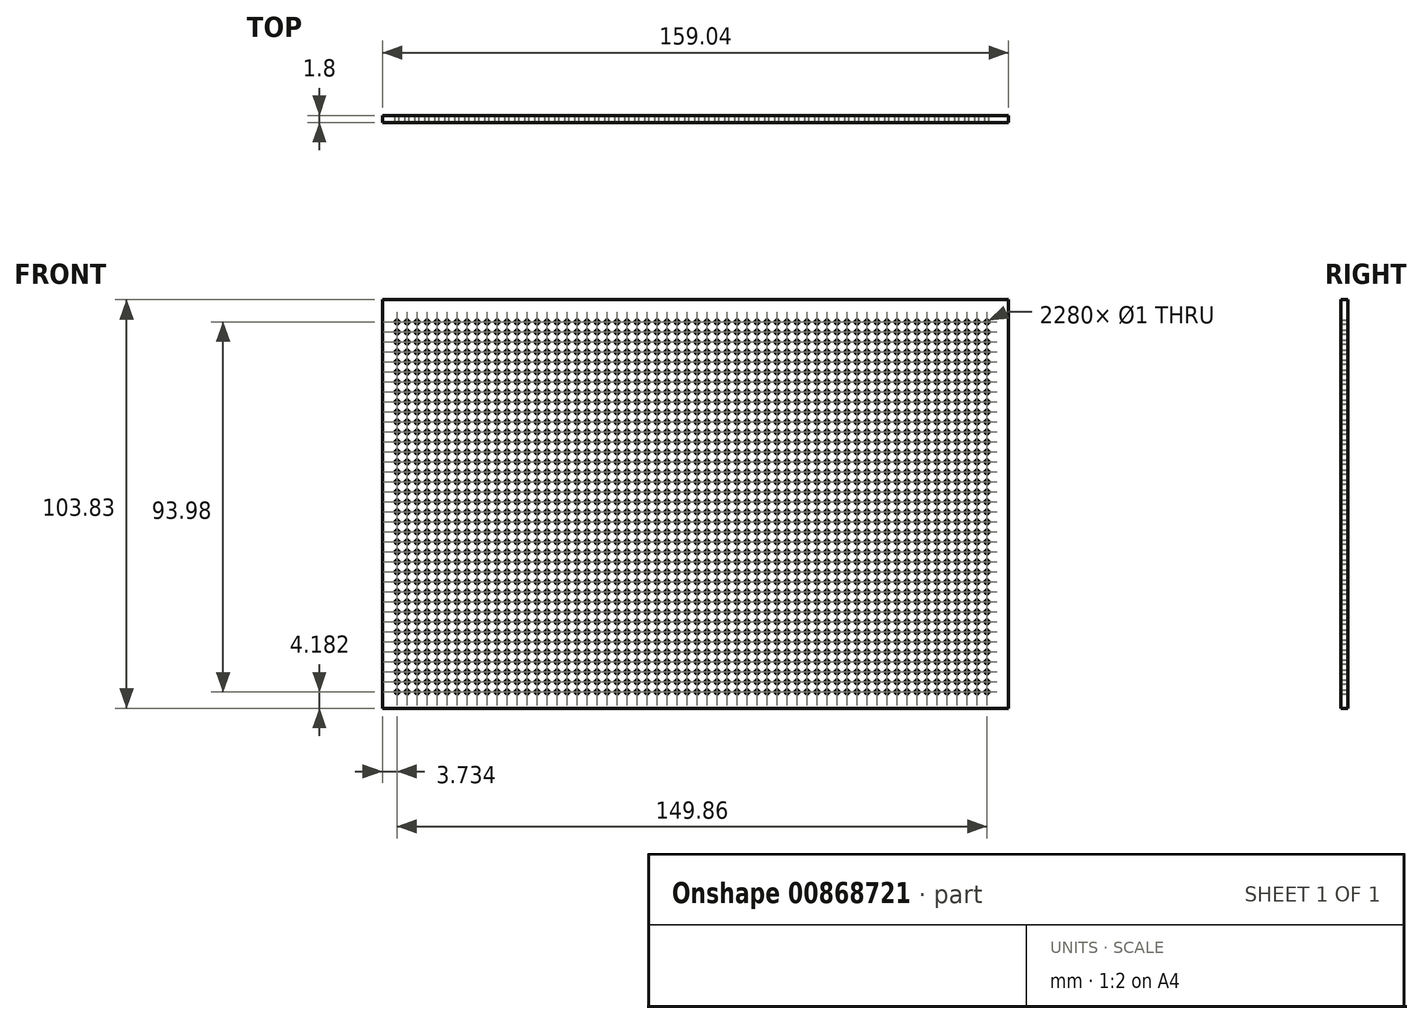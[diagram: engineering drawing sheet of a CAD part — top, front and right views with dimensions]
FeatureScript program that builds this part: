
annotation { "Feature Type Name" : "Feature", "Feature Type Description" : "" }
export const myFeature = defineFeature(function(context is Context, id is Id, definition is map)
    precondition{}
    {
        {
            var Q0;
            Q0=qCreatedBy(makeId("Front.planeOp"),FACE);
            var sketch = newSketch(context, id + "F0", { "sketchPlane" : qUnion([Q0])});
            skCircle(sketch, "E0", {"center": v(-205.8, 91.36) * mm, "radius": 0.5 * mm});
            skCircle(sketch, "E1.0.1.0", {"center": v(-205.8, 93.9) * mm, "radius": 0.5 * mm});
            skCircle(sketch, "E1.0.2.0", {"center": v(-205.8, 96.44) * mm, "radius": 0.5 * mm});
            skCircle(sketch, "E1.0.3.0", {"center": v(-205.8, 98.98) * mm, "radius": 0.5 * mm});
            skCircle(sketch, "E1.0.4.0", {"center": v(-205.8, 101.52) * mm, "radius": 0.5 * mm});
            skCircle(sketch, "E1.0.5.0", {"center": v(-205.8, 104.06) * mm, "radius": 0.5 * mm});
            skCircle(sketch, "E1.0.6.0", {"center": v(-205.8, 106.6) * mm, "radius": 0.5 * mm});
            skCircle(sketch, "E1.0.7.0", {"center": v(-205.8, 109.14) * mm, "radius": 0.5 * mm});
            skCircle(sketch, "E1.0.8.0", {"center": v(-205.8, 111.68) * mm, "radius": 0.5 * mm});
            skCircle(sketch, "E1.0.9.0", {"center": v(-205.8, 114.22) * mm, "radius": 0.5 * mm});
            skCircle(sketch, "E1.0.10.0", {"center": v(-205.8, 116.76) * mm, "radius": 0.5 * mm});
            skCircle(sketch, "E1.0.11.0", {"center": v(-205.8, 119.3) * mm, "radius": 0.5 * mm});
            skCircle(sketch, "E1.0.12.0", {"center": v(-205.8, 121.84) * mm, "radius": 0.5 * mm});
            skCircle(sketch, "E1.0.13.0", {"center": v(-205.8, 124.38) * mm, "radius": 0.5 * mm});
            skCircle(sketch, "E1.0.14.0", {"center": v(-205.8, 126.92) * mm, "radius": 0.5 * mm});
            skCircle(sketch, "E1.0.15.0", {"center": v(-205.8, 129.46) * mm, "radius": 0.5 * mm});
            skCircle(sketch, "E1.0.16.0", {"center": v(-205.8, 132) * mm, "radius": 0.5 * mm});
            skCircle(sketch, "E1.0.17.0", {"center": v(-205.8, 134.54) * mm, "radius": 0.5 * mm});
            skCircle(sketch, "E1.0.18.0", {"center": v(-205.8, 137.08) * mm, "radius": 0.5 * mm});
            skCircle(sketch, "E1.0.19.0", {"center": v(-205.8, 139.62) * mm, "radius": 0.5 * mm});
            skCircle(sketch, "E1.0.20.0", {"center": v(-205.8, 142.16) * mm, "radius": 0.5 * mm});
            skCircle(sketch, "E1.0.21.0", {"center": v(-205.8, 144.7) * mm, "radius": 0.5 * mm});
            skCircle(sketch, "E1.0.22.0", {"center": v(-205.8, 147.24) * mm, "radius": 0.5 * mm});
            skCircle(sketch, "E1.0.23.0", {"center": v(-205.8, 149.78) * mm, "radius": 0.5 * mm});
            skCircle(sketch, "E1.0.24.0", {"center": v(-205.8, 152.32) * mm, "radius": 0.5 * mm});
            skCircle(sketch, "E1.0.25.0", {"center": v(-205.8, 154.86) * mm, "radius": 0.5 * mm});
            skCircle(sketch, "E1.0.26.0", {"center": v(-205.8, 157.4) * mm, "radius": 0.5 * mm});
            skCircle(sketch, "E1.0.27.0", {"center": v(-205.8, 159.94) * mm, "radius": 0.5 * mm});
            skCircle(sketch, "E1.0.28.0", {"center": v(-205.8, 162.48) * mm, "radius": 0.5 * mm});
            skCircle(sketch, "E1.0.29.0", {"center": v(-205.8, 165.02) * mm, "radius": 0.5 * mm});
            skCircle(sketch, "E1.0.30.0", {"center": v(-205.8, 167.56) * mm, "radius": 0.5 * mm});
            skCircle(sketch, "E1.0.31.0", {"center": v(-205.8, 170.1) * mm, "radius": 0.5 * mm});
            skCircle(sketch, "E1.0.32.0", {"center": v(-205.8, 172.64) * mm, "radius": 0.5 * mm});
            skCircle(sketch, "E1.0.33.0", {"center": v(-205.8, 175.18) * mm, "radius": 0.5 * mm});
            skCircle(sketch, "E1.0.34.0", {"center": v(-205.8, 177.72) * mm, "radius": 0.5 * mm});
            skCircle(sketch, "E1.0.35.0", {"center": v(-205.8, 180.26) * mm, "radius": 0.5 * mm});
            skCircle(sketch, "E1.0.36.0", {"center": v(-205.8, 182.8) * mm, "radius": 0.5 * mm});
            skCircle(sketch, "E1.0.37.0", {"center": v(-205.8, 185.34) * mm, "radius": 0.5 * mm});
            skCircle(sketch, "E1.1.0.0", {"center": v(-203.27, 91.36) * mm, "radius": 0.5 * mm});
            skCircle(sketch, "E1.1.1.0", {"center": v(-203.27, 93.9) * mm, "radius": 0.5 * mm});
            skCircle(sketch, "E1.1.2.0", {"center": v(-203.27, 96.44) * mm, "radius": 0.5 * mm});
            skCircle(sketch, "E1.1.3.0", {"center": v(-203.27, 98.98) * mm, "radius": 0.5 * mm});
            skCircle(sketch, "E1.1.4.0", {"center": v(-203.27, 101.52) * mm, "radius": 0.5 * mm});
            skCircle(sketch, "E1.1.5.0", {"center": v(-203.27, 104.06) * mm, "radius": 0.5 * mm});
            skCircle(sketch, "E1.1.6.0", {"center": v(-203.27, 106.6) * mm, "radius": 0.5 * mm});
            skCircle(sketch, "E1.1.7.0", {"center": v(-203.27, 109.14) * mm, "radius": 0.5 * mm});
            skCircle(sketch, "E1.1.8.0", {"center": v(-203.27, 111.68) * mm, "radius": 0.5 * mm});
            skCircle(sketch, "E1.1.9.0", {"center": v(-203.27, 114.22) * mm, "radius": 0.5 * mm});
            skCircle(sketch, "E1.1.10.0", {"center": v(-203.27, 116.76) * mm, "radius": 0.5 * mm});
            skCircle(sketch, "E1.1.11.0", {"center": v(-203.27, 119.3) * mm, "radius": 0.5 * mm});
            skCircle(sketch, "E1.1.12.0", {"center": v(-203.27, 121.84) * mm, "radius": 0.5 * mm});
            skCircle(sketch, "E1.1.13.0", {"center": v(-203.27, 124.38) * mm, "radius": 0.5 * mm});
            skCircle(sketch, "E1.1.14.0", {"center": v(-203.27, 126.92) * mm, "radius": 0.5 * mm});
            skCircle(sketch, "E1.1.15.0", {"center": v(-203.27, 129.46) * mm, "radius": 0.5 * mm});
            skCircle(sketch, "E1.1.16.0", {"center": v(-203.27, 132) * mm, "radius": 0.5 * mm});
            skCircle(sketch, "E1.1.17.0", {"center": v(-203.27, 134.54) * mm, "radius": 0.5 * mm});
            skCircle(sketch, "E1.1.18.0", {"center": v(-203.27, 137.08) * mm, "radius": 0.5 * mm});
            skCircle(sketch, "E1.1.19.0", {"center": v(-203.27, 139.62) * mm, "radius": 0.5 * mm});
            skCircle(sketch, "E1.1.20.0", {"center": v(-203.27, 142.16) * mm, "radius": 0.5 * mm});
            skCircle(sketch, "E1.1.21.0", {"center": v(-203.27, 144.7) * mm, "radius": 0.5 * mm});
            skCircle(sketch, "E1.1.22.0", {"center": v(-203.27, 147.24) * mm, "radius": 0.5 * mm});
            skCircle(sketch, "E1.1.23.0", {"center": v(-203.27, 149.78) * mm, "radius": 0.5 * mm});
            skCircle(sketch, "E1.1.24.0", {"center": v(-203.27, 152.32) * mm, "radius": 0.5 * mm});
            skCircle(sketch, "E1.1.25.0", {"center": v(-203.27, 154.86) * mm, "radius": 0.5 * mm});
            skCircle(sketch, "E1.1.26.0", {"center": v(-203.27, 157.4) * mm, "radius": 0.5 * mm});
            skCircle(sketch, "E1.1.27.0", {"center": v(-203.27, 159.94) * mm, "radius": 0.5 * mm});
            skCircle(sketch, "E1.1.28.0", {"center": v(-203.27, 162.48) * mm, "radius": 0.5 * mm});
            skCircle(sketch, "E1.1.29.0", {"center": v(-203.27, 165.02) * mm, "radius": 0.5 * mm});
            skCircle(sketch, "E1.1.30.0", {"center": v(-203.27, 167.56) * mm, "radius": 0.5 * mm});
            skCircle(sketch, "E1.1.31.0", {"center": v(-203.27, 170.1) * mm, "radius": 0.5 * mm});
            skCircle(sketch, "E1.1.32.0", {"center": v(-203.27, 172.64) * mm, "radius": 0.5 * mm});
            skCircle(sketch, "E1.1.33.0", {"center": v(-203.27, 175.18) * mm, "radius": 0.5 * mm});
            skCircle(sketch, "E1.1.34.0", {"center": v(-203.27, 177.72) * mm, "radius": 0.5 * mm});
            skCircle(sketch, "E1.1.35.0", {"center": v(-203.27, 180.26) * mm, "radius": 0.5 * mm});
            skCircle(sketch, "E1.1.36.0", {"center": v(-203.27, 182.8) * mm, "radius": 0.5 * mm});
            skCircle(sketch, "E1.1.37.0", {"center": v(-203.27, 185.34) * mm, "radius": 0.5 * mm});
            skCircle(sketch, "E1.2.0.0", {"center": v(-200.73, 91.36) * mm, "radius": 0.5 * mm});
            skCircle(sketch, "E1.2.1.0", {"center": v(-200.73, 93.9) * mm, "radius": 0.5 * mm});
            skCircle(sketch, "E1.2.2.0", {"center": v(-200.73, 96.44) * mm, "radius": 0.5 * mm});
            skCircle(sketch, "E1.2.3.0", {"center": v(-200.73, 98.98) * mm, "radius": 0.5 * mm});
            skCircle(sketch, "E1.2.4.0", {"center": v(-200.73, 101.52) * mm, "radius": 0.5 * mm});
            skCircle(sketch, "E1.2.5.0", {"center": v(-200.73, 104.06) * mm, "radius": 0.5 * mm});
            skCircle(sketch, "E1.2.6.0", {"center": v(-200.73, 106.6) * mm, "radius": 0.5 * mm});
            skCircle(sketch, "E1.2.7.0", {"center": v(-200.73, 109.14) * mm, "radius": 0.5 * mm});
            skCircle(sketch, "E1.2.8.0", {"center": v(-200.73, 111.68) * mm, "radius": 0.5 * mm});
            skCircle(sketch, "E1.2.9.0", {"center": v(-200.73, 114.22) * mm, "radius": 0.5 * mm});
            skCircle(sketch, "E1.2.10.0", {"center": v(-200.73, 116.76) * mm, "radius": 0.5 * mm});
            skCircle(sketch, "E1.2.11.0", {"center": v(-200.73, 119.3) * mm, "radius": 0.5 * mm});
            skCircle(sketch, "E1.2.12.0", {"center": v(-200.73, 121.84) * mm, "radius": 0.5 * mm});
            skCircle(sketch, "E1.2.13.0", {"center": v(-200.73, 124.38) * mm, "radius": 0.5 * mm});
            skCircle(sketch, "E1.2.14.0", {"center": v(-200.73, 126.92) * mm, "radius": 0.5 * mm});
            skCircle(sketch, "E1.2.15.0", {"center": v(-200.73, 129.46) * mm, "radius": 0.5 * mm});
            skCircle(sketch, "E1.2.16.0", {"center": v(-200.73, 132) * mm, "radius": 0.5 * mm});
            skCircle(sketch, "E1.2.17.0", {"center": v(-200.73, 134.54) * mm, "radius": 0.5 * mm});
            skCircle(sketch, "E1.2.18.0", {"center": v(-200.73, 137.08) * mm, "radius": 0.5 * mm});
            skCircle(sketch, "E1.2.19.0", {"center": v(-200.73, 139.62) * mm, "radius": 0.5 * mm});
            skCircle(sketch, "E1.2.20.0", {"center": v(-200.73, 142.16) * mm, "radius": 0.5 * mm});
            skCircle(sketch, "E1.2.21.0", {"center": v(-200.73, 144.7) * mm, "radius": 0.5 * mm});
            skCircle(sketch, "E1.2.22.0", {"center": v(-200.73, 147.24) * mm, "radius": 0.5 * mm});
            skCircle(sketch, "E1.2.23.0", {"center": v(-200.73, 149.78) * mm, "radius": 0.5 * mm});
            skCircle(sketch, "E1.2.24.0", {"center": v(-200.73, 152.32) * mm, "radius": 0.5 * mm});
            skCircle(sketch, "E1.2.25.0", {"center": v(-200.73, 154.86) * mm, "radius": 0.5 * mm});
            skCircle(sketch, "E1.2.26.0", {"center": v(-200.73, 157.4) * mm, "radius": 0.5 * mm});
            skCircle(sketch, "E1.2.27.0", {"center": v(-200.73, 159.94) * mm, "radius": 0.5 * mm});
            skCircle(sketch, "E1.2.28.0", {"center": v(-200.73, 162.48) * mm, "radius": 0.5 * mm});
            skCircle(sketch, "E1.2.29.0", {"center": v(-200.73, 165.02) * mm, "radius": 0.5 * mm});
            skCircle(sketch, "E1.2.30.0", {"center": v(-200.73, 167.56) * mm, "radius": 0.5 * mm});
            skCircle(sketch, "E1.2.31.0", {"center": v(-200.73, 170.1) * mm, "radius": 0.5 * mm});
            skCircle(sketch, "E1.2.32.0", {"center": v(-200.73, 172.64) * mm, "radius": 0.5 * mm});
            skCircle(sketch, "E1.2.33.0", {"center": v(-200.73, 175.18) * mm, "radius": 0.5 * mm});
            skCircle(sketch, "E1.2.34.0", {"center": v(-200.73, 177.72) * mm, "radius": 0.5 * mm});
            skCircle(sketch, "E1.2.35.0", {"center": v(-200.73, 180.26) * mm, "radius": 0.5 * mm});
            skCircle(sketch, "E1.2.36.0", {"center": v(-200.73, 182.8) * mm, "radius": 0.5 * mm});
            skCircle(sketch, "E1.2.37.0", {"center": v(-200.73, 185.34) * mm, "radius": 0.5 * mm});
            skCircle(sketch, "E1.3.0.0", {"center": v(-198.19, 91.36) * mm, "radius": 0.5 * mm});
            skCircle(sketch, "E1.3.1.0", {"center": v(-198.19, 93.9) * mm, "radius": 0.5 * mm});
            skCircle(sketch, "E1.3.2.0", {"center": v(-198.19, 96.44) * mm, "radius": 0.5 * mm});
            skCircle(sketch, "E1.3.3.0", {"center": v(-198.19, 98.98) * mm, "radius": 0.5 * mm});
            skCircle(sketch, "E1.3.4.0", {"center": v(-198.19, 101.52) * mm, "radius": 0.5 * mm});
            skCircle(sketch, "E1.3.5.0", {"center": v(-198.19, 104.06) * mm, "radius": 0.5 * mm});
            skCircle(sketch, "E1.3.6.0", {"center": v(-198.19, 106.6) * mm, "radius": 0.5 * mm});
            skCircle(sketch, "E1.3.7.0", {"center": v(-198.19, 109.14) * mm, "radius": 0.5 * mm});
            skCircle(sketch, "E1.3.8.0", {"center": v(-198.19, 111.68) * mm, "radius": 0.5 * mm});
            skCircle(sketch, "E1.3.9.0", {"center": v(-198.19, 114.22) * mm, "radius": 0.5 * mm});
            skCircle(sketch, "E1.3.10.0", {"center": v(-198.19, 116.76) * mm, "radius": 0.5 * mm});
            skCircle(sketch, "E1.3.11.0", {"center": v(-198.19, 119.3) * mm, "radius": 0.5 * mm});
            skCircle(sketch, "E1.3.12.0", {"center": v(-198.19, 121.84) * mm, "radius": 0.5 * mm});
            skCircle(sketch, "E1.3.13.0", {"center": v(-198.19, 124.38) * mm, "radius": 0.5 * mm});
            skCircle(sketch, "E1.3.14.0", {"center": v(-198.19, 126.92) * mm, "radius": 0.5 * mm});
            skCircle(sketch, "E1.3.15.0", {"center": v(-198.19, 129.46) * mm, "radius": 0.5 * mm});
            skCircle(sketch, "E1.3.16.0", {"center": v(-198.19, 132) * mm, "radius": 0.5 * mm});
            skCircle(sketch, "E1.3.17.0", {"center": v(-198.19, 134.54) * mm, "radius": 0.5 * mm});
            skCircle(sketch, "E1.3.18.0", {"center": v(-198.19, 137.08) * mm, "radius": 0.5 * mm});
            skCircle(sketch, "E1.3.19.0", {"center": v(-198.19, 139.62) * mm, "radius": 0.5 * mm});
            skCircle(sketch, "E1.3.20.0", {"center": v(-198.19, 142.16) * mm, "radius": 0.5 * mm});
            skCircle(sketch, "E1.3.21.0", {"center": v(-198.19, 144.7) * mm, "radius": 0.5 * mm});
            skCircle(sketch, "E1.3.22.0", {"center": v(-198.19, 147.24) * mm, "radius": 0.5 * mm});
            skCircle(sketch, "E1.3.23.0", {"center": v(-198.19, 149.78) * mm, "radius": 0.5 * mm});
            skCircle(sketch, "E1.3.24.0", {"center": v(-198.19, 152.32) * mm, "radius": 0.5 * mm});
            skCircle(sketch, "E1.3.25.0", {"center": v(-198.19, 154.86) * mm, "radius": 0.5 * mm});
            skCircle(sketch, "E1.3.26.0", {"center": v(-198.19, 157.4) * mm, "radius": 0.5 * mm});
            skCircle(sketch, "E1.3.27.0", {"center": v(-198.19, 159.94) * mm, "radius": 0.5 * mm});
            skCircle(sketch, "E1.3.28.0", {"center": v(-198.19, 162.48) * mm, "radius": 0.5 * mm});
            skCircle(sketch, "E1.3.29.0", {"center": v(-198.19, 165.02) * mm, "radius": 0.5 * mm});
            skCircle(sketch, "E1.3.30.0", {"center": v(-198.19, 167.56) * mm, "radius": 0.5 * mm});
            skCircle(sketch, "E1.3.31.0", {"center": v(-198.19, 170.1) * mm, "radius": 0.5 * mm});
            skCircle(sketch, "E1.3.32.0", {"center": v(-198.19, 172.64) * mm, "radius": 0.5 * mm});
            skCircle(sketch, "E1.3.33.0", {"center": v(-198.19, 175.18) * mm, "radius": 0.5 * mm});
            skCircle(sketch, "E1.3.34.0", {"center": v(-198.19, 177.72) * mm, "radius": 0.5 * mm});
            skCircle(sketch, "E1.3.35.0", {"center": v(-198.19, 180.26) * mm, "radius": 0.5 * mm});
            skCircle(sketch, "E1.3.36.0", {"center": v(-198.19, 182.8) * mm, "radius": 0.5 * mm});
            skCircle(sketch, "E1.3.37.0", {"center": v(-198.19, 185.34) * mm, "radius": 0.5 * mm});
            skCircle(sketch, "E1.4.0.0", {"center": v(-195.65, 91.36) * mm, "radius": 0.5 * mm});
            skCircle(sketch, "E1.4.1.0", {"center": v(-195.65, 93.9) * mm, "radius": 0.5 * mm});
            skCircle(sketch, "E1.4.2.0", {"center": v(-195.65, 96.44) * mm, "radius": 0.5 * mm});
            skCircle(sketch, "E1.4.3.0", {"center": v(-195.65, 98.98) * mm, "radius": 0.5 * mm});
            skCircle(sketch, "E1.4.4.0", {"center": v(-195.65, 101.52) * mm, "radius": 0.5 * mm});
            skCircle(sketch, "E1.4.5.0", {"center": v(-195.65, 104.06) * mm, "radius": 0.5 * mm});
            skCircle(sketch, "E1.4.6.0", {"center": v(-195.65, 106.6) * mm, "radius": 0.5 * mm});
            skCircle(sketch, "E1.4.7.0", {"center": v(-195.65, 109.14) * mm, "radius": 0.5 * mm});
            skCircle(sketch, "E1.4.8.0", {"center": v(-195.65, 111.68) * mm, "radius": 0.5 * mm});
            skCircle(sketch, "E1.4.9.0", {"center": v(-195.65, 114.22) * mm, "radius": 0.5 * mm});
            skCircle(sketch, "E1.4.10.0", {"center": v(-195.65, 116.76) * mm, "radius": 0.5 * mm});
            skCircle(sketch, "E1.4.11.0", {"center": v(-195.65, 119.3) * mm, "radius": 0.5 * mm});
            skCircle(sketch, "E1.4.12.0", {"center": v(-195.65, 121.84) * mm, "radius": 0.5 * mm});
            skCircle(sketch, "E1.4.13.0", {"center": v(-195.65, 124.38) * mm, "radius": 0.5 * mm});
            skCircle(sketch, "E1.4.14.0", {"center": v(-195.65, 126.92) * mm, "radius": 0.5 * mm});
            skCircle(sketch, "E1.4.15.0", {"center": v(-195.65, 129.46) * mm, "radius": 0.5 * mm});
            skCircle(sketch, "E1.4.16.0", {"center": v(-195.65, 132) * mm, "radius": 0.5 * mm});
            skCircle(sketch, "E1.4.17.0", {"center": v(-195.65, 134.54) * mm, "radius": 0.5 * mm});
            skCircle(sketch, "E1.4.18.0", {"center": v(-195.65, 137.08) * mm, "radius": 0.5 * mm});
            skCircle(sketch, "E1.4.19.0", {"center": v(-195.65, 139.62) * mm, "radius": 0.5 * mm});
            skCircle(sketch, "E1.4.20.0", {"center": v(-195.65, 142.16) * mm, "radius": 0.5 * mm});
            skCircle(sketch, "E1.4.21.0", {"center": v(-195.65, 144.7) * mm, "radius": 0.5 * mm});
            skCircle(sketch, "E1.4.22.0", {"center": v(-195.65, 147.24) * mm, "radius": 0.5 * mm});
            skCircle(sketch, "E1.4.23.0", {"center": v(-195.65, 149.78) * mm, "radius": 0.5 * mm});
            skCircle(sketch, "E1.4.24.0", {"center": v(-195.65, 152.32) * mm, "radius": 0.5 * mm});
            skCircle(sketch, "E1.4.25.0", {"center": v(-195.65, 154.86) * mm, "radius": 0.5 * mm});
            skCircle(sketch, "E1.4.26.0", {"center": v(-195.65, 157.4) * mm, "radius": 0.5 * mm});
            skCircle(sketch, "E1.4.27.0", {"center": v(-195.65, 159.94) * mm, "radius": 0.5 * mm});
            skCircle(sketch, "E1.4.28.0", {"center": v(-195.65, 162.48) * mm, "radius": 0.5 * mm});
            skCircle(sketch, "E1.4.29.0", {"center": v(-195.65, 165.02) * mm, "radius": 0.5 * mm});
            skCircle(sketch, "E1.4.30.0", {"center": v(-195.65, 167.56) * mm, "radius": 0.5 * mm});
            skCircle(sketch, "E1.4.31.0", {"center": v(-195.65, 170.1) * mm, "radius": 0.5 * mm});
            skCircle(sketch, "E1.4.32.0", {"center": v(-195.65, 172.64) * mm, "radius": 0.5 * mm});
            skCircle(sketch, "E1.4.33.0", {"center": v(-195.65, 175.18) * mm, "radius": 0.5 * mm});
            skCircle(sketch, "E1.4.34.0", {"center": v(-195.65, 177.72) * mm, "radius": 0.5 * mm});
            skCircle(sketch, "E1.4.35.0", {"center": v(-195.65, 180.26) * mm, "radius": 0.5 * mm});
            skCircle(sketch, "E1.4.36.0", {"center": v(-195.65, 182.8) * mm, "radius": 0.5 * mm});
            skCircle(sketch, "E1.4.37.0", {"center": v(-195.65, 185.34) * mm, "radius": 0.5 * mm});
            skCircle(sketch, "E1.5.0.0", {"center": v(-193.1, 91.36) * mm, "radius": 0.5 * mm});
            skCircle(sketch, "E1.5.1.0", {"center": v(-193.1, 93.9) * mm, "radius": 0.5 * mm});
            skCircle(sketch, "E1.5.2.0", {"center": v(-193.1, 96.44) * mm, "radius": 0.5 * mm});
            skCircle(sketch, "E1.5.3.0", {"center": v(-193.1, 98.98) * mm, "radius": 0.5 * mm});
            skCircle(sketch, "E1.5.4.0", {"center": v(-193.1, 101.52) * mm, "radius": 0.5 * mm});
            skCircle(sketch, "E1.5.5.0", {"center": v(-193.1, 104.06) * mm, "radius": 0.5 * mm});
            skCircle(sketch, "E1.5.6.0", {"center": v(-193.1, 106.6) * mm, "radius": 0.5 * mm});
            skCircle(sketch, "E1.5.7.0", {"center": v(-193.1, 109.14) * mm, "radius": 0.5 * mm});
            skCircle(sketch, "E1.5.8.0", {"center": v(-193.1, 111.68) * mm, "radius": 0.5 * mm});
            skCircle(sketch, "E1.5.9.0", {"center": v(-193.1, 114.22) * mm, "radius": 0.5 * mm});
            skCircle(sketch, "E1.5.10.0", {"center": v(-193.1, 116.76) * mm, "radius": 0.5 * mm});
            skCircle(sketch, "E1.5.11.0", {"center": v(-193.1, 119.3) * mm, "radius": 0.5 * mm});
            skCircle(sketch, "E1.5.12.0", {"center": v(-193.1, 121.84) * mm, "radius": 0.5 * mm});
            skCircle(sketch, "E1.5.13.0", {"center": v(-193.1, 124.38) * mm, "radius": 0.5 * mm});
            skCircle(sketch, "E1.5.14.0", {"center": v(-193.1, 126.92) * mm, "radius": 0.5 * mm});
            skCircle(sketch, "E1.5.15.0", {"center": v(-193.1, 129.46) * mm, "radius": 0.5 * mm});
            skCircle(sketch, "E1.5.16.0", {"center": v(-193.1, 132) * mm, "radius": 0.5 * mm});
            skCircle(sketch, "E1.5.17.0", {"center": v(-193.1, 134.54) * mm, "radius": 0.5 * mm});
            skCircle(sketch, "E1.5.18.0", {"center": v(-193.1, 137.08) * mm, "radius": 0.5 * mm});
            skCircle(sketch, "E1.5.19.0", {"center": v(-193.1, 139.62) * mm, "radius": 0.5 * mm});
            skCircle(sketch, "E1.5.20.0", {"center": v(-193.1, 142.16) * mm, "radius": 0.5 * mm});
            skCircle(sketch, "E1.5.21.0", {"center": v(-193.1, 144.7) * mm, "radius": 0.5 * mm});
            skCircle(sketch, "E1.5.22.0", {"center": v(-193.1, 147.24) * mm, "radius": 0.5 * mm});
            skCircle(sketch, "E1.5.23.0", {"center": v(-193.1, 149.78) * mm, "radius": 0.5 * mm});
            skCircle(sketch, "E1.5.24.0", {"center": v(-193.1, 152.32) * mm, "radius": 0.5 * mm});
            skCircle(sketch, "E1.5.25.0", {"center": v(-193.1, 154.86) * mm, "radius": 0.5 * mm});
            skCircle(sketch, "E1.5.26.0", {"center": v(-193.1, 157.4) * mm, "radius": 0.5 * mm});
            skCircle(sketch, "E1.5.27.0", {"center": v(-193.1, 159.94) * mm, "radius": 0.5 * mm});
            skCircle(sketch, "E1.5.28.0", {"center": v(-193.1, 162.48) * mm, "radius": 0.5 * mm});
            skCircle(sketch, "E1.5.29.0", {"center": v(-193.1, 165.02) * mm, "radius": 0.5 * mm});
            skCircle(sketch, "E1.5.30.0", {"center": v(-193.1, 167.56) * mm, "radius": 0.5 * mm});
            skCircle(sketch, "E1.5.31.0", {"center": v(-193.1, 170.1) * mm, "radius": 0.5 * mm});
            skCircle(sketch, "E1.5.32.0", {"center": v(-193.1, 172.64) * mm, "radius": 0.5 * mm});
            skCircle(sketch, "E1.5.33.0", {"center": v(-193.1, 175.18) * mm, "radius": 0.5 * mm});
            skCircle(sketch, "E1.5.34.0", {"center": v(-193.1, 177.72) * mm, "radius": 0.5 * mm});
            skCircle(sketch, "E1.5.35.0", {"center": v(-193.1, 180.26) * mm, "radius": 0.5 * mm});
            skCircle(sketch, "E1.5.36.0", {"center": v(-193.1, 182.8) * mm, "radius": 0.5 * mm});
            skCircle(sketch, "E1.5.37.0", {"center": v(-193.1, 185.34) * mm, "radius": 0.5 * mm});
            skCircle(sketch, "E1.6.0.0", {"center": v(-190.57, 91.36) * mm, "radius": 0.5 * mm});
            skCircle(sketch, "E1.6.1.0", {"center": v(-190.57, 93.9) * mm, "radius": 0.5 * mm});
            skCircle(sketch, "E1.6.2.0", {"center": v(-190.57, 96.44) * mm, "radius": 0.5 * mm});
            skCircle(sketch, "E1.6.3.0", {"center": v(-190.57, 98.98) * mm, "radius": 0.5 * mm});
            skCircle(sketch, "E1.6.4.0", {"center": v(-190.57, 101.52) * mm, "radius": 0.5 * mm});
            skCircle(sketch, "E1.6.5.0", {"center": v(-190.57, 104.06) * mm, "radius": 0.5 * mm});
            skCircle(sketch, "E1.6.6.0", {"center": v(-190.57, 106.6) * mm, "radius": 0.5 * mm});
            skCircle(sketch, "E1.6.7.0", {"center": v(-190.57, 109.14) * mm, "radius": 0.5 * mm});
            skCircle(sketch, "E1.6.8.0", {"center": v(-190.57, 111.68) * mm, "radius": 0.5 * mm});
            skCircle(sketch, "E1.6.9.0", {"center": v(-190.57, 114.22) * mm, "radius": 0.5 * mm});
            skCircle(sketch, "E1.6.10.0", {"center": v(-190.57, 116.76) * mm, "radius": 0.5 * mm});
            skCircle(sketch, "E1.6.11.0", {"center": v(-190.57, 119.3) * mm, "radius": 0.5 * mm});
            skCircle(sketch, "E1.6.12.0", {"center": v(-190.57, 121.84) * mm, "radius": 0.5 * mm});
            skCircle(sketch, "E1.6.13.0", {"center": v(-190.57, 124.38) * mm, "radius": 0.5 * mm});
            skCircle(sketch, "E1.6.14.0", {"center": v(-190.57, 126.92) * mm, "radius": 0.5 * mm});
            skCircle(sketch, "E1.6.15.0", {"center": v(-190.57, 129.46) * mm, "radius": 0.5 * mm});
            skCircle(sketch, "E1.6.16.0", {"center": v(-190.57, 132) * mm, "radius": 0.5 * mm});
            skCircle(sketch, "E1.6.17.0", {"center": v(-190.57, 134.54) * mm, "radius": 0.5 * mm});
            skCircle(sketch, "E1.6.18.0", {"center": v(-190.57, 137.08) * mm, "radius": 0.5 * mm});
            skCircle(sketch, "E1.6.19.0", {"center": v(-190.57, 139.62) * mm, "radius": 0.5 * mm});
            skCircle(sketch, "E1.6.20.0", {"center": v(-190.57, 142.16) * mm, "radius": 0.5 * mm});
            skCircle(sketch, "E1.6.21.0", {"center": v(-190.57, 144.7) * mm, "radius": 0.5 * mm});
            skCircle(sketch, "E1.6.22.0", {"center": v(-190.57, 147.24) * mm, "radius": 0.5 * mm});
            skCircle(sketch, "E1.6.23.0", {"center": v(-190.57, 149.78) * mm, "radius": 0.5 * mm});
            skCircle(sketch, "E1.6.24.0", {"center": v(-190.57, 152.32) * mm, "radius": 0.5 * mm});
            skCircle(sketch, "E1.6.25.0", {"center": v(-190.57, 154.86) * mm, "radius": 0.5 * mm});
            skCircle(sketch, "E1.6.26.0", {"center": v(-190.57, 157.4) * mm, "radius": 0.5 * mm});
            skCircle(sketch, "E1.6.27.0", {"center": v(-190.57, 159.94) * mm, "radius": 0.5 * mm});
            skCircle(sketch, "E1.6.28.0", {"center": v(-190.57, 162.48) * mm, "radius": 0.5 * mm});
            skCircle(sketch, "E1.6.29.0", {"center": v(-190.57, 165.02) * mm, "radius": 0.5 * mm});
            skCircle(sketch, "E1.6.30.0", {"center": v(-190.57, 167.56) * mm, "radius": 0.5 * mm});
            skCircle(sketch, "E1.6.31.0", {"center": v(-190.57, 170.1) * mm, "radius": 0.5 * mm});
            skCircle(sketch, "E1.6.32.0", {"center": v(-190.57, 172.64) * mm, "radius": 0.5 * mm});
            skCircle(sketch, "E1.6.33.0", {"center": v(-190.57, 175.18) * mm, "radius": 0.5 * mm});
            skCircle(sketch, "E1.6.34.0", {"center": v(-190.57, 177.72) * mm, "radius": 0.5 * mm});
            skCircle(sketch, "E1.6.35.0", {"center": v(-190.57, 180.26) * mm, "radius": 0.5 * mm});
            skCircle(sketch, "E1.6.36.0", {"center": v(-190.57, 182.8) * mm, "radius": 0.5 * mm});
            skCircle(sketch, "E1.6.37.0", {"center": v(-190.57, 185.34) * mm, "radius": 0.5 * mm});
            skCircle(sketch, "E1.7.0.0", {"center": v(-188.03, 91.36) * mm, "radius": 0.5 * mm});
            skCircle(sketch, "E1.7.1.0", {"center": v(-188.03, 93.9) * mm, "radius": 0.5 * mm});
            skCircle(sketch, "E1.7.2.0", {"center": v(-188.03, 96.44) * mm, "radius": 0.5 * mm});
            skCircle(sketch, "E1.7.3.0", {"center": v(-188.03, 98.98) * mm, "radius": 0.5 * mm});
            skCircle(sketch, "E1.7.4.0", {"center": v(-188.03, 101.52) * mm, "radius": 0.5 * mm});
            skCircle(sketch, "E1.7.5.0", {"center": v(-188.03, 104.06) * mm, "radius": 0.5 * mm});
            skCircle(sketch, "E1.7.6.0", {"center": v(-188.03, 106.6) * mm, "radius": 0.5 * mm});
            skCircle(sketch, "E1.7.7.0", {"center": v(-188.03, 109.14) * mm, "radius": 0.5 * mm});
            skCircle(sketch, "E1.7.8.0", {"center": v(-188.03, 111.68) * mm, "radius": 0.5 * mm});
            skCircle(sketch, "E1.7.9.0", {"center": v(-188.03, 114.22) * mm, "radius": 0.5 * mm});
            skCircle(sketch, "E1.7.10.0", {"center": v(-188.03, 116.76) * mm, "radius": 0.5 * mm});
            skCircle(sketch, "E1.7.11.0", {"center": v(-188.03, 119.3) * mm, "radius": 0.5 * mm});
            skCircle(sketch, "E1.7.12.0", {"center": v(-188.03, 121.84) * mm, "radius": 0.5 * mm});
            skCircle(sketch, "E1.7.13.0", {"center": v(-188.03, 124.38) * mm, "radius": 0.5 * mm});
            skCircle(sketch, "E1.7.14.0", {"center": v(-188.03, 126.92) * mm, "radius": 0.5 * mm});
            skCircle(sketch, "E1.7.15.0", {"center": v(-188.03, 129.46) * mm, "radius": 0.5 * mm});
            skCircle(sketch, "E1.7.16.0", {"center": v(-188.03, 132) * mm, "radius": 0.5 * mm});
            skCircle(sketch, "E1.7.17.0", {"center": v(-188.03, 134.54) * mm, "radius": 0.5 * mm});
            skCircle(sketch, "E1.7.18.0", {"center": v(-188.03, 137.08) * mm, "radius": 0.5 * mm});
            skCircle(sketch, "E1.7.19.0", {"center": v(-188.03, 139.62) * mm, "radius": 0.5 * mm});
            skCircle(sketch, "E1.7.20.0", {"center": v(-188.03, 142.16) * mm, "radius": 0.5 * mm});
            skCircle(sketch, "E1.7.21.0", {"center": v(-188.03, 144.7) * mm, "radius": 0.5 * mm});
            skCircle(sketch, "E1.7.22.0", {"center": v(-188.03, 147.24) * mm, "radius": 0.5 * mm});
            skCircle(sketch, "E1.7.23.0", {"center": v(-188.03, 149.78) * mm, "radius": 0.5 * mm});
            skCircle(sketch, "E1.7.24.0", {"center": v(-188.03, 152.32) * mm, "radius": 0.5 * mm});
            skCircle(sketch, "E1.7.25.0", {"center": v(-188.03, 154.86) * mm, "radius": 0.5 * mm});
            skCircle(sketch, "E1.7.26.0", {"center": v(-188.03, 157.4) * mm, "radius": 0.5 * mm});
            skCircle(sketch, "E1.7.27.0", {"center": v(-188.03, 159.94) * mm, "radius": 0.5 * mm});
            skCircle(sketch, "E1.7.28.0", {"center": v(-188.03, 162.48) * mm, "radius": 0.5 * mm});
            skCircle(sketch, "E1.7.29.0", {"center": v(-188.03, 165.02) * mm, "radius": 0.5 * mm});
            skCircle(sketch, "E1.7.30.0", {"center": v(-188.03, 167.56) * mm, "radius": 0.5 * mm});
            skCircle(sketch, "E1.7.31.0", {"center": v(-188.03, 170.1) * mm, "radius": 0.5 * mm});
            skCircle(sketch, "E1.7.32.0", {"center": v(-188.03, 172.64) * mm, "radius": 0.5 * mm});
            skCircle(sketch, "E1.7.33.0", {"center": v(-188.03, 175.18) * mm, "radius": 0.5 * mm});
            skCircle(sketch, "E1.7.34.0", {"center": v(-188.03, 177.72) * mm, "radius": 0.5 * mm});
            skCircle(sketch, "E1.7.35.0", {"center": v(-188.03, 180.26) * mm, "radius": 0.5 * mm});
            skCircle(sketch, "E1.7.36.0", {"center": v(-188.03, 182.8) * mm, "radius": 0.5 * mm});
            skCircle(sketch, "E1.7.37.0", {"center": v(-188.03, 185.34) * mm, "radius": 0.5 * mm});
            skCircle(sketch, "E1.8.0.0", {"center": v(-185.49, 91.36) * mm, "radius": 0.5 * mm});
            skCircle(sketch, "E1.8.1.0", {"center": v(-185.49, 93.9) * mm, "radius": 0.5 * mm});
            skCircle(sketch, "E1.8.2.0", {"center": v(-185.49, 96.44) * mm, "radius": 0.5 * mm});
            skCircle(sketch, "E1.8.3.0", {"center": v(-185.49, 98.98) * mm, "radius": 0.5 * mm});
            skCircle(sketch, "E1.8.4.0", {"center": v(-185.49, 101.52) * mm, "radius": 0.5 * mm});
            skCircle(sketch, "E1.8.5.0", {"center": v(-185.49, 104.06) * mm, "radius": 0.5 * mm});
            skCircle(sketch, "E1.8.6.0", {"center": v(-185.49, 106.6) * mm, "radius": 0.5 * mm});
            skCircle(sketch, "E1.8.7.0", {"center": v(-185.49, 109.14) * mm, "radius": 0.5 * mm});
            skCircle(sketch, "E1.8.8.0", {"center": v(-185.49, 111.68) * mm, "radius": 0.5 * mm});
            skCircle(sketch, "E1.8.9.0", {"center": v(-185.49, 114.22) * mm, "radius": 0.5 * mm});
            skCircle(sketch, "E1.8.10.0", {"center": v(-185.49, 116.76) * mm, "radius": 0.5 * mm});
            skCircle(sketch, "E1.8.11.0", {"center": v(-185.49, 119.3) * mm, "radius": 0.5 * mm});
            skCircle(sketch, "E1.8.12.0", {"center": v(-185.49, 121.84) * mm, "radius": 0.5 * mm});
            skCircle(sketch, "E1.8.13.0", {"center": v(-185.49, 124.38) * mm, "radius": 0.5 * mm});
            skCircle(sketch, "E1.8.14.0", {"center": v(-185.49, 126.92) * mm, "radius": 0.5 * mm});
            skCircle(sketch, "E1.8.15.0", {"center": v(-185.49, 129.46) * mm, "radius": 0.5 * mm});
            skCircle(sketch, "E1.8.16.0", {"center": v(-185.49, 132) * mm, "radius": 0.5 * mm});
            skCircle(sketch, "E1.8.17.0", {"center": v(-185.49, 134.54) * mm, "radius": 0.5 * mm});
            skCircle(sketch, "E1.8.18.0", {"center": v(-185.49, 137.08) * mm, "radius": 0.5 * mm});
            skCircle(sketch, "E1.8.19.0", {"center": v(-185.49, 139.62) * mm, "radius": 0.5 * mm});
            skCircle(sketch, "E1.8.20.0", {"center": v(-185.49, 142.16) * mm, "radius": 0.5 * mm});
            skCircle(sketch, "E1.8.21.0", {"center": v(-185.49, 144.7) * mm, "radius": 0.5 * mm});
            skCircle(sketch, "E1.8.22.0", {"center": v(-185.49, 147.24) * mm, "radius": 0.5 * mm});
            skCircle(sketch, "E1.8.23.0", {"center": v(-185.49, 149.78) * mm, "radius": 0.5 * mm});
            skCircle(sketch, "E1.8.24.0", {"center": v(-185.49, 152.32) * mm, "radius": 0.5 * mm});
            skCircle(sketch, "E1.8.25.0", {"center": v(-185.49, 154.86) * mm, "radius": 0.5 * mm});
            skCircle(sketch, "E1.8.26.0", {"center": v(-185.49, 157.4) * mm, "radius": 0.5 * mm});
            skCircle(sketch, "E1.8.27.0", {"center": v(-185.49, 159.94) * mm, "radius": 0.5 * mm});
            skCircle(sketch, "E1.8.28.0", {"center": v(-185.49, 162.48) * mm, "radius": 0.5 * mm});
            skCircle(sketch, "E1.8.29.0", {"center": v(-185.49, 165.02) * mm, "radius": 0.5 * mm});
            skCircle(sketch, "E1.8.30.0", {"center": v(-185.49, 167.56) * mm, "radius": 0.5 * mm});
            skCircle(sketch, "E1.8.31.0", {"center": v(-185.49, 170.1) * mm, "radius": 0.5 * mm});
            skCircle(sketch, "E1.8.32.0", {"center": v(-185.49, 172.64) * mm, "radius": 0.5 * mm});
            skCircle(sketch, "E1.8.33.0", {"center": v(-185.49, 175.18) * mm, "radius": 0.5 * mm});
            skCircle(sketch, "E1.8.34.0", {"center": v(-185.49, 177.72) * mm, "radius": 0.5 * mm});
            skCircle(sketch, "E1.8.35.0", {"center": v(-185.49, 180.26) * mm, "radius": 0.5 * mm});
            skCircle(sketch, "E1.8.36.0", {"center": v(-185.49, 182.8) * mm, "radius": 0.5 * mm});
            skCircle(sketch, "E1.8.37.0", {"center": v(-185.49, 185.34) * mm, "radius": 0.5 * mm});
            skCircle(sketch, "E1.9.0.0", {"center": v(-182.95, 91.36) * mm, "radius": 0.5 * mm});
            skCircle(sketch, "E1.9.1.0", {"center": v(-182.95, 93.9) * mm, "radius": 0.5 * mm});
            skCircle(sketch, "E1.9.2.0", {"center": v(-182.95, 96.44) * mm, "radius": 0.5 * mm});
            skCircle(sketch, "E1.9.3.0", {"center": v(-182.95, 98.98) * mm, "radius": 0.5 * mm});
            skCircle(sketch, "E1.9.4.0", {"center": v(-182.95, 101.52) * mm, "radius": 0.5 * mm});
            skCircle(sketch, "E1.9.5.0", {"center": v(-182.95, 104.06) * mm, "radius": 0.5 * mm});
            skCircle(sketch, "E1.9.6.0", {"center": v(-182.95, 106.6) * mm, "radius": 0.5 * mm});
            skCircle(sketch, "E1.9.7.0", {"center": v(-182.95, 109.14) * mm, "radius": 0.5 * mm});
            skCircle(sketch, "E1.9.8.0", {"center": v(-182.95, 111.68) * mm, "radius": 0.5 * mm});
            skCircle(sketch, "E1.9.9.0", {"center": v(-182.95, 114.22) * mm, "radius": 0.5 * mm});
            skCircle(sketch, "E1.9.10.0", {"center": v(-182.95, 116.76) * mm, "radius": 0.5 * mm});
            skCircle(sketch, "E1.9.11.0", {"center": v(-182.95, 119.3) * mm, "radius": 0.5 * mm});
            skCircle(sketch, "E1.9.12.0", {"center": v(-182.95, 121.84) * mm, "radius": 0.5 * mm});
            skCircle(sketch, "E1.9.13.0", {"center": v(-182.95, 124.38) * mm, "radius": 0.5 * mm});
            skCircle(sketch, "E1.9.14.0", {"center": v(-182.95, 126.92) * mm, "radius": 0.5 * mm});
            skCircle(sketch, "E1.9.15.0", {"center": v(-182.95, 129.46) * mm, "radius": 0.5 * mm});
            skCircle(sketch, "E1.9.16.0", {"center": v(-182.95, 132) * mm, "radius": 0.5 * mm});
            skCircle(sketch, "E1.9.17.0", {"center": v(-182.95, 134.54) * mm, "radius": 0.5 * mm});
            skCircle(sketch, "E1.9.18.0", {"center": v(-182.95, 137.08) * mm, "radius": 0.5 * mm});
            skCircle(sketch, "E1.9.19.0", {"center": v(-182.95, 139.62) * mm, "radius": 0.5 * mm});
            skCircle(sketch, "E1.9.20.0", {"center": v(-182.95, 142.16) * mm, "radius": 0.5 * mm});
            skCircle(sketch, "E1.9.21.0", {"center": v(-182.95, 144.7) * mm, "radius": 0.5 * mm});
            skCircle(sketch, "E1.9.22.0", {"center": v(-182.95, 147.24) * mm, "radius": 0.5 * mm});
            skCircle(sketch, "E1.9.23.0", {"center": v(-182.95, 149.78) * mm, "radius": 0.5 * mm});
            skCircle(sketch, "E1.9.24.0", {"center": v(-182.95, 152.32) * mm, "radius": 0.5 * mm});
            skCircle(sketch, "E1.9.25.0", {"center": v(-182.95, 154.86) * mm, "radius": 0.5 * mm});
            skCircle(sketch, "E1.9.26.0", {"center": v(-182.95, 157.4) * mm, "radius": 0.5 * mm});
            skCircle(sketch, "E1.9.27.0", {"center": v(-182.95, 159.94) * mm, "radius": 0.5 * mm});
            skCircle(sketch, "E1.9.28.0", {"center": v(-182.95, 162.48) * mm, "radius": 0.5 * mm});
            skCircle(sketch, "E1.9.29.0", {"center": v(-182.95, 165.02) * mm, "radius": 0.5 * mm});
            skCircle(sketch, "E1.9.30.0", {"center": v(-182.95, 167.56) * mm, "radius": 0.5 * mm});
            skCircle(sketch, "E1.9.31.0", {"center": v(-182.95, 170.1) * mm, "radius": 0.5 * mm});
            skCircle(sketch, "E1.9.32.0", {"center": v(-182.95, 172.64) * mm, "radius": 0.5 * mm});
            skCircle(sketch, "E1.9.33.0", {"center": v(-182.95, 175.18) * mm, "radius": 0.5 * mm});
            skCircle(sketch, "E1.9.34.0", {"center": v(-182.95, 177.72) * mm, "radius": 0.5 * mm});
            skCircle(sketch, "E1.9.35.0", {"center": v(-182.95, 180.26) * mm, "radius": 0.5 * mm});
            skCircle(sketch, "E1.9.36.0", {"center": v(-182.95, 182.8) * mm, "radius": 0.5 * mm});
            skCircle(sketch, "E1.9.37.0", {"center": v(-182.95, 185.34) * mm, "radius": 0.5 * mm});
            skCircle(sketch, "E1.10.0.0", {"center": v(-180.4, 91.36) * mm, "radius": 0.5 * mm});
            skCircle(sketch, "E1.10.1.0", {"center": v(-180.4, 93.9) * mm, "radius": 0.5 * mm});
            skCircle(sketch, "E1.10.2.0", {"center": v(-180.4, 96.44) * mm, "radius": 0.5 * mm});
            skCircle(sketch, "E1.10.3.0", {"center": v(-180.4, 98.98) * mm, "radius": 0.5 * mm});
            skCircle(sketch, "E1.10.4.0", {"center": v(-180.4, 101.52) * mm, "radius": 0.5 * mm});
            skCircle(sketch, "E1.10.5.0", {"center": v(-180.4, 104.06) * mm, "radius": 0.5 * mm});
            skCircle(sketch, "E1.10.6.0", {"center": v(-180.4, 106.6) * mm, "radius": 0.5 * mm});
            skCircle(sketch, "E1.10.7.0", {"center": v(-180.4, 109.14) * mm, "radius": 0.5 * mm});
            skCircle(sketch, "E1.10.8.0", {"center": v(-180.4, 111.68) * mm, "radius": 0.5 * mm});
            skCircle(sketch, "E1.10.9.0", {"center": v(-180.4, 114.22) * mm, "radius": 0.5 * mm});
            skCircle(sketch, "E1.10.10.0", {"center": v(-180.4, 116.76) * mm, "radius": 0.5 * mm});
            skCircle(sketch, "E1.10.11.0", {"center": v(-180.4, 119.3) * mm, "radius": 0.5 * mm});
            skCircle(sketch, "E1.10.12.0", {"center": v(-180.4, 121.84) * mm, "radius": 0.5 * mm});
            skCircle(sketch, "E1.10.13.0", {"center": v(-180.4, 124.38) * mm, "radius": 0.5 * mm});
            skCircle(sketch, "E1.10.14.0", {"center": v(-180.4, 126.92) * mm, "radius": 0.5 * mm});
            skCircle(sketch, "E1.10.15.0", {"center": v(-180.4, 129.46) * mm, "radius": 0.5 * mm});
            skCircle(sketch, "E1.10.16.0", {"center": v(-180.4, 132) * mm, "radius": 0.5 * mm});
            skCircle(sketch, "E1.10.17.0", {"center": v(-180.4, 134.54) * mm, "radius": 0.5 * mm});
            skCircle(sketch, "E1.10.18.0", {"center": v(-180.4, 137.08) * mm, "radius": 0.5 * mm});
            skCircle(sketch, "E1.10.19.0", {"center": v(-180.4, 139.62) * mm, "radius": 0.5 * mm});
            skCircle(sketch, "E1.10.20.0", {"center": v(-180.4, 142.16) * mm, "radius": 0.5 * mm});
            skCircle(sketch, "E1.10.21.0", {"center": v(-180.4, 144.7) * mm, "radius": 0.5 * mm});
            skCircle(sketch, "E1.10.22.0", {"center": v(-180.4, 147.24) * mm, "radius": 0.5 * mm});
            skCircle(sketch, "E1.10.23.0", {"center": v(-180.4, 149.78) * mm, "radius": 0.5 * mm});
            skCircle(sketch, "E1.10.24.0", {"center": v(-180.4, 152.32) * mm, "radius": 0.5 * mm});
            skCircle(sketch, "E1.10.25.0", {"center": v(-180.4, 154.86) * mm, "radius": 0.5 * mm});
            skCircle(sketch, "E1.10.26.0", {"center": v(-180.4, 157.4) * mm, "radius": 0.5 * mm});
            skCircle(sketch, "E1.10.27.0", {"center": v(-180.4, 159.94) * mm, "radius": 0.5 * mm});
            skCircle(sketch, "E1.10.28.0", {"center": v(-180.4, 162.48) * mm, "radius": 0.5 * mm});
            skCircle(sketch, "E1.10.29.0", {"center": v(-180.4, 165.02) * mm, "radius": 0.5 * mm});
            skCircle(sketch, "E1.10.30.0", {"center": v(-180.4, 167.56) * mm, "radius": 0.5 * mm});
            skCircle(sketch, "E1.10.31.0", {"center": v(-180.4, 170.1) * mm, "radius": 0.5 * mm});
            skCircle(sketch, "E1.10.32.0", {"center": v(-180.4, 172.64) * mm, "radius": 0.5 * mm});
            skCircle(sketch, "E1.10.33.0", {"center": v(-180.4, 175.18) * mm, "radius": 0.5 * mm});
            skCircle(sketch, "E1.10.34.0", {"center": v(-180.4, 177.72) * mm, "radius": 0.5 * mm});
            skCircle(sketch, "E1.10.35.0", {"center": v(-180.4, 180.26) * mm, "radius": 0.5 * mm});
            skCircle(sketch, "E1.10.36.0", {"center": v(-180.4, 182.8) * mm, "radius": 0.5 * mm});
            skCircle(sketch, "E1.10.37.0", {"center": v(-180.4, 185.34) * mm, "radius": 0.5 * mm});
            skCircle(sketch, "E1.11.0.0", {"center": v(-177.87, 91.36) * mm, "radius": 0.5 * mm});
            skCircle(sketch, "E1.11.1.0", {"center": v(-177.87, 93.9) * mm, "radius": 0.5 * mm});
            skCircle(sketch, "E1.11.2.0", {"center": v(-177.87, 96.44) * mm, "radius": 0.5 * mm});
            skCircle(sketch, "E1.11.3.0", {"center": v(-177.87, 98.98) * mm, "radius": 0.5 * mm});
            skCircle(sketch, "E1.11.4.0", {"center": v(-177.87, 101.52) * mm, "radius": 0.5 * mm});
            skCircle(sketch, "E1.11.5.0", {"center": v(-177.87, 104.06) * mm, "radius": 0.5 * mm});
            skCircle(sketch, "E1.11.6.0", {"center": v(-177.87, 106.6) * mm, "radius": 0.5 * mm});
            skCircle(sketch, "E1.11.7.0", {"center": v(-177.87, 109.14) * mm, "radius": 0.5 * mm});
            skCircle(sketch, "E1.11.8.0", {"center": v(-177.87, 111.68) * mm, "radius": 0.5 * mm});
            skCircle(sketch, "E1.11.9.0", {"center": v(-177.87, 114.22) * mm, "radius": 0.5 * mm});
            skCircle(sketch, "E1.11.10.0", {"center": v(-177.87, 116.76) * mm, "radius": 0.5 * mm});
            skCircle(sketch, "E1.11.11.0", {"center": v(-177.87, 119.3) * mm, "radius": 0.5 * mm});
            skCircle(sketch, "E1.11.12.0", {"center": v(-177.87, 121.84) * mm, "radius": 0.5 * mm});
            skCircle(sketch, "E1.11.13.0", {"center": v(-177.87, 124.38) * mm, "radius": 0.5 * mm});
            skCircle(sketch, "E1.11.14.0", {"center": v(-177.87, 126.92) * mm, "radius": 0.5 * mm});
            skCircle(sketch, "E1.11.15.0", {"center": v(-177.87, 129.46) * mm, "radius": 0.5 * mm});
            skCircle(sketch, "E1.11.16.0", {"center": v(-177.87, 132) * mm, "radius": 0.5 * mm});
            skCircle(sketch, "E1.11.17.0", {"center": v(-177.87, 134.54) * mm, "radius": 0.5 * mm});
            skCircle(sketch, "E1.11.18.0", {"center": v(-177.87, 137.08) * mm, "radius": 0.5 * mm});
            skCircle(sketch, "E1.11.19.0", {"center": v(-177.87, 139.62) * mm, "radius": 0.5 * mm});
            skCircle(sketch, "E1.11.20.0", {"center": v(-177.87, 142.16) * mm, "radius": 0.5 * mm});
            skCircle(sketch, "E1.11.21.0", {"center": v(-177.87, 144.7) * mm, "radius": 0.5 * mm});
            skCircle(sketch, "E1.11.22.0", {"center": v(-177.87, 147.24) * mm, "radius": 0.5 * mm});
            skCircle(sketch, "E1.11.23.0", {"center": v(-177.87, 149.78) * mm, "radius": 0.5 * mm});
            skCircle(sketch, "E1.11.24.0", {"center": v(-177.87, 152.32) * mm, "radius": 0.5 * mm});
            skCircle(sketch, "E1.11.25.0", {"center": v(-177.87, 154.86) * mm, "radius": 0.5 * mm});
            skCircle(sketch, "E1.11.26.0", {"center": v(-177.87, 157.4) * mm, "radius": 0.5 * mm});
            skCircle(sketch, "E1.11.27.0", {"center": v(-177.87, 159.94) * mm, "radius": 0.5 * mm});
            skCircle(sketch, "E1.11.28.0", {"center": v(-177.87, 162.48) * mm, "radius": 0.5 * mm});
            skCircle(sketch, "E1.11.29.0", {"center": v(-177.87, 165.02) * mm, "radius": 0.5 * mm});
            skCircle(sketch, "E1.11.30.0", {"center": v(-177.87, 167.56) * mm, "radius": 0.5 * mm});
            skCircle(sketch, "E1.11.31.0", {"center": v(-177.87, 170.1) * mm, "radius": 0.5 * mm});
            skCircle(sketch, "E1.11.32.0", {"center": v(-177.87, 172.64) * mm, "radius": 0.5 * mm});
            skCircle(sketch, "E1.11.33.0", {"center": v(-177.87, 175.18) * mm, "radius": 0.5 * mm});
            skCircle(sketch, "E1.11.34.0", {"center": v(-177.87, 177.72) * mm, "radius": 0.5 * mm});
            skCircle(sketch, "E1.11.35.0", {"center": v(-177.87, 180.26) * mm, "radius": 0.5 * mm});
            skCircle(sketch, "E1.11.36.0", {"center": v(-177.87, 182.8) * mm, "radius": 0.5 * mm});
            skCircle(sketch, "E1.11.37.0", {"center": v(-177.87, 185.34) * mm, "radius": 0.5 * mm});
            skCircle(sketch, "E1.12.0.0", {"center": v(-175.33, 91.36) * mm, "radius": 0.5 * mm});
            skCircle(sketch, "E1.12.1.0", {"center": v(-175.33, 93.9) * mm, "radius": 0.5 * mm});
            skCircle(sketch, "E1.12.2.0", {"center": v(-175.33, 96.44) * mm, "radius": 0.5 * mm});
            skCircle(sketch, "E1.12.3.0", {"center": v(-175.33, 98.98) * mm, "radius": 0.5 * mm});
            skCircle(sketch, "E1.12.4.0", {"center": v(-175.33, 101.52) * mm, "radius": 0.5 * mm});
            skCircle(sketch, "E1.12.5.0", {"center": v(-175.33, 104.06) * mm, "radius": 0.5 * mm});
            skCircle(sketch, "E1.12.6.0", {"center": v(-175.33, 106.6) * mm, "radius": 0.5 * mm});
            skCircle(sketch, "E1.12.7.0", {"center": v(-175.33, 109.14) * mm, "radius": 0.5 * mm});
            skCircle(sketch, "E1.12.8.0", {"center": v(-175.33, 111.68) * mm, "radius": 0.5 * mm});
            skCircle(sketch, "E1.12.9.0", {"center": v(-175.33, 114.22) * mm, "radius": 0.5 * mm});
            skCircle(sketch, "E1.12.10.0", {"center": v(-175.33, 116.76) * mm, "radius": 0.5 * mm});
            skCircle(sketch, "E1.12.11.0", {"center": v(-175.33, 119.3) * mm, "radius": 0.5 * mm});
            skCircle(sketch, "E1.12.12.0", {"center": v(-175.33, 121.84) * mm, "radius": 0.5 * mm});
            skCircle(sketch, "E1.12.13.0", {"center": v(-175.33, 124.38) * mm, "radius": 0.5 * mm});
            skCircle(sketch, "E1.12.14.0", {"center": v(-175.33, 126.92) * mm, "radius": 0.5 * mm});
            skCircle(sketch, "E1.12.15.0", {"center": v(-175.33, 129.46) * mm, "radius": 0.5 * mm});
            skCircle(sketch, "E1.12.16.0", {"center": v(-175.33, 132) * mm, "radius": 0.5 * mm});
            skCircle(sketch, "E1.12.17.0", {"center": v(-175.33, 134.54) * mm, "radius": 0.5 * mm});
            skCircle(sketch, "E1.12.18.0", {"center": v(-175.33, 137.08) * mm, "radius": 0.5 * mm});
            skCircle(sketch, "E1.12.19.0", {"center": v(-175.33, 139.62) * mm, "radius": 0.5 * mm});
            skCircle(sketch, "E1.12.20.0", {"center": v(-175.33, 142.16) * mm, "radius": 0.5 * mm});
            skCircle(sketch, "E1.12.21.0", {"center": v(-175.33, 144.7) * mm, "radius": 0.5 * mm});
            skCircle(sketch, "E1.12.22.0", {"center": v(-175.33, 147.24) * mm, "radius": 0.5 * mm});
            skCircle(sketch, "E1.12.23.0", {"center": v(-175.33, 149.78) * mm, "radius": 0.5 * mm});
            skCircle(sketch, "E1.12.24.0", {"center": v(-175.33, 152.32) * mm, "radius": 0.5 * mm});
            skCircle(sketch, "E1.12.25.0", {"center": v(-175.33, 154.86) * mm, "radius": 0.5 * mm});
            skCircle(sketch, "E1.12.26.0", {"center": v(-175.33, 157.4) * mm, "radius": 0.5 * mm});
            skCircle(sketch, "E1.12.27.0", {"center": v(-175.33, 159.94) * mm, "radius": 0.5 * mm});
            skCircle(sketch, "E1.12.28.0", {"center": v(-175.33, 162.48) * mm, "radius": 0.5 * mm});
            skCircle(sketch, "E1.12.29.0", {"center": v(-175.33, 165.02) * mm, "radius": 0.5 * mm});
            skCircle(sketch, "E1.12.30.0", {"center": v(-175.33, 167.56) * mm, "radius": 0.5 * mm});
            skCircle(sketch, "E1.12.31.0", {"center": v(-175.33, 170.1) * mm, "radius": 0.5 * mm});
            skCircle(sketch, "E1.12.32.0", {"center": v(-175.33, 172.64) * mm, "radius": 0.5 * mm});
            skCircle(sketch, "E1.12.33.0", {"center": v(-175.33, 175.18) * mm, "radius": 0.5 * mm});
            skCircle(sketch, "E1.12.34.0", {"center": v(-175.33, 177.72) * mm, "radius": 0.5 * mm});
            skCircle(sketch, "E1.12.35.0", {"center": v(-175.33, 180.26) * mm, "radius": 0.5 * mm});
            skCircle(sketch, "E1.12.36.0", {"center": v(-175.33, 182.8) * mm, "radius": 0.5 * mm});
            skCircle(sketch, "E1.12.37.0", {"center": v(-175.33, 185.34) * mm, "radius": 0.5 * mm});
            skCircle(sketch, "E1.13.0.0", {"center": v(-172.79, 91.36) * mm, "radius": 0.5 * mm});
            skCircle(sketch, "E1.13.1.0", {"center": v(-172.79, 93.9) * mm, "radius": 0.5 * mm});
            skCircle(sketch, "E1.13.2.0", {"center": v(-172.79, 96.44) * mm, "radius": 0.5 * mm});
            skCircle(sketch, "E1.13.3.0", {"center": v(-172.79, 98.98) * mm, "radius": 0.5 * mm});
            skCircle(sketch, "E1.13.4.0", {"center": v(-172.79, 101.52) * mm, "radius": 0.5 * mm});
            skCircle(sketch, "E1.13.5.0", {"center": v(-172.79, 104.06) * mm, "radius": 0.5 * mm});
            skCircle(sketch, "E1.13.6.0", {"center": v(-172.79, 106.6) * mm, "radius": 0.5 * mm});
            skCircle(sketch, "E1.13.7.0", {"center": v(-172.79, 109.14) * mm, "radius": 0.5 * mm});
            skCircle(sketch, "E1.13.8.0", {"center": v(-172.79, 111.68) * mm, "radius": 0.5 * mm});
            skCircle(sketch, "E1.13.9.0", {"center": v(-172.79, 114.22) * mm, "radius": 0.5 * mm});
            skCircle(sketch, "E1.13.10.0", {"center": v(-172.79, 116.76) * mm, "radius": 0.5 * mm});
            skCircle(sketch, "E1.13.11.0", {"center": v(-172.79, 119.3) * mm, "radius": 0.5 * mm});
            skCircle(sketch, "E1.13.12.0", {"center": v(-172.79, 121.84) * mm, "radius": 0.5 * mm});
            skCircle(sketch, "E1.13.13.0", {"center": v(-172.79, 124.38) * mm, "radius": 0.5 * mm});
            skCircle(sketch, "E1.13.14.0", {"center": v(-172.79, 126.92) * mm, "radius": 0.5 * mm});
            skCircle(sketch, "E1.13.15.0", {"center": v(-172.79, 129.46) * mm, "radius": 0.5 * mm});
            skCircle(sketch, "E1.13.16.0", {"center": v(-172.79, 132) * mm, "radius": 0.5 * mm});
            skCircle(sketch, "E1.13.17.0", {"center": v(-172.79, 134.54) * mm, "radius": 0.5 * mm});
            skCircle(sketch, "E1.13.18.0", {"center": v(-172.79, 137.08) * mm, "radius": 0.5 * mm});
            skCircle(sketch, "E1.13.19.0", {"center": v(-172.79, 139.62) * mm, "radius": 0.5 * mm});
            skCircle(sketch, "E1.13.20.0", {"center": v(-172.79, 142.16) * mm, "radius": 0.5 * mm});
            skCircle(sketch, "E1.13.21.0", {"center": v(-172.79, 144.7) * mm, "radius": 0.5 * mm});
            skCircle(sketch, "E1.13.22.0", {"center": v(-172.79, 147.24) * mm, "radius": 0.5 * mm});
            skCircle(sketch, "E1.13.23.0", {"center": v(-172.79, 149.78) * mm, "radius": 0.5 * mm});
            skCircle(sketch, "E1.13.24.0", {"center": v(-172.79, 152.32) * mm, "radius": 0.5 * mm});
            skCircle(sketch, "E1.13.25.0", {"center": v(-172.79, 154.86) * mm, "radius": 0.5 * mm});
            skCircle(sketch, "E1.13.26.0", {"center": v(-172.79, 157.4) * mm, "radius": 0.5 * mm});
            skCircle(sketch, "E1.13.27.0", {"center": v(-172.79, 159.94) * mm, "radius": 0.5 * mm});
            skCircle(sketch, "E1.13.28.0", {"center": v(-172.79, 162.48) * mm, "radius": 0.5 * mm});
            skCircle(sketch, "E1.13.29.0", {"center": v(-172.79, 165.02) * mm, "radius": 0.5 * mm});
            skCircle(sketch, "E1.13.30.0", {"center": v(-172.79, 167.56) * mm, "radius": 0.5 * mm});
            skCircle(sketch, "E1.13.31.0", {"center": v(-172.79, 170.1) * mm, "radius": 0.5 * mm});
            skCircle(sketch, "E1.13.32.0", {"center": v(-172.79, 172.64) * mm, "radius": 0.5 * mm});
            skCircle(sketch, "E1.13.33.0", {"center": v(-172.79, 175.18) * mm, "radius": 0.5 * mm});
            skCircle(sketch, "E1.13.34.0", {"center": v(-172.79, 177.72) * mm, "radius": 0.5 * mm});
            skCircle(sketch, "E1.13.35.0", {"center": v(-172.79, 180.26) * mm, "radius": 0.5 * mm});
            skCircle(sketch, "E1.13.36.0", {"center": v(-172.79, 182.8) * mm, "radius": 0.5 * mm});
            skCircle(sketch, "E1.13.37.0", {"center": v(-172.79, 185.34) * mm, "radius": 0.5 * mm});
            skCircle(sketch, "E1.14.0.0", {"center": v(-170.25, 91.36) * mm, "radius": 0.5 * mm});
            skCircle(sketch, "E1.14.1.0", {"center": v(-170.25, 93.9) * mm, "radius": 0.5 * mm});
            skCircle(sketch, "E1.14.2.0", {"center": v(-170.25, 96.44) * mm, "radius": 0.5 * mm});
            skCircle(sketch, "E1.14.3.0", {"center": v(-170.25, 98.98) * mm, "radius": 0.5 * mm});
            skCircle(sketch, "E1.14.4.0", {"center": v(-170.25, 101.52) * mm, "radius": 0.5 * mm});
            skCircle(sketch, "E1.14.5.0", {"center": v(-170.25, 104.06) * mm, "radius": 0.5 * mm});
            skCircle(sketch, "E1.14.6.0", {"center": v(-170.25, 106.6) * mm, "radius": 0.5 * mm});
            skCircle(sketch, "E1.14.7.0", {"center": v(-170.25, 109.14) * mm, "radius": 0.5 * mm});
            skCircle(sketch, "E1.14.8.0", {"center": v(-170.25, 111.68) * mm, "radius": 0.5 * mm});
            skCircle(sketch, "E1.14.9.0", {"center": v(-170.25, 114.22) * mm, "radius": 0.5 * mm});
            skCircle(sketch, "E1.14.10.0", {"center": v(-170.25, 116.76) * mm, "radius": 0.5 * mm});
            skCircle(sketch, "E1.14.11.0", {"center": v(-170.25, 119.3) * mm, "radius": 0.5 * mm});
            skCircle(sketch, "E1.14.12.0", {"center": v(-170.25, 121.84) * mm, "radius": 0.5 * mm});
            skCircle(sketch, "E1.14.13.0", {"center": v(-170.25, 124.38) * mm, "radius": 0.5 * mm});
            skCircle(sketch, "E1.14.14.0", {"center": v(-170.25, 126.92) * mm, "radius": 0.5 * mm});
            skCircle(sketch, "E1.14.15.0", {"center": v(-170.25, 129.46) * mm, "radius": 0.5 * mm});
            skCircle(sketch, "E1.14.16.0", {"center": v(-170.25, 132) * mm, "radius": 0.5 * mm});
            skCircle(sketch, "E1.14.17.0", {"center": v(-170.25, 134.54) * mm, "radius": 0.5 * mm});
            skCircle(sketch, "E1.14.18.0", {"center": v(-170.25, 137.08) * mm, "radius": 0.5 * mm});
            skCircle(sketch, "E1.14.19.0", {"center": v(-170.25, 139.62) * mm, "radius": 0.5 * mm});
            skCircle(sketch, "E1.14.20.0", {"center": v(-170.25, 142.16) * mm, "radius": 0.5 * mm});
            skCircle(sketch, "E1.14.21.0", {"center": v(-170.25, 144.7) * mm, "radius": 0.5 * mm});
            skCircle(sketch, "E1.14.22.0", {"center": v(-170.25, 147.24) * mm, "radius": 0.5 * mm});
            skCircle(sketch, "E1.14.23.0", {"center": v(-170.25, 149.78) * mm, "radius": 0.5 * mm});
            skCircle(sketch, "E1.14.24.0", {"center": v(-170.25, 152.32) * mm, "radius": 0.5 * mm});
            skCircle(sketch, "E1.14.25.0", {"center": v(-170.25, 154.86) * mm, "radius": 0.5 * mm});
            skCircle(sketch, "E1.14.26.0", {"center": v(-170.25, 157.4) * mm, "radius": 0.5 * mm});
            skCircle(sketch, "E1.14.27.0", {"center": v(-170.25, 159.94) * mm, "radius": 0.5 * mm});
            skCircle(sketch, "E1.14.28.0", {"center": v(-170.25, 162.48) * mm, "radius": 0.5 * mm});
            skCircle(sketch, "E1.14.29.0", {"center": v(-170.25, 165.02) * mm, "radius": 0.5 * mm});
            skCircle(sketch, "E1.14.30.0", {"center": v(-170.25, 167.56) * mm, "radius": 0.5 * mm});
            skCircle(sketch, "E1.14.31.0", {"center": v(-170.25, 170.1) * mm, "radius": 0.5 * mm});
            skCircle(sketch, "E1.14.32.0", {"center": v(-170.25, 172.64) * mm, "radius": 0.5 * mm});
            skCircle(sketch, "E1.14.33.0", {"center": v(-170.25, 175.18) * mm, "radius": 0.5 * mm});
            skCircle(sketch, "E1.14.34.0", {"center": v(-170.25, 177.72) * mm, "radius": 0.5 * mm});
            skCircle(sketch, "E1.14.35.0", {"center": v(-170.25, 180.26) * mm, "radius": 0.5 * mm});
            skCircle(sketch, "E1.14.36.0", {"center": v(-170.25, 182.8) * mm, "radius": 0.5 * mm});
            skCircle(sketch, "E1.14.37.0", {"center": v(-170.25, 185.34) * mm, "radius": 0.5 * mm});
            skCircle(sketch, "E1.15.0.0", {"center": v(-167.7, 91.36) * mm, "radius": 0.5 * mm});
            skCircle(sketch, "E1.15.1.0", {"center": v(-167.7, 93.9) * mm, "radius": 0.5 * mm});
            skCircle(sketch, "E1.15.2.0", {"center": v(-167.7, 96.44) * mm, "radius": 0.5 * mm});
            skCircle(sketch, "E1.15.3.0", {"center": v(-167.7, 98.98) * mm, "radius": 0.5 * mm});
            skCircle(sketch, "E1.15.4.0", {"center": v(-167.7, 101.52) * mm, "radius": 0.5 * mm});
            skCircle(sketch, "E1.15.5.0", {"center": v(-167.7, 104.06) * mm, "radius": 0.5 * mm});
            skCircle(sketch, "E1.15.6.0", {"center": v(-167.7, 106.6) * mm, "radius": 0.5 * mm});
            skCircle(sketch, "E1.15.7.0", {"center": v(-167.7, 109.14) * mm, "radius": 0.5 * mm});
            skCircle(sketch, "E1.15.8.0", {"center": v(-167.7, 111.68) * mm, "radius": 0.5 * mm});
            skCircle(sketch, "E1.15.9.0", {"center": v(-167.7, 114.22) * mm, "radius": 0.5 * mm});
            skCircle(sketch, "E1.15.10.0", {"center": v(-167.7, 116.76) * mm, "radius": 0.5 * mm});
            skCircle(sketch, "E1.15.11.0", {"center": v(-167.7, 119.3) * mm, "radius": 0.5 * mm});
            skCircle(sketch, "E1.15.12.0", {"center": v(-167.7, 121.84) * mm, "radius": 0.5 * mm});
            skCircle(sketch, "E1.15.13.0", {"center": v(-167.7, 124.38) * mm, "radius": 0.5 * mm});
            skCircle(sketch, "E1.15.14.0", {"center": v(-167.7, 126.92) * mm, "radius": 0.5 * mm});
            skCircle(sketch, "E1.15.15.0", {"center": v(-167.7, 129.46) * mm, "radius": 0.5 * mm});
            skCircle(sketch, "E1.15.16.0", {"center": v(-167.7, 132) * mm, "radius": 0.5 * mm});
            skCircle(sketch, "E1.15.17.0", {"center": v(-167.7, 134.54) * mm, "radius": 0.5 * mm});
            skCircle(sketch, "E1.15.18.0", {"center": v(-167.7, 137.08) * mm, "radius": 0.5 * mm});
            skCircle(sketch, "E1.15.19.0", {"center": v(-167.7, 139.62) * mm, "radius": 0.5 * mm});
            skCircle(sketch, "E1.15.20.0", {"center": v(-167.7, 142.16) * mm, "radius": 0.5 * mm});
            skCircle(sketch, "E1.15.21.0", {"center": v(-167.7, 144.7) * mm, "radius": 0.5 * mm});
            skCircle(sketch, "E1.15.22.0", {"center": v(-167.7, 147.24) * mm, "radius": 0.5 * mm});
            skCircle(sketch, "E1.15.23.0", {"center": v(-167.7, 149.78) * mm, "radius": 0.5 * mm});
            skCircle(sketch, "E1.15.24.0", {"center": v(-167.7, 152.32) * mm, "radius": 0.5 * mm});
            skCircle(sketch, "E1.15.25.0", {"center": v(-167.7, 154.86) * mm, "radius": 0.5 * mm});
            skCircle(sketch, "E1.15.26.0", {"center": v(-167.7, 157.4) * mm, "radius": 0.5 * mm});
            skCircle(sketch, "E1.15.27.0", {"center": v(-167.7, 159.94) * mm, "radius": 0.5 * mm});
            skCircle(sketch, "E1.15.28.0", {"center": v(-167.7, 162.48) * mm, "radius": 0.5 * mm});
            skCircle(sketch, "E1.15.29.0", {"center": v(-167.7, 165.02) * mm, "radius": 0.5 * mm});
            skCircle(sketch, "E1.15.30.0", {"center": v(-167.7, 167.56) * mm, "radius": 0.5 * mm});
            skCircle(sketch, "E1.15.31.0", {"center": v(-167.7, 170.1) * mm, "radius": 0.5 * mm});
            skCircle(sketch, "E1.15.32.0", {"center": v(-167.7, 172.64) * mm, "radius": 0.5 * mm});
            skCircle(sketch, "E1.15.33.0", {"center": v(-167.7, 175.18) * mm, "radius": 0.5 * mm});
            skCircle(sketch, "E1.15.34.0", {"center": v(-167.7, 177.72) * mm, "radius": 0.5 * mm});
            skCircle(sketch, "E1.15.35.0", {"center": v(-167.7, 180.26) * mm, "radius": 0.5 * mm});
            skCircle(sketch, "E1.15.36.0", {"center": v(-167.7, 182.8) * mm, "radius": 0.5 * mm});
            skCircle(sketch, "E1.15.37.0", {"center": v(-167.7, 185.34) * mm, "radius": 0.5 * mm});
            skCircle(sketch, "E1.16.0.0", {"center": v(-165.17, 91.36) * mm, "radius": 0.5 * mm});
            skCircle(sketch, "E1.16.1.0", {"center": v(-165.17, 93.9) * mm, "radius": 0.5 * mm});
            skCircle(sketch, "E1.16.2.0", {"center": v(-165.17, 96.44) * mm, "radius": 0.5 * mm});
            skCircle(sketch, "E1.16.3.0", {"center": v(-165.17, 98.98) * mm, "radius": 0.5 * mm});
            skCircle(sketch, "E1.16.4.0", {"center": v(-165.17, 101.52) * mm, "radius": 0.5 * mm});
            skCircle(sketch, "E1.16.5.0", {"center": v(-165.17, 104.06) * mm, "radius": 0.5 * mm});
            skCircle(sketch, "E1.16.6.0", {"center": v(-165.17, 106.6) * mm, "radius": 0.5 * mm});
            skCircle(sketch, "E1.16.7.0", {"center": v(-165.17, 109.14) * mm, "radius": 0.5 * mm});
            skCircle(sketch, "E1.16.8.0", {"center": v(-165.17, 111.68) * mm, "radius": 0.5 * mm});
            skCircle(sketch, "E1.16.9.0", {"center": v(-165.17, 114.22) * mm, "radius": 0.5 * mm});
            skCircle(sketch, "E1.16.10.0", {"center": v(-165.17, 116.76) * mm, "radius": 0.5 * mm});
            skCircle(sketch, "E1.16.11.0", {"center": v(-165.17, 119.3) * mm, "radius": 0.5 * mm});
            skCircle(sketch, "E1.16.12.0", {"center": v(-165.17, 121.84) * mm, "radius": 0.5 * mm});
            skCircle(sketch, "E1.16.13.0", {"center": v(-165.17, 124.38) * mm, "radius": 0.5 * mm});
            skCircle(sketch, "E1.16.14.0", {"center": v(-165.17, 126.92) * mm, "radius": 0.5 * mm});
            skCircle(sketch, "E1.16.15.0", {"center": v(-165.17, 129.46) * mm, "radius": 0.5 * mm});
            skCircle(sketch, "E1.16.16.0", {"center": v(-165.17, 132) * mm, "radius": 0.5 * mm});
            skCircle(sketch, "E1.16.17.0", {"center": v(-165.17, 134.54) * mm, "radius": 0.5 * mm});
            skCircle(sketch, "E1.16.18.0", {"center": v(-165.17, 137.08) * mm, "radius": 0.5 * mm});
            skCircle(sketch, "E1.16.19.0", {"center": v(-165.17, 139.62) * mm, "radius": 0.5 * mm});
            skCircle(sketch, "E1.16.20.0", {"center": v(-165.17, 142.16) * mm, "radius": 0.5 * mm});
            skCircle(sketch, "E1.16.21.0", {"center": v(-165.17, 144.7) * mm, "radius": 0.5 * mm});
            skCircle(sketch, "E1.16.22.0", {"center": v(-165.17, 147.24) * mm, "radius": 0.5 * mm});
            skCircle(sketch, "E1.16.23.0", {"center": v(-165.17, 149.78) * mm, "radius": 0.5 * mm});
            skCircle(sketch, "E1.16.24.0", {"center": v(-165.17, 152.32) * mm, "radius": 0.5 * mm});
            skCircle(sketch, "E1.16.25.0", {"center": v(-165.17, 154.86) * mm, "radius": 0.5 * mm});
            skCircle(sketch, "E1.16.26.0", {"center": v(-165.17, 157.4) * mm, "radius": 0.5 * mm});
            skCircle(sketch, "E1.16.27.0", {"center": v(-165.17, 159.94) * mm, "radius": 0.5 * mm});
            skCircle(sketch, "E1.16.28.0", {"center": v(-165.17, 162.48) * mm, "radius": 0.5 * mm});
            skCircle(sketch, "E1.16.29.0", {"center": v(-165.17, 165.02) * mm, "radius": 0.5 * mm});
            skCircle(sketch, "E1.16.30.0", {"center": v(-165.17, 167.56) * mm, "radius": 0.5 * mm});
            skCircle(sketch, "E1.16.31.0", {"center": v(-165.17, 170.1) * mm, "radius": 0.5 * mm});
            skCircle(sketch, "E1.16.32.0", {"center": v(-165.17, 172.64) * mm, "radius": 0.5 * mm});
            skCircle(sketch, "E1.16.33.0", {"center": v(-165.17, 175.18) * mm, "radius": 0.5 * mm});
            skCircle(sketch, "E1.16.34.0", {"center": v(-165.17, 177.72) * mm, "radius": 0.5 * mm});
            skCircle(sketch, "E1.16.35.0", {"center": v(-165.17, 180.26) * mm, "radius": 0.5 * mm});
            skCircle(sketch, "E1.16.36.0", {"center": v(-165.17, 182.8) * mm, "radius": 0.5 * mm});
            skCircle(sketch, "E1.16.37.0", {"center": v(-165.17, 185.34) * mm, "radius": 0.5 * mm});
            skCircle(sketch, "E1.17.0.0", {"center": v(-162.63, 91.36) * mm, "radius": 0.5 * mm});
            skCircle(sketch, "E1.17.1.0", {"center": v(-162.63, 93.9) * mm, "radius": 0.5 * mm});
            skCircle(sketch, "E1.17.2.0", {"center": v(-162.63, 96.44) * mm, "radius": 0.5 * mm});
            skCircle(sketch, "E1.17.3.0", {"center": v(-162.63, 98.98) * mm, "radius": 0.5 * mm});
            skCircle(sketch, "E1.17.4.0", {"center": v(-162.63, 101.52) * mm, "radius": 0.5 * mm});
            skCircle(sketch, "E1.17.5.0", {"center": v(-162.63, 104.06) * mm, "radius": 0.5 * mm});
            skCircle(sketch, "E1.17.6.0", {"center": v(-162.63, 106.6) * mm, "radius": 0.5 * mm});
            skCircle(sketch, "E1.17.7.0", {"center": v(-162.63, 109.14) * mm, "radius": 0.5 * mm});
            skCircle(sketch, "E1.17.8.0", {"center": v(-162.63, 111.68) * mm, "radius": 0.5 * mm});
            skCircle(sketch, "E1.17.9.0", {"center": v(-162.63, 114.22) * mm, "radius": 0.5 * mm});
            skCircle(sketch, "E1.17.10.0", {"center": v(-162.63, 116.76) * mm, "radius": 0.5 * mm});
            skCircle(sketch, "E1.17.11.0", {"center": v(-162.63, 119.3) * mm, "radius": 0.5 * mm});
            skCircle(sketch, "E1.17.12.0", {"center": v(-162.63, 121.84) * mm, "radius": 0.5 * mm});
            skCircle(sketch, "E1.17.13.0", {"center": v(-162.63, 124.38) * mm, "radius": 0.5 * mm});
            skCircle(sketch, "E1.17.14.0", {"center": v(-162.63, 126.92) * mm, "radius": 0.5 * mm});
            skCircle(sketch, "E1.17.15.0", {"center": v(-162.63, 129.46) * mm, "radius": 0.5 * mm});
            skCircle(sketch, "E1.17.16.0", {"center": v(-162.63, 132) * mm, "radius": 0.5 * mm});
            skCircle(sketch, "E1.17.17.0", {"center": v(-162.63, 134.54) * mm, "radius": 0.5 * mm});
            skCircle(sketch, "E1.17.18.0", {"center": v(-162.63, 137.08) * mm, "radius": 0.5 * mm});
            skCircle(sketch, "E1.17.19.0", {"center": v(-162.63, 139.62) * mm, "radius": 0.5 * mm});
            skCircle(sketch, "E1.17.20.0", {"center": v(-162.63, 142.16) * mm, "radius": 0.5 * mm});
            skCircle(sketch, "E1.17.21.0", {"center": v(-162.63, 144.7) * mm, "radius": 0.5 * mm});
            skCircle(sketch, "E1.17.22.0", {"center": v(-162.63, 147.24) * mm, "radius": 0.5 * mm});
            skCircle(sketch, "E1.17.23.0", {"center": v(-162.63, 149.78) * mm, "radius": 0.5 * mm});
            skCircle(sketch, "E1.17.24.0", {"center": v(-162.63, 152.32) * mm, "radius": 0.5 * mm});
            skCircle(sketch, "E1.17.25.0", {"center": v(-162.63, 154.86) * mm, "radius": 0.5 * mm});
            skCircle(sketch, "E1.17.26.0", {"center": v(-162.63, 157.4) * mm, "radius": 0.5 * mm});
            skCircle(sketch, "E1.17.27.0", {"center": v(-162.63, 159.94) * mm, "radius": 0.5 * mm});
            skCircle(sketch, "E1.17.28.0", {"center": v(-162.63, 162.48) * mm, "radius": 0.5 * mm});
            skCircle(sketch, "E1.17.29.0", {"center": v(-162.63, 165.02) * mm, "radius": 0.5 * mm});
            skCircle(sketch, "E1.17.30.0", {"center": v(-162.63, 167.56) * mm, "radius": 0.5 * mm});
            skCircle(sketch, "E1.17.31.0", {"center": v(-162.63, 170.1) * mm, "radius": 0.5 * mm});
            skCircle(sketch, "E1.17.32.0", {"center": v(-162.63, 172.64) * mm, "radius": 0.5 * mm});
            skCircle(sketch, "E1.17.33.0", {"center": v(-162.63, 175.18) * mm, "radius": 0.5 * mm});
            skCircle(sketch, "E1.17.34.0", {"center": v(-162.63, 177.72) * mm, "radius": 0.5 * mm});
            skCircle(sketch, "E1.17.35.0", {"center": v(-162.63, 180.26) * mm, "radius": 0.5 * mm});
            skCircle(sketch, "E1.17.36.0", {"center": v(-162.63, 182.8) * mm, "radius": 0.5 * mm});
            skCircle(sketch, "E1.17.37.0", {"center": v(-162.63, 185.34) * mm, "radius": 0.5 * mm});
            skCircle(sketch, "E1.18.0.0", {"center": v(-160.09, 91.36) * mm, "radius": 0.5 * mm});
            skCircle(sketch, "E1.18.1.0", {"center": v(-160.09, 93.9) * mm, "radius": 0.5 * mm});
            skCircle(sketch, "E1.18.2.0", {"center": v(-160.09, 96.44) * mm, "radius": 0.5 * mm});
            skCircle(sketch, "E1.18.3.0", {"center": v(-160.09, 98.98) * mm, "radius": 0.5 * mm});
            skCircle(sketch, "E1.18.4.0", {"center": v(-160.09, 101.52) * mm, "radius": 0.5 * mm});
            skCircle(sketch, "E1.18.5.0", {"center": v(-160.09, 104.06) * mm, "radius": 0.5 * mm});
            skCircle(sketch, "E1.18.6.0", {"center": v(-160.09, 106.6) * mm, "radius": 0.5 * mm});
            skCircle(sketch, "E1.18.7.0", {"center": v(-160.09, 109.14) * mm, "radius": 0.5 * mm});
            skCircle(sketch, "E1.18.8.0", {"center": v(-160.09, 111.68) * mm, "radius": 0.5 * mm});
            skCircle(sketch, "E1.18.9.0", {"center": v(-160.09, 114.22) * mm, "radius": 0.5 * mm});
            skCircle(sketch, "E1.18.10.0", {"center": v(-160.09, 116.76) * mm, "radius": 0.5 * mm});
            skCircle(sketch, "E1.18.11.0", {"center": v(-160.09, 119.3) * mm, "radius": 0.5 * mm});
            skCircle(sketch, "E1.18.12.0", {"center": v(-160.09, 121.84) * mm, "radius": 0.5 * mm});
            skCircle(sketch, "E1.18.13.0", {"center": v(-160.09, 124.38) * mm, "radius": 0.5 * mm});
            skCircle(sketch, "E1.18.14.0", {"center": v(-160.09, 126.92) * mm, "radius": 0.5 * mm});
            skCircle(sketch, "E1.18.15.0", {"center": v(-160.09, 129.46) * mm, "radius": 0.5 * mm});
            skCircle(sketch, "E1.18.16.0", {"center": v(-160.09, 132) * mm, "radius": 0.5 * mm});
            skCircle(sketch, "E1.18.17.0", {"center": v(-160.09, 134.54) * mm, "radius": 0.5 * mm});
            skCircle(sketch, "E1.18.18.0", {"center": v(-160.09, 137.08) * mm, "radius": 0.5 * mm});
            skCircle(sketch, "E1.18.19.0", {"center": v(-160.09, 139.62) * mm, "radius": 0.5 * mm});
            skCircle(sketch, "E1.18.20.0", {"center": v(-160.09, 142.16) * mm, "radius": 0.5 * mm});
            skCircle(sketch, "E1.18.21.0", {"center": v(-160.09, 144.7) * mm, "radius": 0.5 * mm});
            skCircle(sketch, "E1.18.22.0", {"center": v(-160.09, 147.24) * mm, "radius": 0.5 * mm});
            skCircle(sketch, "E1.18.23.0", {"center": v(-160.09, 149.78) * mm, "radius": 0.5 * mm});
            skCircle(sketch, "E1.18.24.0", {"center": v(-160.09, 152.32) * mm, "radius": 0.5 * mm});
            skCircle(sketch, "E1.18.25.0", {"center": v(-160.09, 154.86) * mm, "radius": 0.5 * mm});
            skCircle(sketch, "E1.18.26.0", {"center": v(-160.09, 157.4) * mm, "radius": 0.5 * mm});
            skCircle(sketch, "E1.18.27.0", {"center": v(-160.09, 159.94) * mm, "radius": 0.5 * mm});
            skCircle(sketch, "E1.18.28.0", {"center": v(-160.09, 162.48) * mm, "radius": 0.5 * mm});
            skCircle(sketch, "E1.18.29.0", {"center": v(-160.09, 165.02) * mm, "radius": 0.5 * mm});
            skCircle(sketch, "E1.18.30.0", {"center": v(-160.09, 167.56) * mm, "radius": 0.5 * mm});
            skCircle(sketch, "E1.18.31.0", {"center": v(-160.09, 170.1) * mm, "radius": 0.5 * mm});
            skCircle(sketch, "E1.18.32.0", {"center": v(-160.09, 172.64) * mm, "radius": 0.5 * mm});
            skCircle(sketch, "E1.18.33.0", {"center": v(-160.09, 175.18) * mm, "radius": 0.5 * mm});
            skCircle(sketch, "E1.18.34.0", {"center": v(-160.09, 177.72) * mm, "radius": 0.5 * mm});
            skCircle(sketch, "E1.18.35.0", {"center": v(-160.09, 180.26) * mm, "radius": 0.5 * mm});
            skCircle(sketch, "E1.18.36.0", {"center": v(-160.09, 182.8) * mm, "radius": 0.5 * mm});
            skCircle(sketch, "E1.18.37.0", {"center": v(-160.09, 185.34) * mm, "radius": 0.5 * mm});
            skCircle(sketch, "E1.19.0.0", {"center": v(-157.55, 91.36) * mm, "radius": 0.5 * mm});
            skCircle(sketch, "E1.19.1.0", {"center": v(-157.55, 93.9) * mm, "radius": 0.5 * mm});
            skCircle(sketch, "E1.19.2.0", {"center": v(-157.55, 96.44) * mm, "radius": 0.5 * mm});
            skCircle(sketch, "E1.19.3.0", {"center": v(-157.55, 98.98) * mm, "radius": 0.5 * mm});
            skCircle(sketch, "E1.19.4.0", {"center": v(-157.55, 101.52) * mm, "radius": 0.5 * mm});
            skCircle(sketch, "E1.19.5.0", {"center": v(-157.55, 104.06) * mm, "radius": 0.5 * mm});
            skCircle(sketch, "E1.19.6.0", {"center": v(-157.55, 106.6) * mm, "radius": 0.5 * mm});
            skCircle(sketch, "E1.19.7.0", {"center": v(-157.55, 109.14) * mm, "radius": 0.5 * mm});
            skCircle(sketch, "E1.19.8.0", {"center": v(-157.55, 111.68) * mm, "radius": 0.5 * mm});
            skCircle(sketch, "E1.19.9.0", {"center": v(-157.55, 114.22) * mm, "radius": 0.5 * mm});
            skCircle(sketch, "E1.19.10.0", {"center": v(-157.55, 116.76) * mm, "radius": 0.5 * mm});
            skCircle(sketch, "E1.19.11.0", {"center": v(-157.55, 119.3) * mm, "radius": 0.5 * mm});
            skCircle(sketch, "E1.19.12.0", {"center": v(-157.55, 121.84) * mm, "radius": 0.5 * mm});
            skCircle(sketch, "E1.19.13.0", {"center": v(-157.55, 124.38) * mm, "radius": 0.5 * mm});
            skCircle(sketch, "E1.19.14.0", {"center": v(-157.55, 126.92) * mm, "radius": 0.5 * mm});
            skCircle(sketch, "E1.19.15.0", {"center": v(-157.55, 129.46) * mm, "radius": 0.5 * mm});
            skCircle(sketch, "E1.19.16.0", {"center": v(-157.55, 132) * mm, "radius": 0.5 * mm});
            skCircle(sketch, "E1.19.17.0", {"center": v(-157.55, 134.54) * mm, "radius": 0.5 * mm});
            skCircle(sketch, "E1.19.18.0", {"center": v(-157.55, 137.08) * mm, "radius": 0.5 * mm});
            skCircle(sketch, "E1.19.19.0", {"center": v(-157.55, 139.62) * mm, "radius": 0.5 * mm});
            skCircle(sketch, "E1.19.20.0", {"center": v(-157.55, 142.16) * mm, "radius": 0.5 * mm});
            skCircle(sketch, "E1.19.21.0", {"center": v(-157.55, 144.7) * mm, "radius": 0.5 * mm});
            skCircle(sketch, "E1.19.22.0", {"center": v(-157.55, 147.24) * mm, "radius": 0.5 * mm});
            skCircle(sketch, "E1.19.23.0", {"center": v(-157.55, 149.78) * mm, "radius": 0.5 * mm});
            skCircle(sketch, "E1.19.24.0", {"center": v(-157.55, 152.32) * mm, "radius": 0.5 * mm});
            skCircle(sketch, "E1.19.25.0", {"center": v(-157.55, 154.86) * mm, "radius": 0.5 * mm});
            skCircle(sketch, "E1.19.26.0", {"center": v(-157.55, 157.4) * mm, "radius": 0.5 * mm});
            skCircle(sketch, "E1.19.27.0", {"center": v(-157.55, 159.94) * mm, "radius": 0.5 * mm});
            skCircle(sketch, "E1.19.28.0", {"center": v(-157.55, 162.48) * mm, "radius": 0.5 * mm});
            skCircle(sketch, "E1.19.29.0", {"center": v(-157.55, 165.02) * mm, "radius": 0.5 * mm});
            skCircle(sketch, "E1.19.30.0", {"center": v(-157.55, 167.56) * mm, "radius": 0.5 * mm});
            skCircle(sketch, "E1.19.31.0", {"center": v(-157.55, 170.1) * mm, "radius": 0.5 * mm});
            skCircle(sketch, "E1.19.32.0", {"center": v(-157.55, 172.64) * mm, "radius": 0.5 * mm});
            skCircle(sketch, "E1.19.33.0", {"center": v(-157.55, 175.18) * mm, "radius": 0.5 * mm});
            skCircle(sketch, "E1.19.34.0", {"center": v(-157.55, 177.72) * mm, "radius": 0.5 * mm});
            skCircle(sketch, "E1.19.35.0", {"center": v(-157.55, 180.26) * mm, "radius": 0.5 * mm});
            skCircle(sketch, "E1.19.36.0", {"center": v(-157.55, 182.8) * mm, "radius": 0.5 * mm});
            skCircle(sketch, "E1.19.37.0", {"center": v(-157.55, 185.34) * mm, "radius": 0.5 * mm});
            skCircle(sketch, "E1.20.0.0", {"center": v(-155, 91.36) * mm, "radius": 0.5 * mm});
            skCircle(sketch, "E1.20.1.0", {"center": v(-155, 93.9) * mm, "radius": 0.5 * mm});
            skCircle(sketch, "E1.20.2.0", {"center": v(-155, 96.44) * mm, "radius": 0.5 * mm});
            skCircle(sketch, "E1.20.3.0", {"center": v(-155, 98.98) * mm, "radius": 0.5 * mm});
            skCircle(sketch, "E1.20.4.0", {"center": v(-155, 101.52) * mm, "radius": 0.5 * mm});
            skCircle(sketch, "E1.20.5.0", {"center": v(-155, 104.06) * mm, "radius": 0.5 * mm});
            skCircle(sketch, "E1.20.6.0", {"center": v(-155, 106.6) * mm, "radius": 0.5 * mm});
            skCircle(sketch, "E1.20.7.0", {"center": v(-155, 109.14) * mm, "radius": 0.5 * mm});
            skCircle(sketch, "E1.20.8.0", {"center": v(-155, 111.68) * mm, "radius": 0.5 * mm});
            skCircle(sketch, "E1.20.9.0", {"center": v(-155, 114.22) * mm, "radius": 0.5 * mm});
            skCircle(sketch, "E1.20.10.0", {"center": v(-155, 116.76) * mm, "radius": 0.5 * mm});
            skCircle(sketch, "E1.20.11.0", {"center": v(-155, 119.3) * mm, "radius": 0.5 * mm});
            skCircle(sketch, "E1.20.12.0", {"center": v(-155, 121.84) * mm, "radius": 0.5 * mm});
            skCircle(sketch, "E1.20.13.0", {"center": v(-155, 124.38) * mm, "radius": 0.5 * mm});
            skCircle(sketch, "E1.20.14.0", {"center": v(-155, 126.92) * mm, "radius": 0.5 * mm});
            skCircle(sketch, "E1.20.15.0", {"center": v(-155, 129.46) * mm, "radius": 0.5 * mm});
            skCircle(sketch, "E1.20.16.0", {"center": v(-155, 132) * mm, "radius": 0.5 * mm});
            skCircle(sketch, "E1.20.17.0", {"center": v(-155, 134.54) * mm, "radius": 0.5 * mm});
            skCircle(sketch, "E1.20.18.0", {"center": v(-155, 137.08) * mm, "radius": 0.5 * mm});
            skCircle(sketch, "E1.20.19.0", {"center": v(-155, 139.62) * mm, "radius": 0.5 * mm});
            skCircle(sketch, "E1.20.20.0", {"center": v(-155, 142.16) * mm, "radius": 0.5 * mm});
            skCircle(sketch, "E1.20.21.0", {"center": v(-155, 144.7) * mm, "radius": 0.5 * mm});
            skCircle(sketch, "E1.20.22.0", {"center": v(-155, 147.24) * mm, "radius": 0.5 * mm});
            skCircle(sketch, "E1.20.23.0", {"center": v(-155, 149.78) * mm, "radius": 0.5 * mm});
            skCircle(sketch, "E1.20.24.0", {"center": v(-155, 152.32) * mm, "radius": 0.5 * mm});
            skCircle(sketch, "E1.20.25.0", {"center": v(-155, 154.86) * mm, "radius": 0.5 * mm});
            skCircle(sketch, "E1.20.26.0", {"center": v(-155, 157.4) * mm, "radius": 0.5 * mm});
            skCircle(sketch, "E1.20.27.0", {"center": v(-155, 159.94) * mm, "radius": 0.5 * mm});
            skCircle(sketch, "E1.20.28.0", {"center": v(-155, 162.48) * mm, "radius": 0.5 * mm});
            skCircle(sketch, "E1.20.29.0", {"center": v(-155, 165.02) * mm, "radius": 0.5 * mm});
            skCircle(sketch, "E1.20.30.0", {"center": v(-155, 167.56) * mm, "radius": 0.5 * mm});
            skCircle(sketch, "E1.20.31.0", {"center": v(-155, 170.1) * mm, "radius": 0.5 * mm});
            skCircle(sketch, "E1.20.32.0", {"center": v(-155, 172.64) * mm, "radius": 0.5 * mm});
            skCircle(sketch, "E1.20.33.0", {"center": v(-155, 175.18) * mm, "radius": 0.5 * mm});
            skCircle(sketch, "E1.20.34.0", {"center": v(-155, 177.72) * mm, "radius": 0.5 * mm});
            skCircle(sketch, "E1.20.35.0", {"center": v(-155, 180.26) * mm, "radius": 0.5 * mm});
            skCircle(sketch, "E1.20.36.0", {"center": v(-155, 182.8) * mm, "radius": 0.5 * mm});
            skCircle(sketch, "E1.20.37.0", {"center": v(-155, 185.34) * mm, "radius": 0.5 * mm});
            skCircle(sketch, "E1.21.0.0", {"center": v(-152.47, 91.36) * mm, "radius": 0.5 * mm});
            skCircle(sketch, "E1.21.1.0", {"center": v(-152.47, 93.9) * mm, "radius": 0.5 * mm});
            skCircle(sketch, "E1.21.2.0", {"center": v(-152.47, 96.44) * mm, "radius": 0.5 * mm});
            skCircle(sketch, "E1.21.3.0", {"center": v(-152.47, 98.98) * mm, "radius": 0.5 * mm});
            skCircle(sketch, "E1.21.4.0", {"center": v(-152.47, 101.52) * mm, "radius": 0.5 * mm});
            skCircle(sketch, "E1.21.5.0", {"center": v(-152.47, 104.06) * mm, "radius": 0.5 * mm});
            skCircle(sketch, "E1.21.6.0", {"center": v(-152.47, 106.6) * mm, "radius": 0.5 * mm});
            skCircle(sketch, "E1.21.7.0", {"center": v(-152.47, 109.14) * mm, "radius": 0.5 * mm});
            skCircle(sketch, "E1.21.8.0", {"center": v(-152.47, 111.68) * mm, "radius": 0.5 * mm});
            skCircle(sketch, "E1.21.9.0", {"center": v(-152.47, 114.22) * mm, "radius": 0.5 * mm});
            skCircle(sketch, "E1.21.10.0", {"center": v(-152.47, 116.76) * mm, "radius": 0.5 * mm});
            skCircle(sketch, "E1.21.11.0", {"center": v(-152.47, 119.3) * mm, "radius": 0.5 * mm});
            skCircle(sketch, "E1.21.12.0", {"center": v(-152.47, 121.84) * mm, "radius": 0.5 * mm});
            skCircle(sketch, "E1.21.13.0", {"center": v(-152.47, 124.38) * mm, "radius": 0.5 * mm});
            skCircle(sketch, "E1.21.14.0", {"center": v(-152.47, 126.92) * mm, "radius": 0.5 * mm});
            skCircle(sketch, "E1.21.15.0", {"center": v(-152.47, 129.46) * mm, "radius": 0.5 * mm});
            skCircle(sketch, "E1.21.16.0", {"center": v(-152.47, 132) * mm, "radius": 0.5 * mm});
            skCircle(sketch, "E1.21.17.0", {"center": v(-152.47, 134.54) * mm, "radius": 0.5 * mm});
            skCircle(sketch, "E1.21.18.0", {"center": v(-152.47, 137.08) * mm, "radius": 0.5 * mm});
            skCircle(sketch, "E1.21.19.0", {"center": v(-152.47, 139.62) * mm, "radius": 0.5 * mm});
            skCircle(sketch, "E1.21.20.0", {"center": v(-152.47, 142.16) * mm, "radius": 0.5 * mm});
            skCircle(sketch, "E1.21.21.0", {"center": v(-152.47, 144.7) * mm, "radius": 0.5 * mm});
            skCircle(sketch, "E1.21.22.0", {"center": v(-152.47, 147.24) * mm, "radius": 0.5 * mm});
            skCircle(sketch, "E1.21.23.0", {"center": v(-152.47, 149.78) * mm, "radius": 0.5 * mm});
            skCircle(sketch, "E1.21.24.0", {"center": v(-152.47, 152.32) * mm, "radius": 0.5 * mm});
            skCircle(sketch, "E1.21.25.0", {"center": v(-152.47, 154.86) * mm, "radius": 0.5 * mm});
            skCircle(sketch, "E1.21.26.0", {"center": v(-152.47, 157.4) * mm, "radius": 0.5 * mm});
            skCircle(sketch, "E1.21.27.0", {"center": v(-152.47, 159.94) * mm, "radius": 0.5 * mm});
            skCircle(sketch, "E1.21.28.0", {"center": v(-152.47, 162.48) * mm, "radius": 0.5 * mm});
            skCircle(sketch, "E1.21.29.0", {"center": v(-152.47, 165.02) * mm, "radius": 0.5 * mm});
            skCircle(sketch, "E1.21.30.0", {"center": v(-152.47, 167.56) * mm, "radius": 0.5 * mm});
            skCircle(sketch, "E1.21.31.0", {"center": v(-152.47, 170.1) * mm, "radius": 0.5 * mm});
            skCircle(sketch, "E1.21.32.0", {"center": v(-152.47, 172.64) * mm, "radius": 0.5 * mm});
            skCircle(sketch, "E1.21.33.0", {"center": v(-152.47, 175.18) * mm, "radius": 0.5 * mm});
            skCircle(sketch, "E1.21.34.0", {"center": v(-152.47, 177.72) * mm, "radius": 0.5 * mm});
            skCircle(sketch, "E1.21.35.0", {"center": v(-152.47, 180.26) * mm, "radius": 0.5 * mm});
            skCircle(sketch, "E1.21.36.0", {"center": v(-152.47, 182.8) * mm, "radius": 0.5 * mm});
            skCircle(sketch, "E1.21.37.0", {"center": v(-152.47, 185.34) * mm, "radius": 0.5 * mm});
            skCircle(sketch, "E1.22.0.0", {"center": v(-149.93, 91.36) * mm, "radius": 0.5 * mm});
            skCircle(sketch, "E1.22.1.0", {"center": v(-149.93, 93.9) * mm, "radius": 0.5 * mm});
            skCircle(sketch, "E1.22.2.0", {"center": v(-149.93, 96.44) * mm, "radius": 0.5 * mm});
            skCircle(sketch, "E1.22.3.0", {"center": v(-149.93, 98.98) * mm, "radius": 0.5 * mm});
            skCircle(sketch, "E1.22.4.0", {"center": v(-149.93, 101.52) * mm, "radius": 0.5 * mm});
            skCircle(sketch, "E1.22.5.0", {"center": v(-149.93, 104.06) * mm, "radius": 0.5 * mm});
            skCircle(sketch, "E1.22.6.0", {"center": v(-149.93, 106.6) * mm, "radius": 0.5 * mm});
            skCircle(sketch, "E1.22.7.0", {"center": v(-149.93, 109.14) * mm, "radius": 0.5 * mm});
            skCircle(sketch, "E1.22.8.0", {"center": v(-149.93, 111.68) * mm, "radius": 0.5 * mm});
            skCircle(sketch, "E1.22.9.0", {"center": v(-149.93, 114.22) * mm, "radius": 0.5 * mm});
            skCircle(sketch, "E1.22.10.0", {"center": v(-149.93, 116.76) * mm, "radius": 0.5 * mm});
            skCircle(sketch, "E1.22.11.0", {"center": v(-149.93, 119.3) * mm, "radius": 0.5 * mm});
            skCircle(sketch, "E1.22.12.0", {"center": v(-149.93, 121.84) * mm, "radius": 0.5 * mm});
            skCircle(sketch, "E1.22.13.0", {"center": v(-149.93, 124.38) * mm, "radius": 0.5 * mm});
            skCircle(sketch, "E1.22.14.0", {"center": v(-149.93, 126.92) * mm, "radius": 0.5 * mm});
            skCircle(sketch, "E1.22.15.0", {"center": v(-149.93, 129.46) * mm, "radius": 0.5 * mm});
            skCircle(sketch, "E1.22.16.0", {"center": v(-149.93, 132) * mm, "radius": 0.5 * mm});
            skCircle(sketch, "E1.22.17.0", {"center": v(-149.93, 134.54) * mm, "radius": 0.5 * mm});
            skCircle(sketch, "E1.22.18.0", {"center": v(-149.93, 137.08) * mm, "radius": 0.5 * mm});
            skCircle(sketch, "E1.22.19.0", {"center": v(-149.93, 139.62) * mm, "radius": 0.5 * mm});
            skCircle(sketch, "E1.22.20.0", {"center": v(-149.93, 142.16) * mm, "radius": 0.5 * mm});
            skCircle(sketch, "E1.22.21.0", {"center": v(-149.93, 144.7) * mm, "radius": 0.5 * mm});
            skCircle(sketch, "E1.22.22.0", {"center": v(-149.93, 147.24) * mm, "radius": 0.5 * mm});
            skCircle(sketch, "E1.22.23.0", {"center": v(-149.93, 149.78) * mm, "radius": 0.5 * mm});
            skCircle(sketch, "E1.22.24.0", {"center": v(-149.93, 152.32) * mm, "radius": 0.5 * mm});
            skCircle(sketch, "E1.22.25.0", {"center": v(-149.93, 154.86) * mm, "radius": 0.5 * mm});
            skCircle(sketch, "E1.22.26.0", {"center": v(-149.93, 157.4) * mm, "radius": 0.5 * mm});
            skCircle(sketch, "E1.22.27.0", {"center": v(-149.93, 159.94) * mm, "radius": 0.5 * mm});
            skCircle(sketch, "E1.22.28.0", {"center": v(-149.93, 162.48) * mm, "radius": 0.5 * mm});
            skCircle(sketch, "E1.22.29.0", {"center": v(-149.93, 165.02) * mm, "radius": 0.5 * mm});
            skCircle(sketch, "E1.22.30.0", {"center": v(-149.93, 167.56) * mm, "radius": 0.5 * mm});
            skCircle(sketch, "E1.22.31.0", {"center": v(-149.93, 170.1) * mm, "radius": 0.5 * mm});
            skCircle(sketch, "E1.22.32.0", {"center": v(-149.93, 172.64) * mm, "radius": 0.5 * mm});
            skCircle(sketch, "E1.22.33.0", {"center": v(-149.93, 175.18) * mm, "radius": 0.5 * mm});
            skCircle(sketch, "E1.22.34.0", {"center": v(-149.93, 177.72) * mm, "radius": 0.5 * mm});
            skCircle(sketch, "E1.22.35.0", {"center": v(-149.93, 180.26) * mm, "radius": 0.5 * mm});
            skCircle(sketch, "E1.22.36.0", {"center": v(-149.93, 182.8) * mm, "radius": 0.5 * mm});
            skCircle(sketch, "E1.22.37.0", {"center": v(-149.93, 185.34) * mm, "radius": 0.5 * mm});
            skCircle(sketch, "E1.23.0.0", {"center": v(-147.39, 91.36) * mm, "radius": 0.5 * mm});
            skCircle(sketch, "E1.23.1.0", {"center": v(-147.39, 93.9) * mm, "radius": 0.5 * mm});
            skCircle(sketch, "E1.23.2.0", {"center": v(-147.39, 96.44) * mm, "radius": 0.5 * mm});
            skCircle(sketch, "E1.23.3.0", {"center": v(-147.39, 98.98) * mm, "radius": 0.5 * mm});
            skCircle(sketch, "E1.23.4.0", {"center": v(-147.39, 101.52) * mm, "radius": 0.5 * mm});
            skCircle(sketch, "E1.23.5.0", {"center": v(-147.39, 104.06) * mm, "radius": 0.5 * mm});
            skCircle(sketch, "E1.23.6.0", {"center": v(-147.39, 106.6) * mm, "radius": 0.5 * mm});
            skCircle(sketch, "E1.23.7.0", {"center": v(-147.39, 109.14) * mm, "radius": 0.5 * mm});
            skCircle(sketch, "E1.23.8.0", {"center": v(-147.39, 111.68) * mm, "radius": 0.5 * mm});
            skCircle(sketch, "E1.23.9.0", {"center": v(-147.39, 114.22) * mm, "radius": 0.5 * mm});
            skCircle(sketch, "E1.23.10.0", {"center": v(-147.39, 116.76) * mm, "radius": 0.5 * mm});
            skCircle(sketch, "E1.23.11.0", {"center": v(-147.39, 119.3) * mm, "radius": 0.5 * mm});
            skCircle(sketch, "E1.23.12.0", {"center": v(-147.39, 121.84) * mm, "radius": 0.5 * mm});
            skCircle(sketch, "E1.23.13.0", {"center": v(-147.39, 124.38) * mm, "radius": 0.5 * mm});
            skCircle(sketch, "E1.23.14.0", {"center": v(-147.39, 126.92) * mm, "radius": 0.5 * mm});
            skCircle(sketch, "E1.23.15.0", {"center": v(-147.39, 129.46) * mm, "radius": 0.5 * mm});
            skCircle(sketch, "E1.23.16.0", {"center": v(-147.39, 132) * mm, "radius": 0.5 * mm});
            skCircle(sketch, "E1.23.17.0", {"center": v(-147.39, 134.54) * mm, "radius": 0.5 * mm});
            skCircle(sketch, "E1.23.18.0", {"center": v(-147.39, 137.08) * mm, "radius": 0.5 * mm});
            skCircle(sketch, "E1.23.19.0", {"center": v(-147.39, 139.62) * mm, "radius": 0.5 * mm});
            skCircle(sketch, "E1.23.20.0", {"center": v(-147.39, 142.16) * mm, "radius": 0.5 * mm});
            skCircle(sketch, "E1.23.21.0", {"center": v(-147.39, 144.7) * mm, "radius": 0.5 * mm});
            skCircle(sketch, "E1.23.22.0", {"center": v(-147.39, 147.24) * mm, "radius": 0.5 * mm});
            skCircle(sketch, "E1.23.23.0", {"center": v(-147.39, 149.78) * mm, "radius": 0.5 * mm});
            skCircle(sketch, "E1.23.24.0", {"center": v(-147.39, 152.32) * mm, "radius": 0.5 * mm});
            skCircle(sketch, "E1.23.25.0", {"center": v(-147.39, 154.86) * mm, "radius": 0.5 * mm});
            skCircle(sketch, "E1.23.26.0", {"center": v(-147.39, 157.4) * mm, "radius": 0.5 * mm});
            skCircle(sketch, "E1.23.27.0", {"center": v(-147.39, 159.94) * mm, "radius": 0.5 * mm});
            skCircle(sketch, "E1.23.28.0", {"center": v(-147.39, 162.48) * mm, "radius": 0.5 * mm});
            skCircle(sketch, "E1.23.29.0", {"center": v(-147.39, 165.02) * mm, "radius": 0.5 * mm});
            skCircle(sketch, "E1.23.30.0", {"center": v(-147.39, 167.56) * mm, "radius": 0.5 * mm});
            skCircle(sketch, "E1.23.31.0", {"center": v(-147.39, 170.1) * mm, "radius": 0.5 * mm});
            skCircle(sketch, "E1.23.32.0", {"center": v(-147.39, 172.64) * mm, "radius": 0.5 * mm});
            skCircle(sketch, "E1.23.33.0", {"center": v(-147.39, 175.18) * mm, "radius": 0.5 * mm});
            skCircle(sketch, "E1.23.34.0", {"center": v(-147.39, 177.72) * mm, "radius": 0.5 * mm});
            skCircle(sketch, "E1.23.35.0", {"center": v(-147.39, 180.26) * mm, "radius": 0.5 * mm});
            skCircle(sketch, "E1.23.36.0", {"center": v(-147.39, 182.8) * mm, "radius": 0.5 * mm});
            skCircle(sketch, "E1.23.37.0", {"center": v(-147.39, 185.34) * mm, "radius": 0.5 * mm});
            skCircle(sketch, "E1.24.0.0", {"center": v(-144.85, 91.36) * mm, "radius": 0.5 * mm});
            skCircle(sketch, "E1.24.1.0", {"center": v(-144.85, 93.9) * mm, "radius": 0.5 * mm});
            skCircle(sketch, "E1.24.2.0", {"center": v(-144.85, 96.44) * mm, "radius": 0.5 * mm});
            skCircle(sketch, "E1.24.3.0", {"center": v(-144.85, 98.98) * mm, "radius": 0.5 * mm});
            skCircle(sketch, "E1.24.4.0", {"center": v(-144.85, 101.52) * mm, "radius": 0.5 * mm});
            skCircle(sketch, "E1.24.5.0", {"center": v(-144.85, 104.06) * mm, "radius": 0.5 * mm});
            skCircle(sketch, "E1.24.6.0", {"center": v(-144.85, 106.6) * mm, "radius": 0.5 * mm});
            skCircle(sketch, "E1.24.7.0", {"center": v(-144.85, 109.14) * mm, "radius": 0.5 * mm});
            skCircle(sketch, "E1.24.8.0", {"center": v(-144.85, 111.68) * mm, "radius": 0.5 * mm});
            skCircle(sketch, "E1.24.9.0", {"center": v(-144.85, 114.22) * mm, "radius": 0.5 * mm});
            skCircle(sketch, "E1.24.10.0", {"center": v(-144.85, 116.76) * mm, "radius": 0.5 * mm});
            skCircle(sketch, "E1.24.11.0", {"center": v(-144.85, 119.3) * mm, "radius": 0.5 * mm});
            skCircle(sketch, "E1.24.12.0", {"center": v(-144.85, 121.84) * mm, "radius": 0.5 * mm});
            skCircle(sketch, "E1.24.13.0", {"center": v(-144.85, 124.38) * mm, "radius": 0.5 * mm});
            skCircle(sketch, "E1.24.14.0", {"center": v(-144.85, 126.92) * mm, "radius": 0.5 * mm});
            skCircle(sketch, "E1.24.15.0", {"center": v(-144.85, 129.46) * mm, "radius": 0.5 * mm});
            skCircle(sketch, "E1.24.16.0", {"center": v(-144.85, 132) * mm, "radius": 0.5 * mm});
            skCircle(sketch, "E1.24.17.0", {"center": v(-144.85, 134.54) * mm, "radius": 0.5 * mm});
            skCircle(sketch, "E1.24.18.0", {"center": v(-144.85, 137.08) * mm, "radius": 0.5 * mm});
            skCircle(sketch, "E1.24.19.0", {"center": v(-144.85, 139.62) * mm, "radius": 0.5 * mm});
            skCircle(sketch, "E1.24.20.0", {"center": v(-144.85, 142.16) * mm, "radius": 0.5 * mm});
            skCircle(sketch, "E1.24.21.0", {"center": v(-144.85, 144.7) * mm, "radius": 0.5 * mm});
            skCircle(sketch, "E1.24.22.0", {"center": v(-144.85, 147.24) * mm, "radius": 0.5 * mm});
            skCircle(sketch, "E1.24.23.0", {"center": v(-144.85, 149.78) * mm, "radius": 0.5 * mm});
            skCircle(sketch, "E1.24.24.0", {"center": v(-144.85, 152.32) * mm, "radius": 0.5 * mm});
            skCircle(sketch, "E1.24.25.0", {"center": v(-144.85, 154.86) * mm, "radius": 0.5 * mm});
            skCircle(sketch, "E1.24.26.0", {"center": v(-144.85, 157.4) * mm, "radius": 0.5 * mm});
            skCircle(sketch, "E1.24.27.0", {"center": v(-144.85, 159.94) * mm, "radius": 0.5 * mm});
            skCircle(sketch, "E1.24.28.0", {"center": v(-144.85, 162.48) * mm, "radius": 0.5 * mm});
            skCircle(sketch, "E1.24.29.0", {"center": v(-144.85, 165.02) * mm, "radius": 0.5 * mm});
            skCircle(sketch, "E1.24.30.0", {"center": v(-144.85, 167.56) * mm, "radius": 0.5 * mm});
            skCircle(sketch, "E1.24.31.0", {"center": v(-144.85, 170.1) * mm, "radius": 0.5 * mm});
            skCircle(sketch, "E1.24.32.0", {"center": v(-144.85, 172.64) * mm, "radius": 0.5 * mm});
            skCircle(sketch, "E1.24.33.0", {"center": v(-144.85, 175.18) * mm, "radius": 0.5 * mm});
            skCircle(sketch, "E1.24.34.0", {"center": v(-144.85, 177.72) * mm, "radius": 0.5 * mm});
            skCircle(sketch, "E1.24.35.0", {"center": v(-144.85, 180.26) * mm, "radius": 0.5 * mm});
            skCircle(sketch, "E1.24.36.0", {"center": v(-144.85, 182.8) * mm, "radius": 0.5 * mm});
            skCircle(sketch, "E1.24.37.0", {"center": v(-144.85, 185.34) * mm, "radius": 0.5 * mm});
            skCircle(sketch, "E1.25.0.0", {"center": v(-142.3, 91.36) * mm, "radius": 0.5 * mm});
            skCircle(sketch, "E1.25.1.0", {"center": v(-142.3, 93.9) * mm, "radius": 0.5 * mm});
            skCircle(sketch, "E1.25.2.0", {"center": v(-142.3, 96.44) * mm, "radius": 0.5 * mm});
            skCircle(sketch, "E1.25.3.0", {"center": v(-142.3, 98.98) * mm, "radius": 0.5 * mm});
            skCircle(sketch, "E1.25.4.0", {"center": v(-142.3, 101.52) * mm, "radius": 0.5 * mm});
            skCircle(sketch, "E1.25.5.0", {"center": v(-142.3, 104.06) * mm, "radius": 0.5 * mm});
            skCircle(sketch, "E1.25.6.0", {"center": v(-142.3, 106.6) * mm, "radius": 0.5 * mm});
            skCircle(sketch, "E1.25.7.0", {"center": v(-142.3, 109.14) * mm, "radius": 0.5 * mm});
            skCircle(sketch, "E1.25.8.0", {"center": v(-142.3, 111.68) * mm, "radius": 0.5 * mm});
            skCircle(sketch, "E1.25.9.0", {"center": v(-142.3, 114.22) * mm, "radius": 0.5 * mm});
            skCircle(sketch, "E1.25.10.0", {"center": v(-142.3, 116.76) * mm, "radius": 0.5 * mm});
            skCircle(sketch, "E1.25.11.0", {"center": v(-142.3, 119.3) * mm, "radius": 0.5 * mm});
            skCircle(sketch, "E1.25.12.0", {"center": v(-142.3, 121.84) * mm, "radius": 0.5 * mm});
            skCircle(sketch, "E1.25.13.0", {"center": v(-142.3, 124.38) * mm, "radius": 0.5 * mm});
            skCircle(sketch, "E1.25.14.0", {"center": v(-142.3, 126.92) * mm, "radius": 0.5 * mm});
            skCircle(sketch, "E1.25.15.0", {"center": v(-142.3, 129.46) * mm, "radius": 0.5 * mm});
            skCircle(sketch, "E1.25.16.0", {"center": v(-142.3, 132) * mm, "radius": 0.5 * mm});
            skCircle(sketch, "E1.25.17.0", {"center": v(-142.3, 134.54) * mm, "radius": 0.5 * mm});
            skCircle(sketch, "E1.25.18.0", {"center": v(-142.3, 137.08) * mm, "radius": 0.5 * mm});
            skCircle(sketch, "E1.25.19.0", {"center": v(-142.3, 139.62) * mm, "radius": 0.5 * mm});
            skCircle(sketch, "E1.25.20.0", {"center": v(-142.3, 142.16) * mm, "radius": 0.5 * mm});
            skCircle(sketch, "E1.25.21.0", {"center": v(-142.3, 144.7) * mm, "radius": 0.5 * mm});
            skCircle(sketch, "E1.25.22.0", {"center": v(-142.3, 147.24) * mm, "radius": 0.5 * mm});
            skCircle(sketch, "E1.25.23.0", {"center": v(-142.3, 149.78) * mm, "radius": 0.5 * mm});
            skCircle(sketch, "E1.25.24.0", {"center": v(-142.3, 152.32) * mm, "radius": 0.5 * mm});
            skCircle(sketch, "E1.25.25.0", {"center": v(-142.3, 154.86) * mm, "radius": 0.5 * mm});
            skCircle(sketch, "E1.25.26.0", {"center": v(-142.3, 157.4) * mm, "radius": 0.5 * mm});
            skCircle(sketch, "E1.25.27.0", {"center": v(-142.3, 159.94) * mm, "radius": 0.5 * mm});
            skCircle(sketch, "E1.25.28.0", {"center": v(-142.3, 162.48) * mm, "radius": 0.5 * mm});
            skCircle(sketch, "E1.25.29.0", {"center": v(-142.3, 165.02) * mm, "radius": 0.5 * mm});
            skCircle(sketch, "E1.25.30.0", {"center": v(-142.3, 167.56) * mm, "radius": 0.5 * mm});
            skCircle(sketch, "E1.25.31.0", {"center": v(-142.3, 170.1) * mm, "radius": 0.5 * mm});
            skCircle(sketch, "E1.25.32.0", {"center": v(-142.3, 172.64) * mm, "radius": 0.5 * mm});
            skCircle(sketch, "E1.25.33.0", {"center": v(-142.3, 175.18) * mm, "radius": 0.5 * mm});
            skCircle(sketch, "E1.25.34.0", {"center": v(-142.3, 177.72) * mm, "radius": 0.5 * mm});
            skCircle(sketch, "E1.25.35.0", {"center": v(-142.3, 180.26) * mm, "radius": 0.5 * mm});
            skCircle(sketch, "E1.25.36.0", {"center": v(-142.3, 182.8) * mm, "radius": 0.5 * mm});
            skCircle(sketch, "E1.25.37.0", {"center": v(-142.3, 185.34) * mm, "radius": 0.5 * mm});
            skCircle(sketch, "E1.26.0.0", {"center": v(-139.77, 91.36) * mm, "radius": 0.5 * mm});
            skCircle(sketch, "E1.26.1.0", {"center": v(-139.77, 93.9) * mm, "radius": 0.5 * mm});
            skCircle(sketch, "E1.26.2.0", {"center": v(-139.77, 96.44) * mm, "radius": 0.5 * mm});
            skCircle(sketch, "E1.26.3.0", {"center": v(-139.77, 98.98) * mm, "radius": 0.5 * mm});
            skCircle(sketch, "E1.26.4.0", {"center": v(-139.77, 101.52) * mm, "radius": 0.5 * mm});
            skCircle(sketch, "E1.26.5.0", {"center": v(-139.77, 104.06) * mm, "radius": 0.5 * mm});
            skCircle(sketch, "E1.26.6.0", {"center": v(-139.77, 106.6) * mm, "radius": 0.5 * mm});
            skCircle(sketch, "E1.26.7.0", {"center": v(-139.77, 109.14) * mm, "radius": 0.5 * mm});
            skCircle(sketch, "E1.26.8.0", {"center": v(-139.77, 111.68) * mm, "radius": 0.5 * mm});
            skCircle(sketch, "E1.26.9.0", {"center": v(-139.77, 114.22) * mm, "radius": 0.5 * mm});
            skCircle(sketch, "E1.26.10.0", {"center": v(-139.77, 116.76) * mm, "radius": 0.5 * mm});
            skCircle(sketch, "E1.26.11.0", {"center": v(-139.77, 119.3) * mm, "radius": 0.5 * mm});
            skCircle(sketch, "E1.26.12.0", {"center": v(-139.77, 121.84) * mm, "radius": 0.5 * mm});
            skCircle(sketch, "E1.26.13.0", {"center": v(-139.77, 124.38) * mm, "radius": 0.5 * mm});
            skCircle(sketch, "E1.26.14.0", {"center": v(-139.77, 126.92) * mm, "radius": 0.5 * mm});
            skCircle(sketch, "E1.26.15.0", {"center": v(-139.77, 129.46) * mm, "radius": 0.5 * mm});
            skCircle(sketch, "E1.26.16.0", {"center": v(-139.77, 132) * mm, "radius": 0.5 * mm});
            skCircle(sketch, "E1.26.17.0", {"center": v(-139.77, 134.54) * mm, "radius": 0.5 * mm});
            skCircle(sketch, "E1.26.18.0", {"center": v(-139.77, 137.08) * mm, "radius": 0.5 * mm});
            skCircle(sketch, "E1.26.19.0", {"center": v(-139.77, 139.62) * mm, "radius": 0.5 * mm});
            skCircle(sketch, "E1.26.20.0", {"center": v(-139.77, 142.16) * mm, "radius": 0.5 * mm});
            skCircle(sketch, "E1.26.21.0", {"center": v(-139.77, 144.7) * mm, "radius": 0.5 * mm});
            skCircle(sketch, "E1.26.22.0", {"center": v(-139.77, 147.24) * mm, "radius": 0.5 * mm});
            skCircle(sketch, "E1.26.23.0", {"center": v(-139.77, 149.78) * mm, "radius": 0.5 * mm});
            skCircle(sketch, "E1.26.24.0", {"center": v(-139.77, 152.32) * mm, "radius": 0.5 * mm});
            skCircle(sketch, "E1.26.25.0", {"center": v(-139.77, 154.86) * mm, "radius": 0.5 * mm});
            skCircle(sketch, "E1.26.26.0", {"center": v(-139.77, 157.4) * mm, "radius": 0.5 * mm});
            skCircle(sketch, "E1.26.27.0", {"center": v(-139.77, 159.94) * mm, "radius": 0.5 * mm});
            skCircle(sketch, "E1.26.28.0", {"center": v(-139.77, 162.48) * mm, "radius": 0.5 * mm});
            skCircle(sketch, "E1.26.29.0", {"center": v(-139.77, 165.02) * mm, "radius": 0.5 * mm});
            skCircle(sketch, "E1.26.30.0", {"center": v(-139.77, 167.56) * mm, "radius": 0.5 * mm});
            skCircle(sketch, "E1.26.31.0", {"center": v(-139.77, 170.1) * mm, "radius": 0.5 * mm});
            skCircle(sketch, "E1.26.32.0", {"center": v(-139.77, 172.64) * mm, "radius": 0.5 * mm});
            skCircle(sketch, "E1.26.33.0", {"center": v(-139.77, 175.18) * mm, "radius": 0.5 * mm});
            skCircle(sketch, "E1.26.34.0", {"center": v(-139.77, 177.72) * mm, "radius": 0.5 * mm});
            skCircle(sketch, "E1.26.35.0", {"center": v(-139.77, 180.26) * mm, "radius": 0.5 * mm});
            skCircle(sketch, "E1.26.36.0", {"center": v(-139.77, 182.8) * mm, "radius": 0.5 * mm});
            skCircle(sketch, "E1.26.37.0", {"center": v(-139.77, 185.34) * mm, "radius": 0.5 * mm});
            skCircle(sketch, "E1.27.0.0", {"center": v(-137.23, 91.36) * mm, "radius": 0.5 * mm});
            skCircle(sketch, "E1.27.1.0", {"center": v(-137.23, 93.9) * mm, "radius": 0.5 * mm});
            skCircle(sketch, "E1.27.2.0", {"center": v(-137.23, 96.44) * mm, "radius": 0.5 * mm});
            skCircle(sketch, "E1.27.3.0", {"center": v(-137.23, 98.98) * mm, "radius": 0.5 * mm});
            skCircle(sketch, "E1.27.4.0", {"center": v(-137.23, 101.52) * mm, "radius": 0.5 * mm});
            skCircle(sketch, "E1.27.5.0", {"center": v(-137.23, 104.06) * mm, "radius": 0.5 * mm});
            skCircle(sketch, "E1.27.6.0", {"center": v(-137.23, 106.6) * mm, "radius": 0.5 * mm});
            skCircle(sketch, "E1.27.7.0", {"center": v(-137.23, 109.14) * mm, "radius": 0.5 * mm});
            skCircle(sketch, "E1.27.8.0", {"center": v(-137.23, 111.68) * mm, "radius": 0.5 * mm});
            skCircle(sketch, "E1.27.9.0", {"center": v(-137.23, 114.22) * mm, "radius": 0.5 * mm});
            skCircle(sketch, "E1.27.10.0", {"center": v(-137.23, 116.76) * mm, "radius": 0.5 * mm});
            skCircle(sketch, "E1.27.11.0", {"center": v(-137.23, 119.3) * mm, "radius": 0.5 * mm});
            skCircle(sketch, "E1.27.12.0", {"center": v(-137.23, 121.84) * mm, "radius": 0.5 * mm});
            skCircle(sketch, "E1.27.13.0", {"center": v(-137.23, 124.38) * mm, "radius": 0.5 * mm});
            skCircle(sketch, "E1.27.14.0", {"center": v(-137.23, 126.92) * mm, "radius": 0.5 * mm});
            skCircle(sketch, "E1.27.15.0", {"center": v(-137.23, 129.46) * mm, "radius": 0.5 * mm});
            skCircle(sketch, "E1.27.16.0", {"center": v(-137.23, 132) * mm, "radius": 0.5 * mm});
            skCircle(sketch, "E1.27.17.0", {"center": v(-137.23, 134.54) * mm, "radius": 0.5 * mm});
            skCircle(sketch, "E1.27.18.0", {"center": v(-137.23, 137.08) * mm, "radius": 0.5 * mm});
            skCircle(sketch, "E1.27.19.0", {"center": v(-137.23, 139.62) * mm, "radius": 0.5 * mm});
            skCircle(sketch, "E1.27.20.0", {"center": v(-137.23, 142.16) * mm, "radius": 0.5 * mm});
            skCircle(sketch, "E1.27.21.0", {"center": v(-137.23, 144.7) * mm, "radius": 0.5 * mm});
            skCircle(sketch, "E1.27.22.0", {"center": v(-137.23, 147.24) * mm, "radius": 0.5 * mm});
            skCircle(sketch, "E1.27.23.0", {"center": v(-137.23, 149.78) * mm, "radius": 0.5 * mm});
            skCircle(sketch, "E1.27.24.0", {"center": v(-137.23, 152.32) * mm, "radius": 0.5 * mm});
            skCircle(sketch, "E1.27.25.0", {"center": v(-137.23, 154.86) * mm, "radius": 0.5 * mm});
            skCircle(sketch, "E1.27.26.0", {"center": v(-137.23, 157.4) * mm, "radius": 0.5 * mm});
            skCircle(sketch, "E1.27.27.0", {"center": v(-137.23, 159.94) * mm, "radius": 0.5 * mm});
            skCircle(sketch, "E1.27.28.0", {"center": v(-137.23, 162.48) * mm, "radius": 0.5 * mm});
            skCircle(sketch, "E1.27.29.0", {"center": v(-137.23, 165.02) * mm, "radius": 0.5 * mm});
            skCircle(sketch, "E1.27.30.0", {"center": v(-137.23, 167.56) * mm, "radius": 0.5 * mm});
            skCircle(sketch, "E1.27.31.0", {"center": v(-137.23, 170.1) * mm, "radius": 0.5 * mm});
            skCircle(sketch, "E1.27.32.0", {"center": v(-137.23, 172.64) * mm, "radius": 0.5 * mm});
            skCircle(sketch, "E1.27.33.0", {"center": v(-137.23, 175.18) * mm, "radius": 0.5 * mm});
            skCircle(sketch, "E1.27.34.0", {"center": v(-137.23, 177.72) * mm, "radius": 0.5 * mm});
            skCircle(sketch, "E1.27.35.0", {"center": v(-137.23, 180.26) * mm, "radius": 0.5 * mm});
            skCircle(sketch, "E1.27.36.0", {"center": v(-137.23, 182.8) * mm, "radius": 0.5 * mm});
            skCircle(sketch, "E1.27.37.0", {"center": v(-137.23, 185.34) * mm, "radius": 0.5 * mm});
            skCircle(sketch, "E1.28.0.0", {"center": v(-134.69, 91.36) * mm, "radius": 0.5 * mm});
            skCircle(sketch, "E1.28.1.0", {"center": v(-134.69, 93.9) * mm, "radius": 0.5 * mm});
            skCircle(sketch, "E1.28.2.0", {"center": v(-134.69, 96.44) * mm, "radius": 0.5 * mm});
            skCircle(sketch, "E1.28.3.0", {"center": v(-134.69, 98.98) * mm, "radius": 0.5 * mm});
            skCircle(sketch, "E1.28.4.0", {"center": v(-134.69, 101.52) * mm, "radius": 0.5 * mm});
            skCircle(sketch, "E1.28.5.0", {"center": v(-134.69, 104.06) * mm, "radius": 0.5 * mm});
            skCircle(sketch, "E1.28.6.0", {"center": v(-134.69, 106.6) * mm, "radius": 0.5 * mm});
            skCircle(sketch, "E1.28.7.0", {"center": v(-134.69, 109.14) * mm, "radius": 0.5 * mm});
            skCircle(sketch, "E1.28.8.0", {"center": v(-134.69, 111.68) * mm, "radius": 0.5 * mm});
            skCircle(sketch, "E1.28.9.0", {"center": v(-134.69, 114.22) * mm, "radius": 0.5 * mm});
            skCircle(sketch, "E1.28.10.0", {"center": v(-134.69, 116.76) * mm, "radius": 0.5 * mm});
            skCircle(sketch, "E1.28.11.0", {"center": v(-134.69, 119.3) * mm, "radius": 0.5 * mm});
            skCircle(sketch, "E1.28.12.0", {"center": v(-134.69, 121.84) * mm, "radius": 0.5 * mm});
            skCircle(sketch, "E1.28.13.0", {"center": v(-134.69, 124.38) * mm, "radius": 0.5 * mm});
            skCircle(sketch, "E1.28.14.0", {"center": v(-134.69, 126.92) * mm, "radius": 0.5 * mm});
            skCircle(sketch, "E1.28.15.0", {"center": v(-134.69, 129.46) * mm, "radius": 0.5 * mm});
            skCircle(sketch, "E1.28.16.0", {"center": v(-134.69, 132) * mm, "radius": 0.5 * mm});
            skCircle(sketch, "E1.28.17.0", {"center": v(-134.69, 134.54) * mm, "radius": 0.5 * mm});
            skCircle(sketch, "E1.28.18.0", {"center": v(-134.69, 137.08) * mm, "radius": 0.5 * mm});
            skCircle(sketch, "E1.28.19.0", {"center": v(-134.69, 139.62) * mm, "radius": 0.5 * mm});
            skCircle(sketch, "E1.28.20.0", {"center": v(-134.69, 142.16) * mm, "radius": 0.5 * mm});
            skCircle(sketch, "E1.28.21.0", {"center": v(-134.69, 144.7) * mm, "radius": 0.5 * mm});
            skCircle(sketch, "E1.28.22.0", {"center": v(-134.69, 147.24) * mm, "radius": 0.5 * mm});
            skCircle(sketch, "E1.28.23.0", {"center": v(-134.69, 149.78) * mm, "radius": 0.5 * mm});
            skCircle(sketch, "E1.28.24.0", {"center": v(-134.69, 152.32) * mm, "radius": 0.5 * mm});
            skCircle(sketch, "E1.28.25.0", {"center": v(-134.69, 154.86) * mm, "radius": 0.5 * mm});
            skCircle(sketch, "E1.28.26.0", {"center": v(-134.69, 157.4) * mm, "radius": 0.5 * mm});
            skCircle(sketch, "E1.28.27.0", {"center": v(-134.69, 159.94) * mm, "radius": 0.5 * mm});
            skCircle(sketch, "E1.28.28.0", {"center": v(-134.69, 162.48) * mm, "radius": 0.5 * mm});
            skCircle(sketch, "E1.28.29.0", {"center": v(-134.69, 165.02) * mm, "radius": 0.5 * mm});
            skCircle(sketch, "E1.28.30.0", {"center": v(-134.69, 167.56) * mm, "radius": 0.5 * mm});
            skCircle(sketch, "E1.28.31.0", {"center": v(-134.69, 170.1) * mm, "radius": 0.5 * mm});
            skCircle(sketch, "E1.28.32.0", {"center": v(-134.69, 172.64) * mm, "radius": 0.5 * mm});
            skCircle(sketch, "E1.28.33.0", {"center": v(-134.69, 175.18) * mm, "radius": 0.5 * mm});
            skCircle(sketch, "E1.28.34.0", {"center": v(-134.69, 177.72) * mm, "radius": 0.5 * mm});
            skCircle(sketch, "E1.28.35.0", {"center": v(-134.69, 180.26) * mm, "radius": 0.5 * mm});
            skCircle(sketch, "E1.28.36.0", {"center": v(-134.69, 182.8) * mm, "radius": 0.5 * mm});
            skCircle(sketch, "E1.28.37.0", {"center": v(-134.69, 185.34) * mm, "radius": 0.5 * mm});
            skCircle(sketch, "E1.29.0.0", {"center": v(-132.15, 91.36) * mm, "radius": 0.5 * mm});
            skCircle(sketch, "E1.29.1.0", {"center": v(-132.15, 93.9) * mm, "radius": 0.5 * mm});
            skCircle(sketch, "E1.29.2.0", {"center": v(-132.15, 96.44) * mm, "radius": 0.5 * mm});
            skCircle(sketch, "E1.29.3.0", {"center": v(-132.15, 98.98) * mm, "radius": 0.5 * mm});
            skCircle(sketch, "E1.29.4.0", {"center": v(-132.15, 101.52) * mm, "radius": 0.5 * mm});
            skCircle(sketch, "E1.29.5.0", {"center": v(-132.15, 104.06) * mm, "radius": 0.5 * mm});
            skCircle(sketch, "E1.29.6.0", {"center": v(-132.15, 106.6) * mm, "radius": 0.5 * mm});
            skCircle(sketch, "E1.29.7.0", {"center": v(-132.15, 109.14) * mm, "radius": 0.5 * mm});
            skCircle(sketch, "E1.29.8.0", {"center": v(-132.15, 111.68) * mm, "radius": 0.5 * mm});
            skCircle(sketch, "E1.29.9.0", {"center": v(-132.15, 114.22) * mm, "radius": 0.5 * mm});
            skCircle(sketch, "E1.29.10.0", {"center": v(-132.15, 116.76) * mm, "radius": 0.5 * mm});
            skCircle(sketch, "E1.29.11.0", {"center": v(-132.15, 119.3) * mm, "radius": 0.5 * mm});
            skCircle(sketch, "E1.29.12.0", {"center": v(-132.15, 121.84) * mm, "radius": 0.5 * mm});
            skCircle(sketch, "E1.29.13.0", {"center": v(-132.15, 124.38) * mm, "radius": 0.5 * mm});
            skCircle(sketch, "E1.29.14.0", {"center": v(-132.15, 126.92) * mm, "radius": 0.5 * mm});
            skCircle(sketch, "E1.29.15.0", {"center": v(-132.15, 129.46) * mm, "radius": 0.5 * mm});
            skCircle(sketch, "E1.29.16.0", {"center": v(-132.15, 132) * mm, "radius": 0.5 * mm});
            skCircle(sketch, "E1.29.17.0", {"center": v(-132.15, 134.54) * mm, "radius": 0.5 * mm});
            skCircle(sketch, "E1.29.18.0", {"center": v(-132.15, 137.08) * mm, "radius": 0.5 * mm});
            skCircle(sketch, "E1.29.19.0", {"center": v(-132.15, 139.62) * mm, "radius": 0.5 * mm});
            skCircle(sketch, "E1.29.20.0", {"center": v(-132.15, 142.16) * mm, "radius": 0.5 * mm});
            skCircle(sketch, "E1.29.21.0", {"center": v(-132.15, 144.7) * mm, "radius": 0.5 * mm});
            skCircle(sketch, "E1.29.22.0", {"center": v(-132.15, 147.24) * mm, "radius": 0.5 * mm});
            skCircle(sketch, "E1.29.23.0", {"center": v(-132.15, 149.78) * mm, "radius": 0.5 * mm});
            skCircle(sketch, "E1.29.24.0", {"center": v(-132.15, 152.32) * mm, "radius": 0.5 * mm});
            skCircle(sketch, "E1.29.25.0", {"center": v(-132.15, 154.86) * mm, "radius": 0.5 * mm});
            skCircle(sketch, "E1.29.26.0", {"center": v(-132.15, 157.4) * mm, "radius": 0.5 * mm});
            skCircle(sketch, "E1.29.27.0", {"center": v(-132.15, 159.94) * mm, "radius": 0.5 * mm});
            skCircle(sketch, "E1.29.28.0", {"center": v(-132.15, 162.48) * mm, "radius": 0.5 * mm});
            skCircle(sketch, "E1.29.29.0", {"center": v(-132.15, 165.02) * mm, "radius": 0.5 * mm});
            skCircle(sketch, "E1.29.30.0", {"center": v(-132.15, 167.56) * mm, "radius": 0.5 * mm});
            skCircle(sketch, "E1.29.31.0", {"center": v(-132.15, 170.1) * mm, "radius": 0.5 * mm});
            skCircle(sketch, "E1.29.32.0", {"center": v(-132.15, 172.64) * mm, "radius": 0.5 * mm});
            skCircle(sketch, "E1.29.33.0", {"center": v(-132.15, 175.18) * mm, "radius": 0.5 * mm});
            skCircle(sketch, "E1.29.34.0", {"center": v(-132.15, 177.72) * mm, "radius": 0.5 * mm});
            skCircle(sketch, "E1.29.35.0", {"center": v(-132.15, 180.26) * mm, "radius": 0.5 * mm});
            skCircle(sketch, "E1.29.36.0", {"center": v(-132.15, 182.8) * mm, "radius": 0.5 * mm});
            skCircle(sketch, "E1.29.37.0", {"center": v(-132.15, 185.34) * mm, "radius": 0.5 * mm});
            skCircle(sketch, "E1.30.0.0", {"center": v(-129.6, 91.36) * mm, "radius": 0.5 * mm});
            skCircle(sketch, "E1.30.1.0", {"center": v(-129.6, 93.9) * mm, "radius": 0.5 * mm});
            skCircle(sketch, "E1.30.2.0", {"center": v(-129.6, 96.44) * mm, "radius": 0.5 * mm});
            skCircle(sketch, "E1.30.3.0", {"center": v(-129.6, 98.98) * mm, "radius": 0.5 * mm});
            skCircle(sketch, "E1.30.4.0", {"center": v(-129.6, 101.52) * mm, "radius": 0.5 * mm});
            skCircle(sketch, "E1.30.5.0", {"center": v(-129.6, 104.06) * mm, "radius": 0.5 * mm});
            skCircle(sketch, "E1.30.6.0", {"center": v(-129.6, 106.6) * mm, "radius": 0.5 * mm});
            skCircle(sketch, "E1.30.7.0", {"center": v(-129.6, 109.14) * mm, "radius": 0.5 * mm});
            skCircle(sketch, "E1.30.8.0", {"center": v(-129.6, 111.68) * mm, "radius": 0.5 * mm});
            skCircle(sketch, "E1.30.9.0", {"center": v(-129.6, 114.22) * mm, "radius": 0.5 * mm});
            skCircle(sketch, "E1.30.10.0", {"center": v(-129.6, 116.76) * mm, "radius": 0.5 * mm});
            skCircle(sketch, "E1.30.11.0", {"center": v(-129.6, 119.3) * mm, "radius": 0.5 * mm});
            skCircle(sketch, "E1.30.12.0", {"center": v(-129.6, 121.84) * mm, "radius": 0.5 * mm});
            skCircle(sketch, "E1.30.13.0", {"center": v(-129.6, 124.38) * mm, "radius": 0.5 * mm});
            skCircle(sketch, "E1.30.14.0", {"center": v(-129.6, 126.92) * mm, "radius": 0.5 * mm});
            skCircle(sketch, "E1.30.15.0", {"center": v(-129.6, 129.46) * mm, "radius": 0.5 * mm});
            skCircle(sketch, "E1.30.16.0", {"center": v(-129.6, 132) * mm, "radius": 0.5 * mm});
            skCircle(sketch, "E1.30.17.0", {"center": v(-129.6, 134.54) * mm, "radius": 0.5 * mm});
            skCircle(sketch, "E1.30.18.0", {"center": v(-129.6, 137.08) * mm, "radius": 0.5 * mm});
            skCircle(sketch, "E1.30.19.0", {"center": v(-129.6, 139.62) * mm, "radius": 0.5 * mm});
            skCircle(sketch, "E1.30.20.0", {"center": v(-129.6, 142.16) * mm, "radius": 0.5 * mm});
            skCircle(sketch, "E1.30.21.0", {"center": v(-129.6, 144.7) * mm, "radius": 0.5 * mm});
            skCircle(sketch, "E1.30.22.0", {"center": v(-129.6, 147.24) * mm, "radius": 0.5 * mm});
            skCircle(sketch, "E1.30.23.0", {"center": v(-129.6, 149.78) * mm, "radius": 0.5 * mm});
            skCircle(sketch, "E1.30.24.0", {"center": v(-129.6, 152.32) * mm, "radius": 0.5 * mm});
            skCircle(sketch, "E1.30.25.0", {"center": v(-129.6, 154.86) * mm, "radius": 0.5 * mm});
            skCircle(sketch, "E1.30.26.0", {"center": v(-129.6, 157.4) * mm, "radius": 0.5 * mm});
            skCircle(sketch, "E1.30.27.0", {"center": v(-129.6, 159.94) * mm, "radius": 0.5 * mm});
            skCircle(sketch, "E1.30.28.0", {"center": v(-129.6, 162.48) * mm, "radius": 0.5 * mm});
            skCircle(sketch, "E1.30.29.0", {"center": v(-129.6, 165.02) * mm, "radius": 0.5 * mm});
            skCircle(sketch, "E1.30.30.0", {"center": v(-129.6, 167.56) * mm, "radius": 0.5 * mm});
            skCircle(sketch, "E1.30.31.0", {"center": v(-129.6, 170.1) * mm, "radius": 0.5 * mm});
            skCircle(sketch, "E1.30.32.0", {"center": v(-129.6, 172.64) * mm, "radius": 0.5 * mm});
            skCircle(sketch, "E1.30.33.0", {"center": v(-129.6, 175.18) * mm, "radius": 0.5 * mm});
            skCircle(sketch, "E1.30.34.0", {"center": v(-129.6, 177.72) * mm, "radius": 0.5 * mm});
            skCircle(sketch, "E1.30.35.0", {"center": v(-129.6, 180.26) * mm, "radius": 0.5 * mm});
            skCircle(sketch, "E1.30.36.0", {"center": v(-129.6, 182.8) * mm, "radius": 0.5 * mm});
            skCircle(sketch, "E1.30.37.0", {"center": v(-129.6, 185.34) * mm, "radius": 0.5 * mm});
            skCircle(sketch, "E1.31.0.0", {"center": v(-127.07, 91.36) * mm, "radius": 0.5 * mm});
            skCircle(sketch, "E1.31.1.0", {"center": v(-127.07, 93.9) * mm, "radius": 0.5 * mm});
            skCircle(sketch, "E1.31.2.0", {"center": v(-127.07, 96.44) * mm, "radius": 0.5 * mm});
            skCircle(sketch, "E1.31.3.0", {"center": v(-127.07, 98.98) * mm, "radius": 0.5 * mm});
            skCircle(sketch, "E1.31.4.0", {"center": v(-127.07, 101.52) * mm, "radius": 0.5 * mm});
            skCircle(sketch, "E1.31.5.0", {"center": v(-127.07, 104.06) * mm, "radius": 0.5 * mm});
            skCircle(sketch, "E1.31.6.0", {"center": v(-127.07, 106.6) * mm, "radius": 0.5 * mm});
            skCircle(sketch, "E1.31.7.0", {"center": v(-127.07, 109.14) * mm, "radius": 0.5 * mm});
            skCircle(sketch, "E1.31.8.0", {"center": v(-127.07, 111.68) * mm, "radius": 0.5 * mm});
            skCircle(sketch, "E1.31.9.0", {"center": v(-127.07, 114.22) * mm, "radius": 0.5 * mm});
            skCircle(sketch, "E1.31.10.0", {"center": v(-127.07, 116.76) * mm, "radius": 0.5 * mm});
            skCircle(sketch, "E1.31.11.0", {"center": v(-127.07, 119.3) * mm, "radius": 0.5 * mm});
            skCircle(sketch, "E1.31.12.0", {"center": v(-127.07, 121.84) * mm, "radius": 0.5 * mm});
            skCircle(sketch, "E1.31.13.0", {"center": v(-127.07, 124.38) * mm, "radius": 0.5 * mm});
            skCircle(sketch, "E1.31.14.0", {"center": v(-127.07, 126.92) * mm, "radius": 0.5 * mm});
            skCircle(sketch, "E1.31.15.0", {"center": v(-127.07, 129.46) * mm, "radius": 0.5 * mm});
            skCircle(sketch, "E1.31.16.0", {"center": v(-127.07, 132) * mm, "radius": 0.5 * mm});
            skCircle(sketch, "E1.31.17.0", {"center": v(-127.07, 134.54) * mm, "radius": 0.5 * mm});
            skCircle(sketch, "E1.31.18.0", {"center": v(-127.07, 137.08) * mm, "radius": 0.5 * mm});
            skCircle(sketch, "E1.31.19.0", {"center": v(-127.07, 139.62) * mm, "radius": 0.5 * mm});
            skCircle(sketch, "E1.31.20.0", {"center": v(-127.07, 142.16) * mm, "radius": 0.5 * mm});
            skCircle(sketch, "E1.31.21.0", {"center": v(-127.07, 144.7) * mm, "radius": 0.5 * mm});
            skCircle(sketch, "E1.31.22.0", {"center": v(-127.07, 147.24) * mm, "radius": 0.5 * mm});
            skCircle(sketch, "E1.31.23.0", {"center": v(-127.07, 149.78) * mm, "radius": 0.5 * mm});
            skCircle(sketch, "E1.31.24.0", {"center": v(-127.07, 152.32) * mm, "radius": 0.5 * mm});
            skCircle(sketch, "E1.31.25.0", {"center": v(-127.07, 154.86) * mm, "radius": 0.5 * mm});
            skCircle(sketch, "E1.31.26.0", {"center": v(-127.07, 157.4) * mm, "radius": 0.5 * mm});
            skCircle(sketch, "E1.31.27.0", {"center": v(-127.07, 159.94) * mm, "radius": 0.5 * mm});
            skCircle(sketch, "E1.31.28.0", {"center": v(-127.07, 162.48) * mm, "radius": 0.5 * mm});
            skCircle(sketch, "E1.31.29.0", {"center": v(-127.07, 165.02) * mm, "radius": 0.5 * mm});
            skCircle(sketch, "E1.31.30.0", {"center": v(-127.07, 167.56) * mm, "radius": 0.5 * mm});
            skCircle(sketch, "E1.31.31.0", {"center": v(-127.07, 170.1) * mm, "radius": 0.5 * mm});
            skCircle(sketch, "E1.31.32.0", {"center": v(-127.07, 172.64) * mm, "radius": 0.5 * mm});
            skCircle(sketch, "E1.31.33.0", {"center": v(-127.07, 175.18) * mm, "radius": 0.5 * mm});
            skCircle(sketch, "E1.31.34.0", {"center": v(-127.07, 177.72) * mm, "radius": 0.5 * mm});
            skCircle(sketch, "E1.31.35.0", {"center": v(-127.07, 180.26) * mm, "radius": 0.5 * mm});
            skCircle(sketch, "E1.31.36.0", {"center": v(-127.07, 182.8) * mm, "radius": 0.5 * mm});
            skCircle(sketch, "E1.31.37.0", {"center": v(-127.07, 185.34) * mm, "radius": 0.5 * mm});
            skCircle(sketch, "E1.32.0.0", {"center": v(-124.53, 91.36) * mm, "radius": 0.5 * mm});
            skCircle(sketch, "E1.32.1.0", {"center": v(-124.53, 93.9) * mm, "radius": 0.5 * mm});
            skCircle(sketch, "E1.32.2.0", {"center": v(-124.53, 96.44) * mm, "radius": 0.5 * mm});
            skCircle(sketch, "E1.32.3.0", {"center": v(-124.53, 98.98) * mm, "radius": 0.5 * mm});
            skCircle(sketch, "E1.32.4.0", {"center": v(-124.53, 101.52) * mm, "radius": 0.5 * mm});
            skCircle(sketch, "E1.32.5.0", {"center": v(-124.53, 104.06) * mm, "radius": 0.5 * mm});
            skCircle(sketch, "E1.32.6.0", {"center": v(-124.53, 106.6) * mm, "radius": 0.5 * mm});
            skCircle(sketch, "E1.32.7.0", {"center": v(-124.53, 109.14) * mm, "radius": 0.5 * mm});
            skCircle(sketch, "E1.32.8.0", {"center": v(-124.53, 111.68) * mm, "radius": 0.5 * mm});
            skCircle(sketch, "E1.32.9.0", {"center": v(-124.53, 114.22) * mm, "radius": 0.5 * mm});
            skCircle(sketch, "E1.32.10.0", {"center": v(-124.53, 116.76) * mm, "radius": 0.5 * mm});
            skCircle(sketch, "E1.32.11.0", {"center": v(-124.53, 119.3) * mm, "radius": 0.5 * mm});
            skCircle(sketch, "E1.32.12.0", {"center": v(-124.53, 121.84) * mm, "radius": 0.5 * mm});
            skCircle(sketch, "E1.32.13.0", {"center": v(-124.53, 124.38) * mm, "radius": 0.5 * mm});
            skCircle(sketch, "E1.32.14.0", {"center": v(-124.53, 126.92) * mm, "radius": 0.5 * mm});
            skCircle(sketch, "E1.32.15.0", {"center": v(-124.53, 129.46) * mm, "radius": 0.5 * mm});
            skCircle(sketch, "E1.32.16.0", {"center": v(-124.53, 132) * mm, "radius": 0.5 * mm});
            skCircle(sketch, "E1.32.17.0", {"center": v(-124.53, 134.54) * mm, "radius": 0.5 * mm});
            skCircle(sketch, "E1.32.18.0", {"center": v(-124.53, 137.08) * mm, "radius": 0.5 * mm});
            skCircle(sketch, "E1.32.19.0", {"center": v(-124.53, 139.62) * mm, "radius": 0.5 * mm});
            skCircle(sketch, "E1.32.20.0", {"center": v(-124.53, 142.16) * mm, "radius": 0.5 * mm});
            skCircle(sketch, "E1.32.21.0", {"center": v(-124.53, 144.7) * mm, "radius": 0.5 * mm});
            skCircle(sketch, "E1.32.22.0", {"center": v(-124.53, 147.24) * mm, "radius": 0.5 * mm});
            skCircle(sketch, "E1.32.23.0", {"center": v(-124.53, 149.78) * mm, "radius": 0.5 * mm});
            skCircle(sketch, "E1.32.24.0", {"center": v(-124.53, 152.32) * mm, "radius": 0.5 * mm});
            skCircle(sketch, "E1.32.25.0", {"center": v(-124.53, 154.86) * mm, "radius": 0.5 * mm});
            skCircle(sketch, "E1.32.26.0", {"center": v(-124.53, 157.4) * mm, "radius": 0.5 * mm});
            skCircle(sketch, "E1.32.27.0", {"center": v(-124.53, 159.94) * mm, "radius": 0.5 * mm});
            skCircle(sketch, "E1.32.28.0", {"center": v(-124.53, 162.48) * mm, "radius": 0.5 * mm});
            skCircle(sketch, "E1.32.29.0", {"center": v(-124.53, 165.02) * mm, "radius": 0.5 * mm});
            skCircle(sketch, "E1.32.30.0", {"center": v(-124.53, 167.56) * mm, "radius": 0.5 * mm});
            skCircle(sketch, "E1.32.31.0", {"center": v(-124.53, 170.1) * mm, "radius": 0.5 * mm});
            skCircle(sketch, "E1.32.32.0", {"center": v(-124.53, 172.64) * mm, "radius": 0.5 * mm});
            skCircle(sketch, "E1.32.33.0", {"center": v(-124.53, 175.18) * mm, "radius": 0.5 * mm});
            skCircle(sketch, "E1.32.34.0", {"center": v(-124.53, 177.72) * mm, "radius": 0.5 * mm});
            skCircle(sketch, "E1.32.35.0", {"center": v(-124.53, 180.26) * mm, "radius": 0.5 * mm});
            skCircle(sketch, "E1.32.36.0", {"center": v(-124.53, 182.8) * mm, "radius": 0.5 * mm});
            skCircle(sketch, "E1.32.37.0", {"center": v(-124.53, 185.34) * mm, "radius": 0.5 * mm});
            skCircle(sketch, "E1.33.0.0", {"center": v(-121.99, 91.36) * mm, "radius": 0.5 * mm});
            skCircle(sketch, "E1.33.1.0", {"center": v(-121.99, 93.9) * mm, "radius": 0.5 * mm});
            skCircle(sketch, "E1.33.2.0", {"center": v(-121.99, 96.44) * mm, "radius": 0.5 * mm});
            skCircle(sketch, "E1.33.3.0", {"center": v(-121.99, 98.98) * mm, "radius": 0.5 * mm});
            skCircle(sketch, "E1.33.4.0", {"center": v(-121.99, 101.52) * mm, "radius": 0.5 * mm});
            skCircle(sketch, "E1.33.5.0", {"center": v(-121.99, 104.06) * mm, "radius": 0.5 * mm});
            skCircle(sketch, "E1.33.6.0", {"center": v(-121.99, 106.6) * mm, "radius": 0.5 * mm});
            skCircle(sketch, "E1.33.7.0", {"center": v(-121.99, 109.14) * mm, "radius": 0.5 * mm});
            skCircle(sketch, "E1.33.8.0", {"center": v(-121.99, 111.68) * mm, "radius": 0.5 * mm});
            skCircle(sketch, "E1.33.9.0", {"center": v(-121.99, 114.22) * mm, "radius": 0.5 * mm});
            skCircle(sketch, "E1.33.10.0", {"center": v(-121.99, 116.76) * mm, "radius": 0.5 * mm});
            skCircle(sketch, "E1.33.11.0", {"center": v(-121.99, 119.3) * mm, "radius": 0.5 * mm});
            skCircle(sketch, "E1.33.12.0", {"center": v(-121.99, 121.84) * mm, "radius": 0.5 * mm});
            skCircle(sketch, "E1.33.13.0", {"center": v(-121.99, 124.38) * mm, "radius": 0.5 * mm});
            skCircle(sketch, "E1.33.14.0", {"center": v(-121.99, 126.92) * mm, "radius": 0.5 * mm});
            skCircle(sketch, "E1.33.15.0", {"center": v(-121.99, 129.46) * mm, "radius": 0.5 * mm});
            skCircle(sketch, "E1.33.16.0", {"center": v(-121.99, 132) * mm, "radius": 0.5 * mm});
            skCircle(sketch, "E1.33.17.0", {"center": v(-121.99, 134.54) * mm, "radius": 0.5 * mm});
            skCircle(sketch, "E1.33.18.0", {"center": v(-121.99, 137.08) * mm, "radius": 0.5 * mm});
            skCircle(sketch, "E1.33.19.0", {"center": v(-121.99, 139.62) * mm, "radius": 0.5 * mm});
            skCircle(sketch, "E1.33.20.0", {"center": v(-121.99, 142.16) * mm, "radius": 0.5 * mm});
            skCircle(sketch, "E1.33.21.0", {"center": v(-121.99, 144.7) * mm, "radius": 0.5 * mm});
            skCircle(sketch, "E1.33.22.0", {"center": v(-121.99, 147.24) * mm, "radius": 0.5 * mm});
            skCircle(sketch, "E1.33.23.0", {"center": v(-121.99, 149.78) * mm, "radius": 0.5 * mm});
            skCircle(sketch, "E1.33.24.0", {"center": v(-121.99, 152.32) * mm, "radius": 0.5 * mm});
            skCircle(sketch, "E1.33.25.0", {"center": v(-121.99, 154.86) * mm, "radius": 0.5 * mm});
            skCircle(sketch, "E1.33.26.0", {"center": v(-121.99, 157.4) * mm, "radius": 0.5 * mm});
            skCircle(sketch, "E1.33.27.0", {"center": v(-121.99, 159.94) * mm, "radius": 0.5 * mm});
            skCircle(sketch, "E1.33.28.0", {"center": v(-121.99, 162.48) * mm, "radius": 0.5 * mm});
            skCircle(sketch, "E1.33.29.0", {"center": v(-121.99, 165.02) * mm, "radius": 0.5 * mm});
            skCircle(sketch, "E1.33.30.0", {"center": v(-121.99, 167.56) * mm, "radius": 0.5 * mm});
            skCircle(sketch, "E1.33.31.0", {"center": v(-121.99, 170.1) * mm, "radius": 0.5 * mm});
            skCircle(sketch, "E1.33.32.0", {"center": v(-121.99, 172.64) * mm, "radius": 0.5 * mm});
            skCircle(sketch, "E1.33.33.0", {"center": v(-121.99, 175.18) * mm, "radius": 0.5 * mm});
            skCircle(sketch, "E1.33.34.0", {"center": v(-121.99, 177.72) * mm, "radius": 0.5 * mm});
            skCircle(sketch, "E1.33.35.0", {"center": v(-121.99, 180.26) * mm, "radius": 0.5 * mm});
            skCircle(sketch, "E1.33.36.0", {"center": v(-121.99, 182.8) * mm, "radius": 0.5 * mm});
            skCircle(sketch, "E1.33.37.0", {"center": v(-121.99, 185.34) * mm, "radius": 0.5 * mm});
            skCircle(sketch, "E1.34.0.0", {"center": v(-119.45, 91.36) * mm, "radius": 0.5 * mm});
            skCircle(sketch, "E1.34.1.0", {"center": v(-119.45, 93.9) * mm, "radius": 0.5 * mm});
            skCircle(sketch, "E1.34.2.0", {"center": v(-119.45, 96.44) * mm, "radius": 0.5 * mm});
            skCircle(sketch, "E1.34.3.0", {"center": v(-119.45, 98.98) * mm, "radius": 0.5 * mm});
            skCircle(sketch, "E1.34.4.0", {"center": v(-119.45, 101.52) * mm, "radius": 0.5 * mm});
            skCircle(sketch, "E1.34.5.0", {"center": v(-119.45, 104.06) * mm, "radius": 0.5 * mm});
            skCircle(sketch, "E1.34.6.0", {"center": v(-119.45, 106.6) * mm, "radius": 0.5 * mm});
            skCircle(sketch, "E1.34.7.0", {"center": v(-119.45, 109.14) * mm, "radius": 0.5 * mm});
            skCircle(sketch, "E1.34.8.0", {"center": v(-119.45, 111.68) * mm, "radius": 0.5 * mm});
            skCircle(sketch, "E1.34.9.0", {"center": v(-119.45, 114.22) * mm, "radius": 0.5 * mm});
            skCircle(sketch, "E1.34.10.0", {"center": v(-119.45, 116.76) * mm, "radius": 0.5 * mm});
            skCircle(sketch, "E1.34.11.0", {"center": v(-119.45, 119.3) * mm, "radius": 0.5 * mm});
            skCircle(sketch, "E1.34.12.0", {"center": v(-119.45, 121.84) * mm, "radius": 0.5 * mm});
            skCircle(sketch, "E1.34.13.0", {"center": v(-119.45, 124.38) * mm, "radius": 0.5 * mm});
            skCircle(sketch, "E1.34.14.0", {"center": v(-119.45, 126.92) * mm, "radius": 0.5 * mm});
            skCircle(sketch, "E1.34.15.0", {"center": v(-119.45, 129.46) * mm, "radius": 0.5 * mm});
            skCircle(sketch, "E1.34.16.0", {"center": v(-119.45, 132) * mm, "radius": 0.5 * mm});
            skCircle(sketch, "E1.34.17.0", {"center": v(-119.45, 134.54) * mm, "radius": 0.5 * mm});
            skCircle(sketch, "E1.34.18.0", {"center": v(-119.45, 137.08) * mm, "radius": 0.5 * mm});
            skCircle(sketch, "E1.34.19.0", {"center": v(-119.45, 139.62) * mm, "radius": 0.5 * mm});
            skCircle(sketch, "E1.34.20.0", {"center": v(-119.45, 142.16) * mm, "radius": 0.5 * mm});
            skCircle(sketch, "E1.34.21.0", {"center": v(-119.45, 144.7) * mm, "radius": 0.5 * mm});
            skCircle(sketch, "E1.34.22.0", {"center": v(-119.45, 147.24) * mm, "radius": 0.5 * mm});
            skCircle(sketch, "E1.34.23.0", {"center": v(-119.45, 149.78) * mm, "radius": 0.5 * mm});
            skCircle(sketch, "E1.34.24.0", {"center": v(-119.45, 152.32) * mm, "radius": 0.5 * mm});
            skCircle(sketch, "E1.34.25.0", {"center": v(-119.45, 154.86) * mm, "radius": 0.5 * mm});
            skCircle(sketch, "E1.34.26.0", {"center": v(-119.45, 157.4) * mm, "radius": 0.5 * mm});
            skCircle(sketch, "E1.34.27.0", {"center": v(-119.45, 159.94) * mm, "radius": 0.5 * mm});
            skCircle(sketch, "E1.34.28.0", {"center": v(-119.45, 162.48) * mm, "radius": 0.5 * mm});
            skCircle(sketch, "E1.34.29.0", {"center": v(-119.45, 165.02) * mm, "radius": 0.5 * mm});
            skCircle(sketch, "E1.34.30.0", {"center": v(-119.45, 167.56) * mm, "radius": 0.5 * mm});
            skCircle(sketch, "E1.34.31.0", {"center": v(-119.45, 170.1) * mm, "radius": 0.5 * mm});
            skCircle(sketch, "E1.34.32.0", {"center": v(-119.45, 172.64) * mm, "radius": 0.5 * mm});
            skCircle(sketch, "E1.34.33.0", {"center": v(-119.45, 175.18) * mm, "radius": 0.5 * mm});
            skCircle(sketch, "E1.34.34.0", {"center": v(-119.45, 177.72) * mm, "radius": 0.5 * mm});
            skCircle(sketch, "E1.34.35.0", {"center": v(-119.45, 180.26) * mm, "radius": 0.5 * mm});
            skCircle(sketch, "E1.34.36.0", {"center": v(-119.45, 182.8) * mm, "radius": 0.5 * mm});
            skCircle(sketch, "E1.34.37.0", {"center": v(-119.45, 185.34) * mm, "radius": 0.5 * mm});
            skCircle(sketch, "E1.35.0.0", {"center": v(-116.9, 91.36) * mm, "radius": 0.5 * mm});
            skCircle(sketch, "E1.35.1.0", {"center": v(-116.9, 93.9) * mm, "radius": 0.5 * mm});
            skCircle(sketch, "E1.35.2.0", {"center": v(-116.9, 96.44) * mm, "radius": 0.5 * mm});
            skCircle(sketch, "E1.35.3.0", {"center": v(-116.9, 98.98) * mm, "radius": 0.5 * mm});
            skCircle(sketch, "E1.35.4.0", {"center": v(-116.9, 101.52) * mm, "radius": 0.5 * mm});
            skCircle(sketch, "E1.35.5.0", {"center": v(-116.9, 104.06) * mm, "radius": 0.5 * mm});
            skCircle(sketch, "E1.35.6.0", {"center": v(-116.9, 106.6) * mm, "radius": 0.5 * mm});
            skCircle(sketch, "E1.35.7.0", {"center": v(-116.9, 109.14) * mm, "radius": 0.5 * mm});
            skCircle(sketch, "E1.35.8.0", {"center": v(-116.9, 111.68) * mm, "radius": 0.5 * mm});
            skCircle(sketch, "E1.35.9.0", {"center": v(-116.9, 114.22) * mm, "radius": 0.5 * mm});
            skCircle(sketch, "E1.35.10.0", {"center": v(-116.9, 116.76) * mm, "radius": 0.5 * mm});
            skCircle(sketch, "E1.35.11.0", {"center": v(-116.9, 119.3) * mm, "radius": 0.5 * mm});
            skCircle(sketch, "E1.35.12.0", {"center": v(-116.9, 121.84) * mm, "radius": 0.5 * mm});
            skCircle(sketch, "E1.35.13.0", {"center": v(-116.9, 124.38) * mm, "radius": 0.5 * mm});
            skCircle(sketch, "E1.35.14.0", {"center": v(-116.9, 126.92) * mm, "radius": 0.5 * mm});
            skCircle(sketch, "E1.35.15.0", {"center": v(-116.9, 129.46) * mm, "radius": 0.5 * mm});
            skCircle(sketch, "E1.35.16.0", {"center": v(-116.9, 132) * mm, "radius": 0.5 * mm});
            skCircle(sketch, "E1.35.17.0", {"center": v(-116.9, 134.54) * mm, "radius": 0.5 * mm});
            skCircle(sketch, "E1.35.18.0", {"center": v(-116.9, 137.08) * mm, "radius": 0.5 * mm});
            skCircle(sketch, "E1.35.19.0", {"center": v(-116.9, 139.62) * mm, "radius": 0.5 * mm});
            skCircle(sketch, "E1.35.20.0", {"center": v(-116.9, 142.16) * mm, "radius": 0.5 * mm});
            skCircle(sketch, "E1.35.21.0", {"center": v(-116.9, 144.7) * mm, "radius": 0.5 * mm});
            skCircle(sketch, "E1.35.22.0", {"center": v(-116.9, 147.24) * mm, "radius": 0.5 * mm});
            skCircle(sketch, "E1.35.23.0", {"center": v(-116.9, 149.78) * mm, "radius": 0.5 * mm});
            skCircle(sketch, "E1.35.24.0", {"center": v(-116.9, 152.32) * mm, "radius": 0.5 * mm});
            skCircle(sketch, "E1.35.25.0", {"center": v(-116.9, 154.86) * mm, "radius": 0.5 * mm});
            skCircle(sketch, "E1.35.26.0", {"center": v(-116.9, 157.4) * mm, "radius": 0.5 * mm});
            skCircle(sketch, "E1.35.27.0", {"center": v(-116.9, 159.94) * mm, "radius": 0.5 * mm});
            skCircle(sketch, "E1.35.28.0", {"center": v(-116.9, 162.48) * mm, "radius": 0.5 * mm});
            skCircle(sketch, "E1.35.29.0", {"center": v(-116.9, 165.02) * mm, "radius": 0.5 * mm});
            skCircle(sketch, "E1.35.30.0", {"center": v(-116.9, 167.56) * mm, "radius": 0.5 * mm});
            skCircle(sketch, "E1.35.31.0", {"center": v(-116.9, 170.1) * mm, "radius": 0.5 * mm});
            skCircle(sketch, "E1.35.32.0", {"center": v(-116.9, 172.64) * mm, "radius": 0.5 * mm});
            skCircle(sketch, "E1.35.33.0", {"center": v(-116.9, 175.18) * mm, "radius": 0.5 * mm});
            skCircle(sketch, "E1.35.34.0", {"center": v(-116.9, 177.72) * mm, "radius": 0.5 * mm});
            skCircle(sketch, "E1.35.35.0", {"center": v(-116.9, 180.26) * mm, "radius": 0.5 * mm});
            skCircle(sketch, "E1.35.36.0", {"center": v(-116.9, 182.8) * mm, "radius": 0.5 * mm});
            skCircle(sketch, "E1.35.37.0", {"center": v(-116.9, 185.34) * mm, "radius": 0.5 * mm});
            skCircle(sketch, "E1.36.0.0", {"center": v(-114.37, 91.36) * mm, "radius": 0.5 * mm});
            skCircle(sketch, "E1.36.1.0", {"center": v(-114.37, 93.9) * mm, "radius": 0.5 * mm});
            skCircle(sketch, "E1.36.2.0", {"center": v(-114.37, 96.44) * mm, "radius": 0.5 * mm});
            skCircle(sketch, "E1.36.3.0", {"center": v(-114.37, 98.98) * mm, "radius": 0.5 * mm});
            skCircle(sketch, "E1.36.4.0", {"center": v(-114.37, 101.52) * mm, "radius": 0.5 * mm});
            skCircle(sketch, "E1.36.5.0", {"center": v(-114.37, 104.06) * mm, "radius": 0.5 * mm});
            skCircle(sketch, "E1.36.6.0", {"center": v(-114.37, 106.6) * mm, "radius": 0.5 * mm});
            skCircle(sketch, "E1.36.7.0", {"center": v(-114.37, 109.14) * mm, "radius": 0.5 * mm});
            skCircle(sketch, "E1.36.8.0", {"center": v(-114.37, 111.68) * mm, "radius": 0.5 * mm});
            skCircle(sketch, "E1.36.9.0", {"center": v(-114.37, 114.22) * mm, "radius": 0.5 * mm});
            skCircle(sketch, "E1.36.10.0", {"center": v(-114.37, 116.76) * mm, "radius": 0.5 * mm});
            skCircle(sketch, "E1.36.11.0", {"center": v(-114.37, 119.3) * mm, "radius": 0.5 * mm});
            skCircle(sketch, "E1.36.12.0", {"center": v(-114.37, 121.84) * mm, "radius": 0.5 * mm});
            skCircle(sketch, "E1.36.13.0", {"center": v(-114.37, 124.38) * mm, "radius": 0.5 * mm});
            skCircle(sketch, "E1.36.14.0", {"center": v(-114.37, 126.92) * mm, "radius": 0.5 * mm});
            skCircle(sketch, "E1.36.15.0", {"center": v(-114.37, 129.46) * mm, "radius": 0.5 * mm});
            skCircle(sketch, "E1.36.16.0", {"center": v(-114.37, 132) * mm, "radius": 0.5 * mm});
            skCircle(sketch, "E1.36.17.0", {"center": v(-114.37, 134.54) * mm, "radius": 0.5 * mm});
            skCircle(sketch, "E1.36.18.0", {"center": v(-114.37, 137.08) * mm, "radius": 0.5 * mm});
            skCircle(sketch, "E1.36.19.0", {"center": v(-114.37, 139.62) * mm, "radius": 0.5 * mm});
            skCircle(sketch, "E1.36.20.0", {"center": v(-114.37, 142.16) * mm, "radius": 0.5 * mm});
            skCircle(sketch, "E1.36.21.0", {"center": v(-114.37, 144.7) * mm, "radius": 0.5 * mm});
            skCircle(sketch, "E1.36.22.0", {"center": v(-114.37, 147.24) * mm, "radius": 0.5 * mm});
            skCircle(sketch, "E1.36.23.0", {"center": v(-114.37, 149.78) * mm, "radius": 0.5 * mm});
            skCircle(sketch, "E1.36.24.0", {"center": v(-114.37, 152.32) * mm, "radius": 0.5 * mm});
            skCircle(sketch, "E1.36.25.0", {"center": v(-114.37, 154.86) * mm, "radius": 0.5 * mm});
            skCircle(sketch, "E1.36.26.0", {"center": v(-114.37, 157.4) * mm, "radius": 0.5 * mm});
            skCircle(sketch, "E1.36.27.0", {"center": v(-114.37, 159.94) * mm, "radius": 0.5 * mm});
            skCircle(sketch, "E1.36.28.0", {"center": v(-114.37, 162.48) * mm, "radius": 0.5 * mm});
            skCircle(sketch, "E1.36.29.0", {"center": v(-114.37, 165.02) * mm, "radius": 0.5 * mm});
            skCircle(sketch, "E1.36.30.0", {"center": v(-114.37, 167.56) * mm, "radius": 0.5 * mm});
            skCircle(sketch, "E1.36.31.0", {"center": v(-114.37, 170.1) * mm, "radius": 0.5 * mm});
            skCircle(sketch, "E1.36.32.0", {"center": v(-114.37, 172.64) * mm, "radius": 0.5 * mm});
            skCircle(sketch, "E1.36.33.0", {"center": v(-114.37, 175.18) * mm, "radius": 0.5 * mm});
            skCircle(sketch, "E1.36.34.0", {"center": v(-114.37, 177.72) * mm, "radius": 0.5 * mm});
            skCircle(sketch, "E1.36.35.0", {"center": v(-114.37, 180.26) * mm, "radius": 0.5 * mm});
            skCircle(sketch, "E1.36.36.0", {"center": v(-114.37, 182.8) * mm, "radius": 0.5 * mm});
            skCircle(sketch, "E1.36.37.0", {"center": v(-114.37, 185.34) * mm, "radius": 0.5 * mm});
            skCircle(sketch, "E1.37.0.0", {"center": v(-111.83, 91.36) * mm, "radius": 0.5 * mm});
            skCircle(sketch, "E1.37.1.0", {"center": v(-111.83, 93.9) * mm, "radius": 0.5 * mm});
            skCircle(sketch, "E1.37.2.0", {"center": v(-111.83, 96.44) * mm, "radius": 0.5 * mm});
            skCircle(sketch, "E1.37.3.0", {"center": v(-111.83, 98.98) * mm, "radius": 0.5 * mm});
            skCircle(sketch, "E1.37.4.0", {"center": v(-111.83, 101.52) * mm, "radius": 0.5 * mm});
            skCircle(sketch, "E1.37.5.0", {"center": v(-111.83, 104.06) * mm, "radius": 0.5 * mm});
            skCircle(sketch, "E1.37.6.0", {"center": v(-111.83, 106.6) * mm, "radius": 0.5 * mm});
            skCircle(sketch, "E1.37.7.0", {"center": v(-111.83, 109.14) * mm, "radius": 0.5 * mm});
            skCircle(sketch, "E1.37.8.0", {"center": v(-111.83, 111.68) * mm, "radius": 0.5 * mm});
            skCircle(sketch, "E1.37.9.0", {"center": v(-111.83, 114.22) * mm, "radius": 0.5 * mm});
            skCircle(sketch, "E1.37.10.0", {"center": v(-111.83, 116.76) * mm, "radius": 0.5 * mm});
            skCircle(sketch, "E1.37.11.0", {"center": v(-111.83, 119.3) * mm, "radius": 0.5 * mm});
            skCircle(sketch, "E1.37.12.0", {"center": v(-111.83, 121.84) * mm, "radius": 0.5 * mm});
            skCircle(sketch, "E1.37.13.0", {"center": v(-111.83, 124.38) * mm, "radius": 0.5 * mm});
            skCircle(sketch, "E1.37.14.0", {"center": v(-111.83, 126.92) * mm, "radius": 0.5 * mm});
            skCircle(sketch, "E1.37.15.0", {"center": v(-111.83, 129.46) * mm, "radius": 0.5 * mm});
            skCircle(sketch, "E1.37.16.0", {"center": v(-111.83, 132) * mm, "radius": 0.5 * mm});
            skCircle(sketch, "E1.37.17.0", {"center": v(-111.83, 134.54) * mm, "radius": 0.5 * mm});
            skCircle(sketch, "E1.37.18.0", {"center": v(-111.83, 137.08) * mm, "radius": 0.5 * mm});
            skCircle(sketch, "E1.37.19.0", {"center": v(-111.83, 139.62) * mm, "radius": 0.5 * mm});
            skCircle(sketch, "E1.37.20.0", {"center": v(-111.83, 142.16) * mm, "radius": 0.5 * mm});
            skCircle(sketch, "E1.37.21.0", {"center": v(-111.83, 144.7) * mm, "radius": 0.5 * mm});
            skCircle(sketch, "E1.37.22.0", {"center": v(-111.83, 147.24) * mm, "radius": 0.5 * mm});
            skCircle(sketch, "E1.37.23.0", {"center": v(-111.83, 149.78) * mm, "radius": 0.5 * mm});
            skCircle(sketch, "E1.37.24.0", {"center": v(-111.83, 152.32) * mm, "radius": 0.5 * mm});
            skCircle(sketch, "E1.37.25.0", {"center": v(-111.83, 154.86) * mm, "radius": 0.5 * mm});
            skCircle(sketch, "E1.37.26.0", {"center": v(-111.83, 157.4) * mm, "radius": 0.5 * mm});
            skCircle(sketch, "E1.37.27.0", {"center": v(-111.83, 159.94) * mm, "radius": 0.5 * mm});
            skCircle(sketch, "E1.37.28.0", {"center": v(-111.83, 162.48) * mm, "radius": 0.5 * mm});
            skCircle(sketch, "E1.37.29.0", {"center": v(-111.83, 165.02) * mm, "radius": 0.5 * mm});
            skCircle(sketch, "E1.37.30.0", {"center": v(-111.83, 167.56) * mm, "radius": 0.5 * mm});
            skCircle(sketch, "E1.37.31.0", {"center": v(-111.83, 170.1) * mm, "radius": 0.5 * mm});
            skCircle(sketch, "E1.37.32.0", {"center": v(-111.83, 172.64) * mm, "radius": 0.5 * mm});
            skCircle(sketch, "E1.37.33.0", {"center": v(-111.83, 175.18) * mm, "radius": 0.5 * mm});
            skCircle(sketch, "E1.37.34.0", {"center": v(-111.83, 177.72) * mm, "radius": 0.5 * mm});
            skCircle(sketch, "E1.37.35.0", {"center": v(-111.83, 180.26) * mm, "radius": 0.5 * mm});
            skCircle(sketch, "E1.37.36.0", {"center": v(-111.83, 182.8) * mm, "radius": 0.5 * mm});
            skCircle(sketch, "E1.37.37.0", {"center": v(-111.83, 185.34) * mm, "radius": 0.5 * mm});
            skCircle(sketch, "E1.38.0.0", {"center": v(-109.29, 91.36) * mm, "radius": 0.5 * mm});
            skCircle(sketch, "E1.38.1.0", {"center": v(-109.29, 93.9) * mm, "radius": 0.5 * mm});
            skCircle(sketch, "E1.38.2.0", {"center": v(-109.29, 96.44) * mm, "radius": 0.5 * mm});
            skCircle(sketch, "E1.38.3.0", {"center": v(-109.29, 98.98) * mm, "radius": 0.5 * mm});
            skCircle(sketch, "E1.38.4.0", {"center": v(-109.29, 101.52) * mm, "radius": 0.5 * mm});
            skCircle(sketch, "E1.38.5.0", {"center": v(-109.29, 104.06) * mm, "radius": 0.5 * mm});
            skCircle(sketch, "E1.38.6.0", {"center": v(-109.29, 106.6) * mm, "radius": 0.5 * mm});
            skCircle(sketch, "E1.38.7.0", {"center": v(-109.29, 109.14) * mm, "radius": 0.5 * mm});
            skCircle(sketch, "E1.38.8.0", {"center": v(-109.29, 111.68) * mm, "radius": 0.5 * mm});
            skCircle(sketch, "E1.38.9.0", {"center": v(-109.29, 114.22) * mm, "radius": 0.5 * mm});
            skCircle(sketch, "E1.38.10.0", {"center": v(-109.29, 116.76) * mm, "radius": 0.5 * mm});
            skCircle(sketch, "E1.38.11.0", {"center": v(-109.29, 119.3) * mm, "radius": 0.5 * mm});
            skCircle(sketch, "E1.38.12.0", {"center": v(-109.29, 121.84) * mm, "radius": 0.5 * mm});
            skCircle(sketch, "E1.38.13.0", {"center": v(-109.29, 124.38) * mm, "radius": 0.5 * mm});
            skCircle(sketch, "E1.38.14.0", {"center": v(-109.29, 126.92) * mm, "radius": 0.5 * mm});
            skCircle(sketch, "E1.38.15.0", {"center": v(-109.29, 129.46) * mm, "radius": 0.5 * mm});
            skCircle(sketch, "E1.38.16.0", {"center": v(-109.29, 132) * mm, "radius": 0.5 * mm});
            skCircle(sketch, "E1.38.17.0", {"center": v(-109.29, 134.54) * mm, "radius": 0.5 * mm});
            skCircle(sketch, "E1.38.18.0", {"center": v(-109.29, 137.08) * mm, "radius": 0.5 * mm});
            skCircle(sketch, "E1.38.19.0", {"center": v(-109.29, 139.62) * mm, "radius": 0.5 * mm});
            skCircle(sketch, "E1.38.20.0", {"center": v(-109.29, 142.16) * mm, "radius": 0.5 * mm});
            skCircle(sketch, "E1.38.21.0", {"center": v(-109.29, 144.7) * mm, "radius": 0.5 * mm});
            skCircle(sketch, "E1.38.22.0", {"center": v(-109.29, 147.24) * mm, "radius": 0.5 * mm});
            skCircle(sketch, "E1.38.23.0", {"center": v(-109.29, 149.78) * mm, "radius": 0.5 * mm});
            skCircle(sketch, "E1.38.24.0", {"center": v(-109.29, 152.32) * mm, "radius": 0.5 * mm});
            skCircle(sketch, "E1.38.25.0", {"center": v(-109.29, 154.86) * mm, "radius": 0.5 * mm});
            skCircle(sketch, "E1.38.26.0", {"center": v(-109.29, 157.4) * mm, "radius": 0.5 * mm});
            skCircle(sketch, "E1.38.27.0", {"center": v(-109.29, 159.94) * mm, "radius": 0.5 * mm});
            skCircle(sketch, "E1.38.28.0", {"center": v(-109.29, 162.48) * mm, "radius": 0.5 * mm});
            skCircle(sketch, "E1.38.29.0", {"center": v(-109.29, 165.02) * mm, "radius": 0.5 * mm});
            skCircle(sketch, "E1.38.30.0", {"center": v(-109.29, 167.56) * mm, "radius": 0.5 * mm});
            skCircle(sketch, "E1.38.31.0", {"center": v(-109.29, 170.1) * mm, "radius": 0.5 * mm});
            skCircle(sketch, "E1.38.32.0", {"center": v(-109.29, 172.64) * mm, "radius": 0.5 * mm});
            skCircle(sketch, "E1.38.33.0", {"center": v(-109.29, 175.18) * mm, "radius": 0.5 * mm});
            skCircle(sketch, "E1.38.34.0", {"center": v(-109.29, 177.72) * mm, "radius": 0.5 * mm});
            skCircle(sketch, "E1.38.35.0", {"center": v(-109.29, 180.26) * mm, "radius": 0.5 * mm});
            skCircle(sketch, "E1.38.36.0", {"center": v(-109.29, 182.8) * mm, "radius": 0.5 * mm});
            skCircle(sketch, "E1.38.37.0", {"center": v(-109.29, 185.34) * mm, "radius": 0.5 * mm});
            skCircle(sketch, "E1.39.0.0", {"center": v(-106.75, 91.36) * mm, "radius": 0.5 * mm});
            skCircle(sketch, "E1.39.1.0", {"center": v(-106.75, 93.9) * mm, "radius": 0.5 * mm});
            skCircle(sketch, "E1.39.2.0", {"center": v(-106.75, 96.44) * mm, "radius": 0.5 * mm});
            skCircle(sketch, "E1.39.3.0", {"center": v(-106.75, 98.98) * mm, "radius": 0.5 * mm});
            skCircle(sketch, "E1.39.4.0", {"center": v(-106.75, 101.52) * mm, "radius": 0.5 * mm});
            skCircle(sketch, "E1.39.5.0", {"center": v(-106.75, 104.06) * mm, "radius": 0.5 * mm});
            skCircle(sketch, "E1.39.6.0", {"center": v(-106.75, 106.6) * mm, "radius": 0.5 * mm});
            skCircle(sketch, "E1.39.7.0", {"center": v(-106.75, 109.14) * mm, "radius": 0.5 * mm});
            skCircle(sketch, "E1.39.8.0", {"center": v(-106.75, 111.68) * mm, "radius": 0.5 * mm});
            skCircle(sketch, "E1.39.9.0", {"center": v(-106.75, 114.22) * mm, "radius": 0.5 * mm});
            skCircle(sketch, "E1.39.10.0", {"center": v(-106.75, 116.76) * mm, "radius": 0.5 * mm});
            skCircle(sketch, "E1.39.11.0", {"center": v(-106.75, 119.3) * mm, "radius": 0.5 * mm});
            skCircle(sketch, "E1.39.12.0", {"center": v(-106.75, 121.84) * mm, "radius": 0.5 * mm});
            skCircle(sketch, "E1.39.13.0", {"center": v(-106.75, 124.38) * mm, "radius": 0.5 * mm});
            skCircle(sketch, "E1.39.14.0", {"center": v(-106.75, 126.92) * mm, "radius": 0.5 * mm});
            skCircle(sketch, "E1.39.15.0", {"center": v(-106.75, 129.46) * mm, "radius": 0.5 * mm});
            skCircle(sketch, "E1.39.16.0", {"center": v(-106.75, 132) * mm, "radius": 0.5 * mm});
            skCircle(sketch, "E1.39.17.0", {"center": v(-106.75, 134.54) * mm, "radius": 0.5 * mm});
            skCircle(sketch, "E1.39.18.0", {"center": v(-106.75, 137.08) * mm, "radius": 0.5 * mm});
            skCircle(sketch, "E1.39.19.0", {"center": v(-106.75, 139.62) * mm, "radius": 0.5 * mm});
            skCircle(sketch, "E1.39.20.0", {"center": v(-106.75, 142.16) * mm, "radius": 0.5 * mm});
            skCircle(sketch, "E1.39.21.0", {"center": v(-106.75, 144.7) * mm, "radius": 0.5 * mm});
            skCircle(sketch, "E1.39.22.0", {"center": v(-106.75, 147.24) * mm, "radius": 0.5 * mm});
            skCircle(sketch, "E1.39.23.0", {"center": v(-106.75, 149.78) * mm, "radius": 0.5 * mm});
            skCircle(sketch, "E1.39.24.0", {"center": v(-106.75, 152.32) * mm, "radius": 0.5 * mm});
            skCircle(sketch, "E1.39.25.0", {"center": v(-106.75, 154.86) * mm, "radius": 0.5 * mm});
            skCircle(sketch, "E1.39.26.0", {"center": v(-106.75, 157.4) * mm, "radius": 0.5 * mm});
            skCircle(sketch, "E1.39.27.0", {"center": v(-106.75, 159.94) * mm, "radius": 0.5 * mm});
            skCircle(sketch, "E1.39.28.0", {"center": v(-106.75, 162.48) * mm, "radius": 0.5 * mm});
            skCircle(sketch, "E1.39.29.0", {"center": v(-106.75, 165.02) * mm, "radius": 0.5 * mm});
            skCircle(sketch, "E1.39.30.0", {"center": v(-106.75, 167.56) * mm, "radius": 0.5 * mm});
            skCircle(sketch, "E1.39.31.0", {"center": v(-106.75, 170.1) * mm, "radius": 0.5 * mm});
            skCircle(sketch, "E1.39.32.0", {"center": v(-106.75, 172.64) * mm, "radius": 0.5 * mm});
            skCircle(sketch, "E1.39.33.0", {"center": v(-106.75, 175.18) * mm, "radius": 0.5 * mm});
            skCircle(sketch, "E1.39.34.0", {"center": v(-106.75, 177.72) * mm, "radius": 0.5 * mm});
            skCircle(sketch, "E1.39.35.0", {"center": v(-106.75, 180.26) * mm, "radius": 0.5 * mm});
            skCircle(sketch, "E1.39.36.0", {"center": v(-106.75, 182.8) * mm, "radius": 0.5 * mm});
            skCircle(sketch, "E1.39.37.0", {"center": v(-106.75, 185.34) * mm, "radius": 0.5 * mm});
            skCircle(sketch, "E1.40.0.0", {"center": v(-104.2, 91.36) * mm, "radius": 0.5 * mm});
            skCircle(sketch, "E1.40.1.0", {"center": v(-104.2, 93.9) * mm, "radius": 0.5 * mm});
            skCircle(sketch, "E1.40.2.0", {"center": v(-104.2, 96.44) * mm, "radius": 0.5 * mm});
            skCircle(sketch, "E1.40.3.0", {"center": v(-104.2, 98.98) * mm, "radius": 0.5 * mm});
            skCircle(sketch, "E1.40.4.0", {"center": v(-104.2, 101.52) * mm, "radius": 0.5 * mm});
            skCircle(sketch, "E1.40.5.0", {"center": v(-104.2, 104.06) * mm, "radius": 0.5 * mm});
            skCircle(sketch, "E1.40.6.0", {"center": v(-104.2, 106.6) * mm, "radius": 0.5 * mm});
            skCircle(sketch, "E1.40.7.0", {"center": v(-104.2, 109.14) * mm, "radius": 0.5 * mm});
            skCircle(sketch, "E1.40.8.0", {"center": v(-104.2, 111.68) * mm, "radius": 0.5 * mm});
            skCircle(sketch, "E1.40.9.0", {"center": v(-104.2, 114.22) * mm, "radius": 0.5 * mm});
            skCircle(sketch, "E1.40.10.0", {"center": v(-104.2, 116.76) * mm, "radius": 0.5 * mm});
            skCircle(sketch, "E1.40.11.0", {"center": v(-104.2, 119.3) * mm, "radius": 0.5 * mm});
            skCircle(sketch, "E1.40.12.0", {"center": v(-104.2, 121.84) * mm, "radius": 0.5 * mm});
            skCircle(sketch, "E1.40.13.0", {"center": v(-104.2, 124.38) * mm, "radius": 0.5 * mm});
            skCircle(sketch, "E1.40.14.0", {"center": v(-104.2, 126.92) * mm, "radius": 0.5 * mm});
            skCircle(sketch, "E1.40.15.0", {"center": v(-104.2, 129.46) * mm, "radius": 0.5 * mm});
            skCircle(sketch, "E1.40.16.0", {"center": v(-104.2, 132) * mm, "radius": 0.5 * mm});
            skCircle(sketch, "E1.40.17.0", {"center": v(-104.2, 134.54) * mm, "radius": 0.5 * mm});
            skCircle(sketch, "E1.40.18.0", {"center": v(-104.2, 137.08) * mm, "radius": 0.5 * mm});
            skCircle(sketch, "E1.40.19.0", {"center": v(-104.2, 139.62) * mm, "radius": 0.5 * mm});
            skCircle(sketch, "E1.40.20.0", {"center": v(-104.2, 142.16) * mm, "radius": 0.5 * mm});
            skCircle(sketch, "E1.40.21.0", {"center": v(-104.2, 144.7) * mm, "radius": 0.5 * mm});
            skCircle(sketch, "E1.40.22.0", {"center": v(-104.2, 147.24) * mm, "radius": 0.5 * mm});
            skCircle(sketch, "E1.40.23.0", {"center": v(-104.2, 149.78) * mm, "radius": 0.5 * mm});
            skCircle(sketch, "E1.40.24.0", {"center": v(-104.2, 152.32) * mm, "radius": 0.5 * mm});
            skCircle(sketch, "E1.40.25.0", {"center": v(-104.2, 154.86) * mm, "radius": 0.5 * mm});
            skCircle(sketch, "E1.40.26.0", {"center": v(-104.2, 157.4) * mm, "radius": 0.5 * mm});
            skCircle(sketch, "E1.40.27.0", {"center": v(-104.2, 159.94) * mm, "radius": 0.5 * mm});
            skCircle(sketch, "E1.40.28.0", {"center": v(-104.2, 162.48) * mm, "radius": 0.5 * mm});
            skCircle(sketch, "E1.40.29.0", {"center": v(-104.2, 165.02) * mm, "radius": 0.5 * mm});
            skCircle(sketch, "E1.40.30.0", {"center": v(-104.2, 167.56) * mm, "radius": 0.5 * mm});
            skCircle(sketch, "E1.40.31.0", {"center": v(-104.2, 170.1) * mm, "radius": 0.5 * mm});
            skCircle(sketch, "E1.40.32.0", {"center": v(-104.2, 172.64) * mm, "radius": 0.5 * mm});
            skCircle(sketch, "E1.40.33.0", {"center": v(-104.2, 175.18) * mm, "radius": 0.5 * mm});
            skCircle(sketch, "E1.40.34.0", {"center": v(-104.2, 177.72) * mm, "radius": 0.5 * mm});
            skCircle(sketch, "E1.40.35.0", {"center": v(-104.2, 180.26) * mm, "radius": 0.5 * mm});
            skCircle(sketch, "E1.40.36.0", {"center": v(-104.2, 182.8) * mm, "radius": 0.5 * mm});
            skCircle(sketch, "E1.40.37.0", {"center": v(-104.2, 185.34) * mm, "radius": 0.5 * mm});
            skCircle(sketch, "E1.41.0.0", {"center": v(-101.67, 91.36) * mm, "radius": 0.5 * mm});
            skCircle(sketch, "E1.41.1.0", {"center": v(-101.67, 93.9) * mm, "radius": 0.5 * mm});
            skCircle(sketch, "E1.41.2.0", {"center": v(-101.67, 96.44) * mm, "radius": 0.5 * mm});
            skCircle(sketch, "E1.41.3.0", {"center": v(-101.67, 98.98) * mm, "radius": 0.5 * mm});
            skCircle(sketch, "E1.41.4.0", {"center": v(-101.67, 101.52) * mm, "radius": 0.5 * mm});
            skCircle(sketch, "E1.41.5.0", {"center": v(-101.67, 104.06) * mm, "radius": 0.5 * mm});
            skCircle(sketch, "E1.41.6.0", {"center": v(-101.67, 106.6) * mm, "radius": 0.5 * mm});
            skCircle(sketch, "E1.41.7.0", {"center": v(-101.67, 109.14) * mm, "radius": 0.5 * mm});
            skCircle(sketch, "E1.41.8.0", {"center": v(-101.67, 111.68) * mm, "radius": 0.5 * mm});
            skCircle(sketch, "E1.41.9.0", {"center": v(-101.67, 114.22) * mm, "radius": 0.5 * mm});
            skCircle(sketch, "E1.41.10.0", {"center": v(-101.67, 116.76) * mm, "radius": 0.5 * mm});
            skCircle(sketch, "E1.41.11.0", {"center": v(-101.67, 119.3) * mm, "radius": 0.5 * mm});
            skCircle(sketch, "E1.41.12.0", {"center": v(-101.67, 121.84) * mm, "radius": 0.5 * mm});
            skCircle(sketch, "E1.41.13.0", {"center": v(-101.67, 124.38) * mm, "radius": 0.5 * mm});
            skCircle(sketch, "E1.41.14.0", {"center": v(-101.67, 126.92) * mm, "radius": 0.5 * mm});
            skCircle(sketch, "E1.41.15.0", {"center": v(-101.67, 129.46) * mm, "radius": 0.5 * mm});
            skCircle(sketch, "E1.41.16.0", {"center": v(-101.67, 132) * mm, "radius": 0.5 * mm});
            skCircle(sketch, "E1.41.17.0", {"center": v(-101.67, 134.54) * mm, "radius": 0.5 * mm});
            skCircle(sketch, "E1.41.18.0", {"center": v(-101.67, 137.08) * mm, "radius": 0.5 * mm});
            skCircle(sketch, "E1.41.19.0", {"center": v(-101.67, 139.62) * mm, "radius": 0.5 * mm});
            skCircle(sketch, "E1.41.20.0", {"center": v(-101.67, 142.16) * mm, "radius": 0.5 * mm});
            skCircle(sketch, "E1.41.21.0", {"center": v(-101.67, 144.7) * mm, "radius": 0.5 * mm});
            skCircle(sketch, "E1.41.22.0", {"center": v(-101.67, 147.24) * mm, "radius": 0.5 * mm});
            skCircle(sketch, "E1.41.23.0", {"center": v(-101.67, 149.78) * mm, "radius": 0.5 * mm});
            skCircle(sketch, "E1.41.24.0", {"center": v(-101.67, 152.32) * mm, "radius": 0.5 * mm});
            skCircle(sketch, "E1.41.25.0", {"center": v(-101.67, 154.86) * mm, "radius": 0.5 * mm});
            skCircle(sketch, "E1.41.26.0", {"center": v(-101.67, 157.4) * mm, "radius": 0.5 * mm});
            skCircle(sketch, "E1.41.27.0", {"center": v(-101.67, 159.94) * mm, "radius": 0.5 * mm});
            skCircle(sketch, "E1.41.28.0", {"center": v(-101.67, 162.48) * mm, "radius": 0.5 * mm});
            skCircle(sketch, "E1.41.29.0", {"center": v(-101.67, 165.02) * mm, "radius": 0.5 * mm});
            skCircle(sketch, "E1.41.30.0", {"center": v(-101.67, 167.56) * mm, "radius": 0.5 * mm});
            skCircle(sketch, "E1.41.31.0", {"center": v(-101.67, 170.1) * mm, "radius": 0.5 * mm});
            skCircle(sketch, "E1.41.32.0", {"center": v(-101.67, 172.64) * mm, "radius": 0.5 * mm});
            skCircle(sketch, "E1.41.33.0", {"center": v(-101.67, 175.18) * mm, "radius": 0.5 * mm});
            skCircle(sketch, "E1.41.34.0", {"center": v(-101.67, 177.72) * mm, "radius": 0.5 * mm});
            skCircle(sketch, "E1.41.35.0", {"center": v(-101.67, 180.26) * mm, "radius": 0.5 * mm});
            skCircle(sketch, "E1.41.36.0", {"center": v(-101.67, 182.8) * mm, "radius": 0.5 * mm});
            skCircle(sketch, "E1.41.37.0", {"center": v(-101.67, 185.34) * mm, "radius": 0.5 * mm});
            skCircle(sketch, "E1.42.0.0", {"center": v(-99.13, 91.36) * mm, "radius": 0.5 * mm});
            skCircle(sketch, "E1.42.1.0", {"center": v(-99.13, 93.9) * mm, "radius": 0.5 * mm});
            skCircle(sketch, "E1.42.2.0", {"center": v(-99.13, 96.44) * mm, "radius": 0.5 * mm});
            skCircle(sketch, "E1.42.3.0", {"center": v(-99.13, 98.98) * mm, "radius": 0.5 * mm});
            skCircle(sketch, "E1.42.4.0", {"center": v(-99.13, 101.52) * mm, "radius": 0.5 * mm});
            skCircle(sketch, "E1.42.5.0", {"center": v(-99.13, 104.06) * mm, "radius": 0.5 * mm});
            skCircle(sketch, "E1.42.6.0", {"center": v(-99.13, 106.6) * mm, "radius": 0.5 * mm});
            skCircle(sketch, "E1.42.7.0", {"center": v(-99.13, 109.14) * mm, "radius": 0.5 * mm});
            skCircle(sketch, "E1.42.8.0", {"center": v(-99.13, 111.68) * mm, "radius": 0.5 * mm});
            skCircle(sketch, "E1.42.9.0", {"center": v(-99.13, 114.22) * mm, "radius": 0.5 * mm});
            skCircle(sketch, "E1.42.10.0", {"center": v(-99.13, 116.76) * mm, "radius": 0.5 * mm});
            skCircle(sketch, "E1.42.11.0", {"center": v(-99.13, 119.3) * mm, "radius": 0.5 * mm});
            skCircle(sketch, "E1.42.12.0", {"center": v(-99.13, 121.84) * mm, "radius": 0.5 * mm});
            skCircle(sketch, "E1.42.13.0", {"center": v(-99.13, 124.38) * mm, "radius": 0.5 * mm});
            skCircle(sketch, "E1.42.14.0", {"center": v(-99.13, 126.92) * mm, "radius": 0.5 * mm});
            skCircle(sketch, "E1.42.15.0", {"center": v(-99.13, 129.46) * mm, "radius": 0.5 * mm});
            skCircle(sketch, "E1.42.16.0", {"center": v(-99.13, 132) * mm, "radius": 0.5 * mm});
            skCircle(sketch, "E1.42.17.0", {"center": v(-99.13, 134.54) * mm, "radius": 0.5 * mm});
            skCircle(sketch, "E1.42.18.0", {"center": v(-99.13, 137.08) * mm, "radius": 0.5 * mm});
            skCircle(sketch, "E1.42.19.0", {"center": v(-99.13, 139.62) * mm, "radius": 0.5 * mm});
            skCircle(sketch, "E1.42.20.0", {"center": v(-99.13, 142.16) * mm, "radius": 0.5 * mm});
            skCircle(sketch, "E1.42.21.0", {"center": v(-99.13, 144.7) * mm, "radius": 0.5 * mm});
            skCircle(sketch, "E1.42.22.0", {"center": v(-99.13, 147.24) * mm, "radius": 0.5 * mm});
            skCircle(sketch, "E1.42.23.0", {"center": v(-99.13, 149.78) * mm, "radius": 0.5 * mm});
            skCircle(sketch, "E1.42.24.0", {"center": v(-99.13, 152.32) * mm, "radius": 0.5 * mm});
            skCircle(sketch, "E1.42.25.0", {"center": v(-99.13, 154.86) * mm, "radius": 0.5 * mm});
            skCircle(sketch, "E1.42.26.0", {"center": v(-99.13, 157.4) * mm, "radius": 0.5 * mm});
            skCircle(sketch, "E1.42.27.0", {"center": v(-99.13, 159.94) * mm, "radius": 0.5 * mm});
            skCircle(sketch, "E1.42.28.0", {"center": v(-99.13, 162.48) * mm, "radius": 0.5 * mm});
            skCircle(sketch, "E1.42.29.0", {"center": v(-99.13, 165.02) * mm, "radius": 0.5 * mm});
            skCircle(sketch, "E1.42.30.0", {"center": v(-99.13, 167.56) * mm, "radius": 0.5 * mm});
            skCircle(sketch, "E1.42.31.0", {"center": v(-99.13, 170.1) * mm, "radius": 0.5 * mm});
            skCircle(sketch, "E1.42.32.0", {"center": v(-99.13, 172.64) * mm, "radius": 0.5 * mm});
            skCircle(sketch, "E1.42.33.0", {"center": v(-99.13, 175.18) * mm, "radius": 0.5 * mm});
            skCircle(sketch, "E1.42.34.0", {"center": v(-99.13, 177.72) * mm, "radius": 0.5 * mm});
            skCircle(sketch, "E1.42.35.0", {"center": v(-99.13, 180.26) * mm, "radius": 0.5 * mm});
            skCircle(sketch, "E1.42.36.0", {"center": v(-99.13, 182.8) * mm, "radius": 0.5 * mm});
            skCircle(sketch, "E1.42.37.0", {"center": v(-99.13, 185.34) * mm, "radius": 0.5 * mm});
            skCircle(sketch, "E1.43.0.0", {"center": v(-96.59, 91.36) * mm, "radius": 0.5 * mm});
            skCircle(sketch, "E1.43.1.0", {"center": v(-96.59, 93.9) * mm, "radius": 0.5 * mm});
            skCircle(sketch, "E1.43.2.0", {"center": v(-96.59, 96.44) * mm, "radius": 0.5 * mm});
            skCircle(sketch, "E1.43.3.0", {"center": v(-96.59, 98.98) * mm, "radius": 0.5 * mm});
            skCircle(sketch, "E1.43.4.0", {"center": v(-96.59, 101.52) * mm, "radius": 0.5 * mm});
            skCircle(sketch, "E1.43.5.0", {"center": v(-96.59, 104.06) * mm, "radius": 0.5 * mm});
            skCircle(sketch, "E1.43.6.0", {"center": v(-96.59, 106.6) * mm, "radius": 0.5 * mm});
            skCircle(sketch, "E1.43.7.0", {"center": v(-96.59, 109.14) * mm, "radius": 0.5 * mm});
            skCircle(sketch, "E1.43.8.0", {"center": v(-96.59, 111.68) * mm, "radius": 0.5 * mm});
            skCircle(sketch, "E1.43.9.0", {"center": v(-96.59, 114.22) * mm, "radius": 0.5 * mm});
            skCircle(sketch, "E1.43.10.0", {"center": v(-96.59, 116.76) * mm, "radius": 0.5 * mm});
            skCircle(sketch, "E1.43.11.0", {"center": v(-96.59, 119.3) * mm, "radius": 0.5 * mm});
            skCircle(sketch, "E1.43.12.0", {"center": v(-96.59, 121.84) * mm, "radius": 0.5 * mm});
            skCircle(sketch, "E1.43.13.0", {"center": v(-96.59, 124.38) * mm, "radius": 0.5 * mm});
            skCircle(sketch, "E1.43.14.0", {"center": v(-96.59, 126.92) * mm, "radius": 0.5 * mm});
            skCircle(sketch, "E1.43.15.0", {"center": v(-96.59, 129.46) * mm, "radius": 0.5 * mm});
            skCircle(sketch, "E1.43.16.0", {"center": v(-96.59, 132) * mm, "radius": 0.5 * mm});
            skCircle(sketch, "E1.43.17.0", {"center": v(-96.59, 134.54) * mm, "radius": 0.5 * mm});
            skCircle(sketch, "E1.43.18.0", {"center": v(-96.59, 137.08) * mm, "radius": 0.5 * mm});
            skCircle(sketch, "E1.43.19.0", {"center": v(-96.59, 139.62) * mm, "radius": 0.5 * mm});
            skCircle(sketch, "E1.43.20.0", {"center": v(-96.59, 142.16) * mm, "radius": 0.5 * mm});
            skCircle(sketch, "E1.43.21.0", {"center": v(-96.59, 144.7) * mm, "radius": 0.5 * mm});
            skCircle(sketch, "E1.43.22.0", {"center": v(-96.59, 147.24) * mm, "radius": 0.5 * mm});
            skCircle(sketch, "E1.43.23.0", {"center": v(-96.59, 149.78) * mm, "radius": 0.5 * mm});
            skCircle(sketch, "E1.43.24.0", {"center": v(-96.59, 152.32) * mm, "radius": 0.5 * mm});
            skCircle(sketch, "E1.43.25.0", {"center": v(-96.59, 154.86) * mm, "radius": 0.5 * mm});
            skCircle(sketch, "E1.43.26.0", {"center": v(-96.59, 157.4) * mm, "radius": 0.5 * mm});
            skCircle(sketch, "E1.43.27.0", {"center": v(-96.59, 159.94) * mm, "radius": 0.5 * mm});
            skCircle(sketch, "E1.43.28.0", {"center": v(-96.59, 162.48) * mm, "radius": 0.5 * mm});
            skCircle(sketch, "E1.43.29.0", {"center": v(-96.59, 165.02) * mm, "radius": 0.5 * mm});
            skCircle(sketch, "E1.43.30.0", {"center": v(-96.59, 167.56) * mm, "radius": 0.5 * mm});
            skCircle(sketch, "E1.43.31.0", {"center": v(-96.59, 170.1) * mm, "radius": 0.5 * mm});
            skCircle(sketch, "E1.43.32.0", {"center": v(-96.59, 172.64) * mm, "radius": 0.5 * mm});
            skCircle(sketch, "E1.43.33.0", {"center": v(-96.59, 175.18) * mm, "radius": 0.5 * mm});
            skCircle(sketch, "E1.43.34.0", {"center": v(-96.59, 177.72) * mm, "radius": 0.5 * mm});
            skCircle(sketch, "E1.43.35.0", {"center": v(-96.59, 180.26) * mm, "radius": 0.5 * mm});
            skCircle(sketch, "E1.43.36.0", {"center": v(-96.59, 182.8) * mm, "radius": 0.5 * mm});
            skCircle(sketch, "E1.43.37.0", {"center": v(-96.59, 185.34) * mm, "radius": 0.5 * mm});
            skCircle(sketch, "E1.44.0.0", {"center": v(-94.05, 91.36) * mm, "radius": 0.5 * mm});
            skCircle(sketch, "E1.44.1.0", {"center": v(-94.05, 93.9) * mm, "radius": 0.5 * mm});
            skCircle(sketch, "E1.44.2.0", {"center": v(-94.05, 96.44) * mm, "radius": 0.5 * mm});
            skCircle(sketch, "E1.44.3.0", {"center": v(-94.05, 98.98) * mm, "radius": 0.5 * mm});
            skCircle(sketch, "E1.44.4.0", {"center": v(-94.05, 101.52) * mm, "radius": 0.5 * mm});
            skCircle(sketch, "E1.44.5.0", {"center": v(-94.05, 104.06) * mm, "radius": 0.5 * mm});
            skCircle(sketch, "E1.44.6.0", {"center": v(-94.05, 106.6) * mm, "radius": 0.5 * mm});
            skCircle(sketch, "E1.44.7.0", {"center": v(-94.05, 109.14) * mm, "radius": 0.5 * mm});
            skCircle(sketch, "E1.44.8.0", {"center": v(-94.05, 111.68) * mm, "radius": 0.5 * mm});
            skCircle(sketch, "E1.44.9.0", {"center": v(-94.05, 114.22) * mm, "radius": 0.5 * mm});
            skCircle(sketch, "E1.44.10.0", {"center": v(-94.05, 116.76) * mm, "radius": 0.5 * mm});
            skCircle(sketch, "E1.44.11.0", {"center": v(-94.05, 119.3) * mm, "radius": 0.5 * mm});
            skCircle(sketch, "E1.44.12.0", {"center": v(-94.05, 121.84) * mm, "radius": 0.5 * mm});
            skCircle(sketch, "E1.44.13.0", {"center": v(-94.05, 124.38) * mm, "radius": 0.5 * mm});
            skCircle(sketch, "E1.44.14.0", {"center": v(-94.05, 126.92) * mm, "radius": 0.5 * mm});
            skCircle(sketch, "E1.44.15.0", {"center": v(-94.05, 129.46) * mm, "radius": 0.5 * mm});
            skCircle(sketch, "E1.44.16.0", {"center": v(-94.05, 132) * mm, "radius": 0.5 * mm});
            skCircle(sketch, "E1.44.17.0", {"center": v(-94.05, 134.54) * mm, "radius": 0.5 * mm});
            skCircle(sketch, "E1.44.18.0", {"center": v(-94.05, 137.08) * mm, "radius": 0.5 * mm});
            skCircle(sketch, "E1.44.19.0", {"center": v(-94.05, 139.62) * mm, "radius": 0.5 * mm});
            skCircle(sketch, "E1.44.20.0", {"center": v(-94.05, 142.16) * mm, "radius": 0.5 * mm});
            skCircle(sketch, "E1.44.21.0", {"center": v(-94.05, 144.7) * mm, "radius": 0.5 * mm});
            skCircle(sketch, "E1.44.22.0", {"center": v(-94.05, 147.24) * mm, "radius": 0.5 * mm});
            skCircle(sketch, "E1.44.23.0", {"center": v(-94.05, 149.78) * mm, "radius": 0.5 * mm});
            skCircle(sketch, "E1.44.24.0", {"center": v(-94.05, 152.32) * mm, "radius": 0.5 * mm});
            skCircle(sketch, "E1.44.25.0", {"center": v(-94.05, 154.86) * mm, "radius": 0.5 * mm});
            skCircle(sketch, "E1.44.26.0", {"center": v(-94.05, 157.4) * mm, "radius": 0.5 * mm});
            skCircle(sketch, "E1.44.27.0", {"center": v(-94.05, 159.94) * mm, "radius": 0.5 * mm});
            skCircle(sketch, "E1.44.28.0", {"center": v(-94.05, 162.48) * mm, "radius": 0.5 * mm});
            skCircle(sketch, "E1.44.29.0", {"center": v(-94.05, 165.02) * mm, "radius": 0.5 * mm});
            skCircle(sketch, "E1.44.30.0", {"center": v(-94.05, 167.56) * mm, "radius": 0.5 * mm});
            skCircle(sketch, "E1.44.31.0", {"center": v(-94.05, 170.1) * mm, "radius": 0.5 * mm});
            skCircle(sketch, "E1.44.32.0", {"center": v(-94.05, 172.64) * mm, "radius": 0.5 * mm});
            skCircle(sketch, "E1.44.33.0", {"center": v(-94.05, 175.18) * mm, "radius": 0.5 * mm});
            skCircle(sketch, "E1.44.34.0", {"center": v(-94.05, 177.72) * mm, "radius": 0.5 * mm});
            skCircle(sketch, "E1.44.35.0", {"center": v(-94.05, 180.26) * mm, "radius": 0.5 * mm});
            skCircle(sketch, "E1.44.36.0", {"center": v(-94.05, 182.8) * mm, "radius": 0.5 * mm});
            skCircle(sketch, "E1.44.37.0", {"center": v(-94.05, 185.34) * mm, "radius": 0.5 * mm});
            skCircle(sketch, "E1.45.0.0", {"center": v(-91.5, 91.36) * mm, "radius": 0.5 * mm});
            skCircle(sketch, "E1.45.1.0", {"center": v(-91.5, 93.9) * mm, "radius": 0.5 * mm});
            skCircle(sketch, "E1.45.2.0", {"center": v(-91.5, 96.44) * mm, "radius": 0.5 * mm});
            skCircle(sketch, "E1.45.3.0", {"center": v(-91.5, 98.98) * mm, "radius": 0.5 * mm});
            skCircle(sketch, "E1.45.4.0", {"center": v(-91.5, 101.52) * mm, "radius": 0.5 * mm});
            skCircle(sketch, "E1.45.5.0", {"center": v(-91.5, 104.06) * mm, "radius": 0.5 * mm});
            skCircle(sketch, "E1.45.6.0", {"center": v(-91.5, 106.6) * mm, "radius": 0.5 * mm});
            skCircle(sketch, "E1.45.7.0", {"center": v(-91.5, 109.14) * mm, "radius": 0.5 * mm});
            skCircle(sketch, "E1.45.8.0", {"center": v(-91.5, 111.68) * mm, "radius": 0.5 * mm});
            skCircle(sketch, "E1.45.9.0", {"center": v(-91.5, 114.22) * mm, "radius": 0.5 * mm});
            skCircle(sketch, "E1.45.10.0", {"center": v(-91.5, 116.76) * mm, "radius": 0.5 * mm});
            skCircle(sketch, "E1.45.11.0", {"center": v(-91.5, 119.3) * mm, "radius": 0.5 * mm});
            skCircle(sketch, "E1.45.12.0", {"center": v(-91.5, 121.84) * mm, "radius": 0.5 * mm});
            skCircle(sketch, "E1.45.13.0", {"center": v(-91.5, 124.38) * mm, "radius": 0.5 * mm});
            skCircle(sketch, "E1.45.14.0", {"center": v(-91.5, 126.92) * mm, "radius": 0.5 * mm});
            skCircle(sketch, "E1.45.15.0", {"center": v(-91.5, 129.46) * mm, "radius": 0.5 * mm});
            skCircle(sketch, "E1.45.16.0", {"center": v(-91.5, 132) * mm, "radius": 0.5 * mm});
            skCircle(sketch, "E1.45.17.0", {"center": v(-91.5, 134.54) * mm, "radius": 0.5 * mm});
            skCircle(sketch, "E1.45.18.0", {"center": v(-91.5, 137.08) * mm, "radius": 0.5 * mm});
            skCircle(sketch, "E1.45.19.0", {"center": v(-91.5, 139.62) * mm, "radius": 0.5 * mm});
            skCircle(sketch, "E1.45.20.0", {"center": v(-91.5, 142.16) * mm, "radius": 0.5 * mm});
            skCircle(sketch, "E1.45.21.0", {"center": v(-91.5, 144.7) * mm, "radius": 0.5 * mm});
            skCircle(sketch, "E1.45.22.0", {"center": v(-91.5, 147.24) * mm, "radius": 0.5 * mm});
            skCircle(sketch, "E1.45.23.0", {"center": v(-91.5, 149.78) * mm, "radius": 0.5 * mm});
            skCircle(sketch, "E1.45.24.0", {"center": v(-91.5, 152.32) * mm, "radius": 0.5 * mm});
            skCircle(sketch, "E1.45.25.0", {"center": v(-91.5, 154.86) * mm, "radius": 0.5 * mm});
            skCircle(sketch, "E1.45.26.0", {"center": v(-91.5, 157.4) * mm, "radius": 0.5 * mm});
            skCircle(sketch, "E1.45.27.0", {"center": v(-91.5, 159.94) * mm, "radius": 0.5 * mm});
            skCircle(sketch, "E1.45.28.0", {"center": v(-91.5, 162.48) * mm, "radius": 0.5 * mm});
            skCircle(sketch, "E1.45.29.0", {"center": v(-91.5, 165.02) * mm, "radius": 0.5 * mm});
            skCircle(sketch, "E1.45.30.0", {"center": v(-91.5, 167.56) * mm, "radius": 0.5 * mm});
            skCircle(sketch, "E1.45.31.0", {"center": v(-91.5, 170.1) * mm, "radius": 0.5 * mm});
            skCircle(sketch, "E1.45.32.0", {"center": v(-91.5, 172.64) * mm, "radius": 0.5 * mm});
            skCircle(sketch, "E1.45.33.0", {"center": v(-91.5, 175.18) * mm, "radius": 0.5 * mm});
            skCircle(sketch, "E1.45.34.0", {"center": v(-91.5, 177.72) * mm, "radius": 0.5 * mm});
            skCircle(sketch, "E1.45.35.0", {"center": v(-91.5, 180.26) * mm, "radius": 0.5 * mm});
            skCircle(sketch, "E1.45.36.0", {"center": v(-91.5, 182.8) * mm, "radius": 0.5 * mm});
            skCircle(sketch, "E1.45.37.0", {"center": v(-91.5, 185.34) * mm, "radius": 0.5 * mm});
            skCircle(sketch, "E1.46.0.0", {"center": v(-88.97, 91.36) * mm, "radius": 0.5 * mm});
            skCircle(sketch, "E1.46.1.0", {"center": v(-88.97, 93.9) * mm, "radius": 0.5 * mm});
            skCircle(sketch, "E1.46.2.0", {"center": v(-88.97, 96.44) * mm, "radius": 0.5 * mm});
            skCircle(sketch, "E1.46.3.0", {"center": v(-88.97, 98.98) * mm, "radius": 0.5 * mm});
            skCircle(sketch, "E1.46.4.0", {"center": v(-88.97, 101.52) * mm, "radius": 0.5 * mm});
            skCircle(sketch, "E1.46.5.0", {"center": v(-88.97, 104.06) * mm, "radius": 0.5 * mm});
            skCircle(sketch, "E1.46.6.0", {"center": v(-88.97, 106.6) * mm, "radius": 0.5 * mm});
            skCircle(sketch, "E1.46.7.0", {"center": v(-88.97, 109.14) * mm, "radius": 0.5 * mm});
            skCircle(sketch, "E1.46.8.0", {"center": v(-88.97, 111.68) * mm, "radius": 0.5 * mm});
            skCircle(sketch, "E1.46.9.0", {"center": v(-88.97, 114.22) * mm, "radius": 0.5 * mm});
            skCircle(sketch, "E1.46.10.0", {"center": v(-88.97, 116.76) * mm, "radius": 0.5 * mm});
            skCircle(sketch, "E1.46.11.0", {"center": v(-88.97, 119.3) * mm, "radius": 0.5 * mm});
            skCircle(sketch, "E1.46.12.0", {"center": v(-88.97, 121.84) * mm, "radius": 0.5 * mm});
            skCircle(sketch, "E1.46.13.0", {"center": v(-88.97, 124.38) * mm, "radius": 0.5 * mm});
            skCircle(sketch, "E1.46.14.0", {"center": v(-88.97, 126.92) * mm, "radius": 0.5 * mm});
            skCircle(sketch, "E1.46.15.0", {"center": v(-88.97, 129.46) * mm, "radius": 0.5 * mm});
            skCircle(sketch, "E1.46.16.0", {"center": v(-88.97, 132) * mm, "radius": 0.5 * mm});
            skCircle(sketch, "E1.46.17.0", {"center": v(-88.97, 134.54) * mm, "radius": 0.5 * mm});
            skCircle(sketch, "E1.46.18.0", {"center": v(-88.97, 137.08) * mm, "radius": 0.5 * mm});
            skCircle(sketch, "E1.46.19.0", {"center": v(-88.97, 139.62) * mm, "radius": 0.5 * mm});
            skCircle(sketch, "E1.46.20.0", {"center": v(-88.97, 142.16) * mm, "radius": 0.5 * mm});
            skCircle(sketch, "E1.46.21.0", {"center": v(-88.97, 144.7) * mm, "radius": 0.5 * mm});
            skCircle(sketch, "E1.46.22.0", {"center": v(-88.97, 147.24) * mm, "radius": 0.5 * mm});
            skCircle(sketch, "E1.46.23.0", {"center": v(-88.97, 149.78) * mm, "radius": 0.5 * mm});
            skCircle(sketch, "E1.46.24.0", {"center": v(-88.97, 152.32) * mm, "radius": 0.5 * mm});
            skCircle(sketch, "E1.46.25.0", {"center": v(-88.97, 154.86) * mm, "radius": 0.5 * mm});
            skCircle(sketch, "E1.46.26.0", {"center": v(-88.97, 157.4) * mm, "radius": 0.5 * mm});
            skCircle(sketch, "E1.46.27.0", {"center": v(-88.97, 159.94) * mm, "radius": 0.5 * mm});
            skCircle(sketch, "E1.46.28.0", {"center": v(-88.97, 162.48) * mm, "radius": 0.5 * mm});
            skCircle(sketch, "E1.46.29.0", {"center": v(-88.97, 165.02) * mm, "radius": 0.5 * mm});
            skCircle(sketch, "E1.46.30.0", {"center": v(-88.97, 167.56) * mm, "radius": 0.5 * mm});
            skCircle(sketch, "E1.46.31.0", {"center": v(-88.97, 170.1) * mm, "radius": 0.5 * mm});
            skCircle(sketch, "E1.46.32.0", {"center": v(-88.97, 172.64) * mm, "radius": 0.5 * mm});
            skCircle(sketch, "E1.46.33.0", {"center": v(-88.97, 175.18) * mm, "radius": 0.5 * mm});
            skCircle(sketch, "E1.46.34.0", {"center": v(-88.97, 177.72) * mm, "radius": 0.5 * mm});
            skCircle(sketch, "E1.46.35.0", {"center": v(-88.97, 180.26) * mm, "radius": 0.5 * mm});
            skCircle(sketch, "E1.46.36.0", {"center": v(-88.97, 182.8) * mm, "radius": 0.5 * mm});
            skCircle(sketch, "E1.46.37.0", {"center": v(-88.97, 185.34) * mm, "radius": 0.5 * mm});
            skCircle(sketch, "E1.47.0.0", {"center": v(-86.43, 91.36) * mm, "radius": 0.5 * mm});
            skCircle(sketch, "E1.47.1.0", {"center": v(-86.43, 93.9) * mm, "radius": 0.5 * mm});
            skCircle(sketch, "E1.47.2.0", {"center": v(-86.43, 96.44) * mm, "radius": 0.5 * mm});
            skCircle(sketch, "E1.47.3.0", {"center": v(-86.43, 98.98) * mm, "radius": 0.5 * mm});
            skCircle(sketch, "E1.47.4.0", {"center": v(-86.43, 101.52) * mm, "radius": 0.5 * mm});
            skCircle(sketch, "E1.47.5.0", {"center": v(-86.43, 104.06) * mm, "radius": 0.5 * mm});
            skCircle(sketch, "E1.47.6.0", {"center": v(-86.43, 106.6) * mm, "radius": 0.5 * mm});
            skCircle(sketch, "E1.47.7.0", {"center": v(-86.43, 109.14) * mm, "radius": 0.5 * mm});
            skCircle(sketch, "E1.47.8.0", {"center": v(-86.43, 111.68) * mm, "radius": 0.5 * mm});
            skCircle(sketch, "E1.47.9.0", {"center": v(-86.43, 114.22) * mm, "radius": 0.5 * mm});
            skCircle(sketch, "E1.47.10.0", {"center": v(-86.43, 116.76) * mm, "radius": 0.5 * mm});
            skCircle(sketch, "E1.47.11.0", {"center": v(-86.43, 119.3) * mm, "radius": 0.5 * mm});
            skCircle(sketch, "E1.47.12.0", {"center": v(-86.43, 121.84) * mm, "radius": 0.5 * mm});
            skCircle(sketch, "E1.47.13.0", {"center": v(-86.43, 124.38) * mm, "radius": 0.5 * mm});
            skCircle(sketch, "E1.47.14.0", {"center": v(-86.43, 126.92) * mm, "radius": 0.5 * mm});
            skCircle(sketch, "E1.47.15.0", {"center": v(-86.43, 129.46) * mm, "radius": 0.5 * mm});
            skCircle(sketch, "E1.47.16.0", {"center": v(-86.43, 132) * mm, "radius": 0.5 * mm});
            skCircle(sketch, "E1.47.17.0", {"center": v(-86.43, 134.54) * mm, "radius": 0.5 * mm});
            skCircle(sketch, "E1.47.18.0", {"center": v(-86.43, 137.08) * mm, "radius": 0.5 * mm});
            skCircle(sketch, "E1.47.19.0", {"center": v(-86.43, 139.62) * mm, "radius": 0.5 * mm});
            skCircle(sketch, "E1.47.20.0", {"center": v(-86.43, 142.16) * mm, "radius": 0.5 * mm});
            skCircle(sketch, "E1.47.21.0", {"center": v(-86.43, 144.7) * mm, "radius": 0.5 * mm});
            skCircle(sketch, "E1.47.22.0", {"center": v(-86.43, 147.24) * mm, "radius": 0.5 * mm});
            skCircle(sketch, "E1.47.23.0", {"center": v(-86.43, 149.78) * mm, "radius": 0.5 * mm});
            skCircle(sketch, "E1.47.24.0", {"center": v(-86.43, 152.32) * mm, "radius": 0.5 * mm});
            skCircle(sketch, "E1.47.25.0", {"center": v(-86.43, 154.86) * mm, "radius": 0.5 * mm});
            skCircle(sketch, "E1.47.26.0", {"center": v(-86.43, 157.4) * mm, "radius": 0.5 * mm});
            skCircle(sketch, "E1.47.27.0", {"center": v(-86.43, 159.94) * mm, "radius": 0.5 * mm});
            skCircle(sketch, "E1.47.28.0", {"center": v(-86.43, 162.48) * mm, "radius": 0.5 * mm});
            skCircle(sketch, "E1.47.29.0", {"center": v(-86.43, 165.02) * mm, "radius": 0.5 * mm});
            skCircle(sketch, "E1.47.30.0", {"center": v(-86.43, 167.56) * mm, "radius": 0.5 * mm});
            skCircle(sketch, "E1.47.31.0", {"center": v(-86.43, 170.1) * mm, "radius": 0.5 * mm});
            skCircle(sketch, "E1.47.32.0", {"center": v(-86.43, 172.64) * mm, "radius": 0.5 * mm});
            skCircle(sketch, "E1.47.33.0", {"center": v(-86.43, 175.18) * mm, "radius": 0.5 * mm});
            skCircle(sketch, "E1.47.34.0", {"center": v(-86.43, 177.72) * mm, "radius": 0.5 * mm});
            skCircle(sketch, "E1.47.35.0", {"center": v(-86.43, 180.26) * mm, "radius": 0.5 * mm});
            skCircle(sketch, "E1.47.36.0", {"center": v(-86.43, 182.8) * mm, "radius": 0.5 * mm});
            skCircle(sketch, "E1.47.37.0", {"center": v(-86.43, 185.34) * mm, "radius": 0.5 * mm});
            skCircle(sketch, "E1.48.0.0", {"center": v(-83.89, 91.36) * mm, "radius": 0.5 * mm});
            skCircle(sketch, "E1.48.1.0", {"center": v(-83.89, 93.9) * mm, "radius": 0.5 * mm});
            skCircle(sketch, "E1.48.2.0", {"center": v(-83.89, 96.44) * mm, "radius": 0.5 * mm});
            skCircle(sketch, "E1.48.3.0", {"center": v(-83.89, 98.98) * mm, "radius": 0.5 * mm});
            skCircle(sketch, "E1.48.4.0", {"center": v(-83.89, 101.52) * mm, "radius": 0.5 * mm});
            skCircle(sketch, "E1.48.5.0", {"center": v(-83.89, 104.06) * mm, "radius": 0.5 * mm});
            skCircle(sketch, "E1.48.6.0", {"center": v(-83.89, 106.6) * mm, "radius": 0.5 * mm});
            skCircle(sketch, "E1.48.7.0", {"center": v(-83.89, 109.14) * mm, "radius": 0.5 * mm});
            skCircle(sketch, "E1.48.8.0", {"center": v(-83.89, 111.68) * mm, "radius": 0.5 * mm});
            skCircle(sketch, "E1.48.9.0", {"center": v(-83.89, 114.22) * mm, "radius": 0.5 * mm});
            skCircle(sketch, "E1.48.10.0", {"center": v(-83.89, 116.76) * mm, "radius": 0.5 * mm});
            skCircle(sketch, "E1.48.11.0", {"center": v(-83.89, 119.3) * mm, "radius": 0.5 * mm});
            skCircle(sketch, "E1.48.12.0", {"center": v(-83.89, 121.84) * mm, "radius": 0.5 * mm});
            skCircle(sketch, "E1.48.13.0", {"center": v(-83.89, 124.38) * mm, "radius": 0.5 * mm});
            skCircle(sketch, "E1.48.14.0", {"center": v(-83.89, 126.92) * mm, "radius": 0.5 * mm});
            skCircle(sketch, "E1.48.15.0", {"center": v(-83.89, 129.46) * mm, "radius": 0.5 * mm});
            skCircle(sketch, "E1.48.16.0", {"center": v(-83.89, 132) * mm, "radius": 0.5 * mm});
            skCircle(sketch, "E1.48.17.0", {"center": v(-83.89, 134.54) * mm, "radius": 0.5 * mm});
            skCircle(sketch, "E1.48.18.0", {"center": v(-83.89, 137.08) * mm, "radius": 0.5 * mm});
            skCircle(sketch, "E1.48.19.0", {"center": v(-83.89, 139.62) * mm, "radius": 0.5 * mm});
            skCircle(sketch, "E1.48.20.0", {"center": v(-83.89, 142.16) * mm, "radius": 0.5 * mm});
            skCircle(sketch, "E1.48.21.0", {"center": v(-83.89, 144.7) * mm, "radius": 0.5 * mm});
            skCircle(sketch, "E1.48.22.0", {"center": v(-83.89, 147.24) * mm, "radius": 0.5 * mm});
            skCircle(sketch, "E1.48.23.0", {"center": v(-83.89, 149.78) * mm, "radius": 0.5 * mm});
            skCircle(sketch, "E1.48.24.0", {"center": v(-83.89, 152.32) * mm, "radius": 0.5 * mm});
            skCircle(sketch, "E1.48.25.0", {"center": v(-83.89, 154.86) * mm, "radius": 0.5 * mm});
            skCircle(sketch, "E1.48.26.0", {"center": v(-83.89, 157.4) * mm, "radius": 0.5 * mm});
            skCircle(sketch, "E1.48.27.0", {"center": v(-83.89, 159.94) * mm, "radius": 0.5 * mm});
            skCircle(sketch, "E1.48.28.0", {"center": v(-83.89, 162.48) * mm, "radius": 0.5 * mm});
            skCircle(sketch, "E1.48.29.0", {"center": v(-83.89, 165.02) * mm, "radius": 0.5 * mm});
            skCircle(sketch, "E1.48.30.0", {"center": v(-83.89, 167.56) * mm, "radius": 0.5 * mm});
            skCircle(sketch, "E1.48.31.0", {"center": v(-83.89, 170.1) * mm, "radius": 0.5 * mm});
            skCircle(sketch, "E1.48.32.0", {"center": v(-83.89, 172.64) * mm, "radius": 0.5 * mm});
            skCircle(sketch, "E1.48.33.0", {"center": v(-83.89, 175.18) * mm, "radius": 0.5 * mm});
            skCircle(sketch, "E1.48.34.0", {"center": v(-83.89, 177.72) * mm, "radius": 0.5 * mm});
            skCircle(sketch, "E1.48.35.0", {"center": v(-83.89, 180.26) * mm, "radius": 0.5 * mm});
            skCircle(sketch, "E1.48.36.0", {"center": v(-83.89, 182.8) * mm, "radius": 0.5 * mm});
            skCircle(sketch, "E1.48.37.0", {"center": v(-83.89, 185.34) * mm, "radius": 0.5 * mm});
            skCircle(sketch, "E1.49.0.0", {"center": v(-81.35, 91.36) * mm, "radius": 0.5 * mm});
            skCircle(sketch, "E1.49.1.0", {"center": v(-81.35, 93.9) * mm, "radius": 0.5 * mm});
            skCircle(sketch, "E1.49.2.0", {"center": v(-81.35, 96.44) * mm, "radius": 0.5 * mm});
            skCircle(sketch, "E1.49.3.0", {"center": v(-81.35, 98.98) * mm, "radius": 0.5 * mm});
            skCircle(sketch, "E1.49.4.0", {"center": v(-81.35, 101.52) * mm, "radius": 0.5 * mm});
            skCircle(sketch, "E1.49.5.0", {"center": v(-81.35, 104.06) * mm, "radius": 0.5 * mm});
            skCircle(sketch, "E1.49.6.0", {"center": v(-81.35, 106.6) * mm, "radius": 0.5 * mm});
            skCircle(sketch, "E1.49.7.0", {"center": v(-81.35, 109.14) * mm, "radius": 0.5 * mm});
            skCircle(sketch, "E1.49.8.0", {"center": v(-81.35, 111.68) * mm, "radius": 0.5 * mm});
            skCircle(sketch, "E1.49.9.0", {"center": v(-81.35, 114.22) * mm, "radius": 0.5 * mm});
            skCircle(sketch, "E1.49.10.0", {"center": v(-81.35, 116.76) * mm, "radius": 0.5 * mm});
            skCircle(sketch, "E1.49.11.0", {"center": v(-81.35, 119.3) * mm, "radius": 0.5 * mm});
            skCircle(sketch, "E1.49.12.0", {"center": v(-81.35, 121.84) * mm, "radius": 0.5 * mm});
            skCircle(sketch, "E1.49.13.0", {"center": v(-81.35, 124.38) * mm, "radius": 0.5 * mm});
            skCircle(sketch, "E1.49.14.0", {"center": v(-81.35, 126.92) * mm, "radius": 0.5 * mm});
            skCircle(sketch, "E1.49.15.0", {"center": v(-81.35, 129.46) * mm, "radius": 0.5 * mm});
            skCircle(sketch, "E1.49.16.0", {"center": v(-81.35, 132) * mm, "radius": 0.5 * mm});
            skCircle(sketch, "E1.49.17.0", {"center": v(-81.35, 134.54) * mm, "radius": 0.5 * mm});
            skCircle(sketch, "E1.49.18.0", {"center": v(-81.35, 137.08) * mm, "radius": 0.5 * mm});
            skCircle(sketch, "E1.49.19.0", {"center": v(-81.35, 139.62) * mm, "radius": 0.5 * mm});
            skCircle(sketch, "E1.49.20.0", {"center": v(-81.35, 142.16) * mm, "radius": 0.5 * mm});
            skCircle(sketch, "E1.49.21.0", {"center": v(-81.35, 144.7) * mm, "radius": 0.5 * mm});
            skCircle(sketch, "E1.49.22.0", {"center": v(-81.35, 147.24) * mm, "radius": 0.5 * mm});
            skCircle(sketch, "E1.49.23.0", {"center": v(-81.35, 149.78) * mm, "radius": 0.5 * mm});
            skCircle(sketch, "E1.49.24.0", {"center": v(-81.35, 152.32) * mm, "radius": 0.5 * mm});
            skCircle(sketch, "E1.49.25.0", {"center": v(-81.35, 154.86) * mm, "radius": 0.5 * mm});
            skCircle(sketch, "E1.49.26.0", {"center": v(-81.35, 157.4) * mm, "radius": 0.5 * mm});
            skCircle(sketch, "E1.49.27.0", {"center": v(-81.35, 159.94) * mm, "radius": 0.5 * mm});
            skCircle(sketch, "E1.49.28.0", {"center": v(-81.35, 162.48) * mm, "radius": 0.5 * mm});
            skCircle(sketch, "E1.49.29.0", {"center": v(-81.35, 165.02) * mm, "radius": 0.5 * mm});
            skCircle(sketch, "E1.49.30.0", {"center": v(-81.35, 167.56) * mm, "radius": 0.5 * mm});
            skCircle(sketch, "E1.49.31.0", {"center": v(-81.35, 170.1) * mm, "radius": 0.5 * mm});
            skCircle(sketch, "E1.49.32.0", {"center": v(-81.35, 172.64) * mm, "radius": 0.5 * mm});
            skCircle(sketch, "E1.49.33.0", {"center": v(-81.35, 175.18) * mm, "radius": 0.5 * mm});
            skCircle(sketch, "E1.49.34.0", {"center": v(-81.35, 177.72) * mm, "radius": 0.5 * mm});
            skCircle(sketch, "E1.49.35.0", {"center": v(-81.35, 180.26) * mm, "radius": 0.5 * mm});
            skCircle(sketch, "E1.49.36.0", {"center": v(-81.35, 182.8) * mm, "radius": 0.5 * mm});
            skCircle(sketch, "E1.49.37.0", {"center": v(-81.35, 185.34) * mm, "radius": 0.5 * mm});
            skCircle(sketch, "E1.50.0.0", {"center": v(-78.8, 91.36) * mm, "radius": 0.5 * mm});
            skCircle(sketch, "E1.50.1.0", {"center": v(-78.8, 93.9) * mm, "radius": 0.5 * mm});
            skCircle(sketch, "E1.50.2.0", {"center": v(-78.8, 96.44) * mm, "radius": 0.5 * mm});
            skCircle(sketch, "E1.50.3.0", {"center": v(-78.8, 98.98) * mm, "radius": 0.5 * mm});
            skCircle(sketch, "E1.50.4.0", {"center": v(-78.8, 101.52) * mm, "radius": 0.5 * mm});
            skCircle(sketch, "E1.50.5.0", {"center": v(-78.8, 104.06) * mm, "radius": 0.5 * mm});
            skCircle(sketch, "E1.50.6.0", {"center": v(-78.8, 106.6) * mm, "radius": 0.5 * mm});
            skCircle(sketch, "E1.50.7.0", {"center": v(-78.8, 109.14) * mm, "radius": 0.5 * mm});
            skCircle(sketch, "E1.50.8.0", {"center": v(-78.8, 111.68) * mm, "radius": 0.5 * mm});
            skCircle(sketch, "E1.50.9.0", {"center": v(-78.8, 114.22) * mm, "radius": 0.5 * mm});
            skCircle(sketch, "E1.50.10.0", {"center": v(-78.8, 116.76) * mm, "radius": 0.5 * mm});
            skCircle(sketch, "E1.50.11.0", {"center": v(-78.8, 119.3) * mm, "radius": 0.5 * mm});
            skCircle(sketch, "E1.50.12.0", {"center": v(-78.8, 121.84) * mm, "radius": 0.5 * mm});
            skCircle(sketch, "E1.50.13.0", {"center": v(-78.8, 124.38) * mm, "radius": 0.5 * mm});
            skCircle(sketch, "E1.50.14.0", {"center": v(-78.8, 126.92) * mm, "radius": 0.5 * mm});
            skCircle(sketch, "E1.50.15.0", {"center": v(-78.8, 129.46) * mm, "radius": 0.5 * mm});
            skCircle(sketch, "E1.50.16.0", {"center": v(-78.8, 132) * mm, "radius": 0.5 * mm});
            skCircle(sketch, "E1.50.17.0", {"center": v(-78.8, 134.54) * mm, "radius": 0.5 * mm});
            skCircle(sketch, "E1.50.18.0", {"center": v(-78.8, 137.08) * mm, "radius": 0.5 * mm});
            skCircle(sketch, "E1.50.19.0", {"center": v(-78.8, 139.62) * mm, "radius": 0.5 * mm});
            skCircle(sketch, "E1.50.20.0", {"center": v(-78.8, 142.16) * mm, "radius": 0.5 * mm});
            skCircle(sketch, "E1.50.21.0", {"center": v(-78.8, 144.7) * mm, "radius": 0.5 * mm});
            skCircle(sketch, "E1.50.22.0", {"center": v(-78.8, 147.24) * mm, "radius": 0.5 * mm});
            skCircle(sketch, "E1.50.23.0", {"center": v(-78.8, 149.78) * mm, "radius": 0.5 * mm});
            skCircle(sketch, "E1.50.24.0", {"center": v(-78.8, 152.32) * mm, "radius": 0.5 * mm});
            skCircle(sketch, "E1.50.25.0", {"center": v(-78.8, 154.86) * mm, "radius": 0.5 * mm});
            skCircle(sketch, "E1.50.26.0", {"center": v(-78.8, 157.4) * mm, "radius": 0.5 * mm});
            skCircle(sketch, "E1.50.27.0", {"center": v(-78.8, 159.94) * mm, "radius": 0.5 * mm});
            skCircle(sketch, "E1.50.28.0", {"center": v(-78.8, 162.48) * mm, "radius": 0.5 * mm});
            skCircle(sketch, "E1.50.29.0", {"center": v(-78.8, 165.02) * mm, "radius": 0.5 * mm});
            skCircle(sketch, "E1.50.30.0", {"center": v(-78.8, 167.56) * mm, "radius": 0.5 * mm});
            skCircle(sketch, "E1.50.31.0", {"center": v(-78.8, 170.1) * mm, "radius": 0.5 * mm});
            skCircle(sketch, "E1.50.32.0", {"center": v(-78.8, 172.64) * mm, "radius": 0.5 * mm});
            skCircle(sketch, "E1.50.33.0", {"center": v(-78.8, 175.18) * mm, "radius": 0.5 * mm});
            skCircle(sketch, "E1.50.34.0", {"center": v(-78.8, 177.72) * mm, "radius": 0.5 * mm});
            skCircle(sketch, "E1.50.35.0", {"center": v(-78.8, 180.26) * mm, "radius": 0.5 * mm});
            skCircle(sketch, "E1.50.36.0", {"center": v(-78.8, 182.8) * mm, "radius": 0.5 * mm});
            skCircle(sketch, "E1.50.37.0", {"center": v(-78.8, 185.34) * mm, "radius": 0.5 * mm});
            skCircle(sketch, "E1.51.0.0", {"center": v(-76.27, 91.36) * mm, "radius": 0.5 * mm});
            skCircle(sketch, "E1.51.1.0", {"center": v(-76.27, 93.9) * mm, "radius": 0.5 * mm});
            skCircle(sketch, "E1.51.2.0", {"center": v(-76.27, 96.44) * mm, "radius": 0.5 * mm});
            skCircle(sketch, "E1.51.3.0", {"center": v(-76.27, 98.98) * mm, "radius": 0.5 * mm});
            skCircle(sketch, "E1.51.4.0", {"center": v(-76.27, 101.52) * mm, "radius": 0.5 * mm});
            skCircle(sketch, "E1.51.5.0", {"center": v(-76.27, 104.06) * mm, "radius": 0.5 * mm});
            skCircle(sketch, "E1.51.6.0", {"center": v(-76.27, 106.6) * mm, "radius": 0.5 * mm});
            skCircle(sketch, "E1.51.7.0", {"center": v(-76.27, 109.14) * mm, "radius": 0.5 * mm});
            skCircle(sketch, "E1.51.8.0", {"center": v(-76.27, 111.68) * mm, "radius": 0.5 * mm});
            skCircle(sketch, "E1.51.9.0", {"center": v(-76.27, 114.22) * mm, "radius": 0.5 * mm});
            skCircle(sketch, "E1.51.10.0", {"center": v(-76.27, 116.76) * mm, "radius": 0.5 * mm});
            skCircle(sketch, "E1.51.11.0", {"center": v(-76.27, 119.3) * mm, "radius": 0.5 * mm});
            skCircle(sketch, "E1.51.12.0", {"center": v(-76.27, 121.84) * mm, "radius": 0.5 * mm});
            skCircle(sketch, "E1.51.13.0", {"center": v(-76.27, 124.38) * mm, "radius": 0.5 * mm});
            skCircle(sketch, "E1.51.14.0", {"center": v(-76.27, 126.92) * mm, "radius": 0.5 * mm});
            skCircle(sketch, "E1.51.15.0", {"center": v(-76.27, 129.46) * mm, "radius": 0.5 * mm});
            skCircle(sketch, "E1.51.16.0", {"center": v(-76.27, 132) * mm, "radius": 0.5 * mm});
            skCircle(sketch, "E1.51.17.0", {"center": v(-76.27, 134.54) * mm, "radius": 0.5 * mm});
            skCircle(sketch, "E1.51.18.0", {"center": v(-76.27, 137.08) * mm, "radius": 0.5 * mm});
            skCircle(sketch, "E1.51.19.0", {"center": v(-76.27, 139.62) * mm, "radius": 0.5 * mm});
            skCircle(sketch, "E1.51.20.0", {"center": v(-76.27, 142.16) * mm, "radius": 0.5 * mm});
            skCircle(sketch, "E1.51.21.0", {"center": v(-76.27, 144.7) * mm, "radius": 0.5 * mm});
            skCircle(sketch, "E1.51.22.0", {"center": v(-76.27, 147.24) * mm, "radius": 0.5 * mm});
            skCircle(sketch, "E1.51.23.0", {"center": v(-76.27, 149.78) * mm, "radius": 0.5 * mm});
            skCircle(sketch, "E1.51.24.0", {"center": v(-76.27, 152.32) * mm, "radius": 0.5 * mm});
            skCircle(sketch, "E1.51.25.0", {"center": v(-76.27, 154.86) * mm, "radius": 0.5 * mm});
            skCircle(sketch, "E1.51.26.0", {"center": v(-76.27, 157.4) * mm, "radius": 0.5 * mm});
            skCircle(sketch, "E1.51.27.0", {"center": v(-76.27, 159.94) * mm, "radius": 0.5 * mm});
            skCircle(sketch, "E1.51.28.0", {"center": v(-76.27, 162.48) * mm, "radius": 0.5 * mm});
            skCircle(sketch, "E1.51.29.0", {"center": v(-76.27, 165.02) * mm, "radius": 0.5 * mm});
            skCircle(sketch, "E1.51.30.0", {"center": v(-76.27, 167.56) * mm, "radius": 0.5 * mm});
            skCircle(sketch, "E1.51.31.0", {"center": v(-76.27, 170.1) * mm, "radius": 0.5 * mm});
            skCircle(sketch, "E1.51.32.0", {"center": v(-76.27, 172.64) * mm, "radius": 0.5 * mm});
            skCircle(sketch, "E1.51.33.0", {"center": v(-76.27, 175.18) * mm, "radius": 0.5 * mm});
            skCircle(sketch, "E1.51.34.0", {"center": v(-76.27, 177.72) * mm, "radius": 0.5 * mm});
            skCircle(sketch, "E1.51.35.0", {"center": v(-76.27, 180.26) * mm, "radius": 0.5 * mm});
            skCircle(sketch, "E1.51.36.0", {"center": v(-76.27, 182.8) * mm, "radius": 0.5 * mm});
            skCircle(sketch, "E1.51.37.0", {"center": v(-76.27, 185.34) * mm, "radius": 0.5 * mm});
            skCircle(sketch, "E1.52.0.0", {"center": v(-73.73, 91.36) * mm, "radius": 0.5 * mm});
            skCircle(sketch, "E1.52.1.0", {"center": v(-73.73, 93.9) * mm, "radius": 0.5 * mm});
            skCircle(sketch, "E1.52.2.0", {"center": v(-73.73, 96.44) * mm, "radius": 0.5 * mm});
            skCircle(sketch, "E1.52.3.0", {"center": v(-73.73, 98.98) * mm, "radius": 0.5 * mm});
            skCircle(sketch, "E1.52.4.0", {"center": v(-73.73, 101.52) * mm, "radius": 0.5 * mm});
            skCircle(sketch, "E1.52.5.0", {"center": v(-73.73, 104.06) * mm, "radius": 0.5 * mm});
            skCircle(sketch, "E1.52.6.0", {"center": v(-73.73, 106.6) * mm, "radius": 0.5 * mm});
            skCircle(sketch, "E1.52.7.0", {"center": v(-73.73, 109.14) * mm, "radius": 0.5 * mm});
            skCircle(sketch, "E1.52.8.0", {"center": v(-73.73, 111.68) * mm, "radius": 0.5 * mm});
            skCircle(sketch, "E1.52.9.0", {"center": v(-73.73, 114.22) * mm, "radius": 0.5 * mm});
            skCircle(sketch, "E1.52.10.0", {"center": v(-73.73, 116.76) * mm, "radius": 0.5 * mm});
            skCircle(sketch, "E1.52.11.0", {"center": v(-73.73, 119.3) * mm, "radius": 0.5 * mm});
            skCircle(sketch, "E1.52.12.0", {"center": v(-73.73, 121.84) * mm, "radius": 0.5 * mm});
            skCircle(sketch, "E1.52.13.0", {"center": v(-73.73, 124.38) * mm, "radius": 0.5 * mm});
            skCircle(sketch, "E1.52.14.0", {"center": v(-73.73, 126.92) * mm, "radius": 0.5 * mm});
            skCircle(sketch, "E1.52.15.0", {"center": v(-73.73, 129.46) * mm, "radius": 0.5 * mm});
            skCircle(sketch, "E1.52.16.0", {"center": v(-73.73, 132) * mm, "radius": 0.5 * mm});
            skCircle(sketch, "E1.52.17.0", {"center": v(-73.73, 134.54) * mm, "radius": 0.5 * mm});
            skCircle(sketch, "E1.52.18.0", {"center": v(-73.73, 137.08) * mm, "radius": 0.5 * mm});
            skCircle(sketch, "E1.52.19.0", {"center": v(-73.73, 139.62) * mm, "radius": 0.5 * mm});
            skCircle(sketch, "E1.52.20.0", {"center": v(-73.73, 142.16) * mm, "radius": 0.5 * mm});
            skCircle(sketch, "E1.52.21.0", {"center": v(-73.73, 144.7) * mm, "radius": 0.5 * mm});
            skCircle(sketch, "E1.52.22.0", {"center": v(-73.73, 147.24) * mm, "radius": 0.5 * mm});
            skCircle(sketch, "E1.52.23.0", {"center": v(-73.73, 149.78) * mm, "radius": 0.5 * mm});
            skCircle(sketch, "E1.52.24.0", {"center": v(-73.73, 152.32) * mm, "radius": 0.5 * mm});
            skCircle(sketch, "E1.52.25.0", {"center": v(-73.73, 154.86) * mm, "radius": 0.5 * mm});
            skCircle(sketch, "E1.52.26.0", {"center": v(-73.73, 157.4) * mm, "radius": 0.5 * mm});
            skCircle(sketch, "E1.52.27.0", {"center": v(-73.73, 159.94) * mm, "radius": 0.5 * mm});
            skCircle(sketch, "E1.52.28.0", {"center": v(-73.73, 162.48) * mm, "radius": 0.5 * mm});
            skCircle(sketch, "E1.52.29.0", {"center": v(-73.73, 165.02) * mm, "radius": 0.5 * mm});
            skCircle(sketch, "E1.52.30.0", {"center": v(-73.73, 167.56) * mm, "radius": 0.5 * mm});
            skCircle(sketch, "E1.52.31.0", {"center": v(-73.73, 170.1) * mm, "radius": 0.5 * mm});
            skCircle(sketch, "E1.52.32.0", {"center": v(-73.73, 172.64) * mm, "radius": 0.5 * mm});
            skCircle(sketch, "E1.52.33.0", {"center": v(-73.73, 175.18) * mm, "radius": 0.5 * mm});
            skCircle(sketch, "E1.52.34.0", {"center": v(-73.73, 177.72) * mm, "radius": 0.5 * mm});
            skCircle(sketch, "E1.52.35.0", {"center": v(-73.73, 180.26) * mm, "radius": 0.5 * mm});
            skCircle(sketch, "E1.52.36.0", {"center": v(-73.73, 182.8) * mm, "radius": 0.5 * mm});
            skCircle(sketch, "E1.52.37.0", {"center": v(-73.73, 185.34) * mm, "radius": 0.5 * mm});
            skCircle(sketch, "E1.53.0.0", {"center": v(-71.19, 91.36) * mm, "radius": 0.5 * mm});
            skCircle(sketch, "E1.53.1.0", {"center": v(-71.19, 93.9) * mm, "radius": 0.5 * mm});
            skCircle(sketch, "E1.53.2.0", {"center": v(-71.19, 96.44) * mm, "radius": 0.5 * mm});
            skCircle(sketch, "E1.53.3.0", {"center": v(-71.19, 98.98) * mm, "radius": 0.5 * mm});
            skCircle(sketch, "E1.53.4.0", {"center": v(-71.19, 101.52) * mm, "radius": 0.5 * mm});
            skCircle(sketch, "E1.53.5.0", {"center": v(-71.19, 104.06) * mm, "radius": 0.5 * mm});
            skCircle(sketch, "E1.53.6.0", {"center": v(-71.19, 106.6) * mm, "radius": 0.5 * mm});
            skCircle(sketch, "E1.53.7.0", {"center": v(-71.19, 109.14) * mm, "radius": 0.5 * mm});
            skCircle(sketch, "E1.53.8.0", {"center": v(-71.19, 111.68) * mm, "radius": 0.5 * mm});
            skCircle(sketch, "E1.53.9.0", {"center": v(-71.19, 114.22) * mm, "radius": 0.5 * mm});
            skCircle(sketch, "E1.53.10.0", {"center": v(-71.19, 116.76) * mm, "radius": 0.5 * mm});
            skCircle(sketch, "E1.53.11.0", {"center": v(-71.19, 119.3) * mm, "radius": 0.5 * mm});
            skCircle(sketch, "E1.53.12.0", {"center": v(-71.19, 121.84) * mm, "radius": 0.5 * mm});
            skCircle(sketch, "E1.53.13.0", {"center": v(-71.19, 124.38) * mm, "radius": 0.5 * mm});
            skCircle(sketch, "E1.53.14.0", {"center": v(-71.19, 126.92) * mm, "radius": 0.5 * mm});
            skCircle(sketch, "E1.53.15.0", {"center": v(-71.19, 129.46) * mm, "radius": 0.5 * mm});
            skCircle(sketch, "E1.53.16.0", {"center": v(-71.19, 132) * mm, "radius": 0.5 * mm});
            skCircle(sketch, "E1.53.17.0", {"center": v(-71.19, 134.54) * mm, "radius": 0.5 * mm});
            skCircle(sketch, "E1.53.18.0", {"center": v(-71.19, 137.08) * mm, "radius": 0.5 * mm});
            skCircle(sketch, "E1.53.19.0", {"center": v(-71.19, 139.62) * mm, "radius": 0.5 * mm});
            skCircle(sketch, "E1.53.20.0", {"center": v(-71.19, 142.16) * mm, "radius": 0.5 * mm});
            skCircle(sketch, "E1.53.21.0", {"center": v(-71.19, 144.7) * mm, "radius": 0.5 * mm});
            skCircle(sketch, "E1.53.22.0", {"center": v(-71.19, 147.24) * mm, "radius": 0.5 * mm});
            skCircle(sketch, "E1.53.23.0", {"center": v(-71.19, 149.78) * mm, "radius": 0.5 * mm});
            skCircle(sketch, "E1.53.24.0", {"center": v(-71.19, 152.32) * mm, "radius": 0.5 * mm});
            skCircle(sketch, "E1.53.25.0", {"center": v(-71.19, 154.86) * mm, "radius": 0.5 * mm});
            skCircle(sketch, "E1.53.26.0", {"center": v(-71.19, 157.4) * mm, "radius": 0.5 * mm});
            skCircle(sketch, "E1.53.27.0", {"center": v(-71.19, 159.94) * mm, "radius": 0.5 * mm});
            skCircle(sketch, "E1.53.28.0", {"center": v(-71.19, 162.48) * mm, "radius": 0.5 * mm});
            skCircle(sketch, "E1.53.29.0", {"center": v(-71.19, 165.02) * mm, "radius": 0.5 * mm});
            skCircle(sketch, "E1.53.30.0", {"center": v(-71.19, 167.56) * mm, "radius": 0.5 * mm});
            skCircle(sketch, "E1.53.31.0", {"center": v(-71.19, 170.1) * mm, "radius": 0.5 * mm});
            skCircle(sketch, "E1.53.32.0", {"center": v(-71.19, 172.64) * mm, "radius": 0.5 * mm});
            skCircle(sketch, "E1.53.33.0", {"center": v(-71.19, 175.18) * mm, "radius": 0.5 * mm});
            skCircle(sketch, "E1.53.34.0", {"center": v(-71.19, 177.72) * mm, "radius": 0.5 * mm});
            skCircle(sketch, "E1.53.35.0", {"center": v(-71.19, 180.26) * mm, "radius": 0.5 * mm});
            skCircle(sketch, "E1.53.36.0", {"center": v(-71.19, 182.8) * mm, "radius": 0.5 * mm});
            skCircle(sketch, "E1.53.37.0", {"center": v(-71.19, 185.34) * mm, "radius": 0.5 * mm});
            skCircle(sketch, "E1.54.0.0", {"center": v(-68.65, 91.36) * mm, "radius": 0.5 * mm});
            skCircle(sketch, "E1.54.1.0", {"center": v(-68.65, 93.9) * mm, "radius": 0.5 * mm});
            skCircle(sketch, "E1.54.2.0", {"center": v(-68.65, 96.44) * mm, "radius": 0.5 * mm});
            skCircle(sketch, "E1.54.3.0", {"center": v(-68.65, 98.98) * mm, "radius": 0.5 * mm});
            skCircle(sketch, "E1.54.4.0", {"center": v(-68.65, 101.52) * mm, "radius": 0.5 * mm});
            skCircle(sketch, "E1.54.5.0", {"center": v(-68.65, 104.06) * mm, "radius": 0.5 * mm});
            skCircle(sketch, "E1.54.6.0", {"center": v(-68.65, 106.6) * mm, "radius": 0.5 * mm});
            skCircle(sketch, "E1.54.7.0", {"center": v(-68.65, 109.14) * mm, "radius": 0.5 * mm});
            skCircle(sketch, "E1.54.8.0", {"center": v(-68.65, 111.68) * mm, "radius": 0.5 * mm});
            skCircle(sketch, "E1.54.9.0", {"center": v(-68.65, 114.22) * mm, "radius": 0.5 * mm});
            skCircle(sketch, "E1.54.10.0", {"center": v(-68.65, 116.76) * mm, "radius": 0.5 * mm});
            skCircle(sketch, "E1.54.11.0", {"center": v(-68.65, 119.3) * mm, "radius": 0.5 * mm});
            skCircle(sketch, "E1.54.12.0", {"center": v(-68.65, 121.84) * mm, "radius": 0.5 * mm});
            skCircle(sketch, "E1.54.13.0", {"center": v(-68.65, 124.38) * mm, "radius": 0.5 * mm});
            skCircle(sketch, "E1.54.14.0", {"center": v(-68.65, 126.92) * mm, "radius": 0.5 * mm});
            skCircle(sketch, "E1.54.15.0", {"center": v(-68.65, 129.46) * mm, "radius": 0.5 * mm});
            skCircle(sketch, "E1.54.16.0", {"center": v(-68.65, 132) * mm, "radius": 0.5 * mm});
            skCircle(sketch, "E1.54.17.0", {"center": v(-68.65, 134.54) * mm, "radius": 0.5 * mm});
            skCircle(sketch, "E1.54.18.0", {"center": v(-68.65, 137.08) * mm, "radius": 0.5 * mm});
            skCircle(sketch, "E1.54.19.0", {"center": v(-68.65, 139.62) * mm, "radius": 0.5 * mm});
            skCircle(sketch, "E1.54.20.0", {"center": v(-68.65, 142.16) * mm, "radius": 0.5 * mm});
            skCircle(sketch, "E1.54.21.0", {"center": v(-68.65, 144.7) * mm, "radius": 0.5 * mm});
            skCircle(sketch, "E1.54.22.0", {"center": v(-68.65, 147.24) * mm, "radius": 0.5 * mm});
            skCircle(sketch, "E1.54.23.0", {"center": v(-68.65, 149.78) * mm, "radius": 0.5 * mm});
            skCircle(sketch, "E1.54.24.0", {"center": v(-68.65, 152.32) * mm, "radius": 0.5 * mm});
            skCircle(sketch, "E1.54.25.0", {"center": v(-68.65, 154.86) * mm, "radius": 0.5 * mm});
            skCircle(sketch, "E1.54.26.0", {"center": v(-68.65, 157.4) * mm, "radius": 0.5 * mm});
            skCircle(sketch, "E1.54.27.0", {"center": v(-68.65, 159.94) * mm, "radius": 0.5 * mm});
            skCircle(sketch, "E1.54.28.0", {"center": v(-68.65, 162.48) * mm, "radius": 0.5 * mm});
            skCircle(sketch, "E1.54.29.0", {"center": v(-68.65, 165.02) * mm, "radius": 0.5 * mm});
            skCircle(sketch, "E1.54.30.0", {"center": v(-68.65, 167.56) * mm, "radius": 0.5 * mm});
            skCircle(sketch, "E1.54.31.0", {"center": v(-68.65, 170.1) * mm, "radius": 0.5 * mm});
            skCircle(sketch, "E1.54.32.0", {"center": v(-68.65, 172.64) * mm, "radius": 0.5 * mm});
            skCircle(sketch, "E1.54.33.0", {"center": v(-68.65, 175.18) * mm, "radius": 0.5 * mm});
            skCircle(sketch, "E1.54.34.0", {"center": v(-68.65, 177.72) * mm, "radius": 0.5 * mm});
            skCircle(sketch, "E1.54.35.0", {"center": v(-68.65, 180.26) * mm, "radius": 0.5 * mm});
            skCircle(sketch, "E1.54.36.0", {"center": v(-68.65, 182.8) * mm, "radius": 0.5 * mm});
            skCircle(sketch, "E1.54.37.0", {"center": v(-68.65, 185.34) * mm, "radius": 0.5 * mm});
            skCircle(sketch, "E1.55.0.0", {"center": v(-66.1, 91.36) * mm, "radius": 0.5 * mm});
            skCircle(sketch, "E1.55.1.0", {"center": v(-66.1, 93.9) * mm, "radius": 0.5 * mm});
            skCircle(sketch, "E1.55.2.0", {"center": v(-66.1, 96.44) * mm, "radius": 0.5 * mm});
            skCircle(sketch, "E1.55.3.0", {"center": v(-66.1, 98.98) * mm, "radius": 0.5 * mm});
            skCircle(sketch, "E1.55.4.0", {"center": v(-66.1, 101.52) * mm, "radius": 0.5 * mm});
            skCircle(sketch, "E1.55.5.0", {"center": v(-66.1, 104.06) * mm, "radius": 0.5 * mm});
            skCircle(sketch, "E1.55.6.0", {"center": v(-66.1, 106.6) * mm, "radius": 0.5 * mm});
            skCircle(sketch, "E1.55.7.0", {"center": v(-66.1, 109.14) * mm, "radius": 0.5 * mm});
            skCircle(sketch, "E1.55.8.0", {"center": v(-66.1, 111.68) * mm, "radius": 0.5 * mm});
            skCircle(sketch, "E1.55.9.0", {"center": v(-66.1, 114.22) * mm, "radius": 0.5 * mm});
            skCircle(sketch, "E1.55.10.0", {"center": v(-66.1, 116.76) * mm, "radius": 0.5 * mm});
            skCircle(sketch, "E1.55.11.0", {"center": v(-66.1, 119.3) * mm, "radius": 0.5 * mm});
            skCircle(sketch, "E1.55.12.0", {"center": v(-66.1, 121.84) * mm, "radius": 0.5 * mm});
            skCircle(sketch, "E1.55.13.0", {"center": v(-66.1, 124.38) * mm, "radius": 0.5 * mm});
            skCircle(sketch, "E1.55.14.0", {"center": v(-66.1, 126.92) * mm, "radius": 0.5 * mm});
            skCircle(sketch, "E1.55.15.0", {"center": v(-66.1, 129.46) * mm, "radius": 0.5 * mm});
            skCircle(sketch, "E1.55.16.0", {"center": v(-66.1, 132) * mm, "radius": 0.5 * mm});
            skCircle(sketch, "E1.55.17.0", {"center": v(-66.1, 134.54) * mm, "radius": 0.5 * mm});
            skCircle(sketch, "E1.55.18.0", {"center": v(-66.1, 137.08) * mm, "radius": 0.5 * mm});
            skCircle(sketch, "E1.55.19.0", {"center": v(-66.1, 139.62) * mm, "radius": 0.5 * mm});
            skCircle(sketch, "E1.55.20.0", {"center": v(-66.1, 142.16) * mm, "radius": 0.5 * mm});
            skCircle(sketch, "E1.55.21.0", {"center": v(-66.1, 144.7) * mm, "radius": 0.5 * mm});
            skCircle(sketch, "E1.55.22.0", {"center": v(-66.1, 147.24) * mm, "radius": 0.5 * mm});
            skCircle(sketch, "E1.55.23.0", {"center": v(-66.1, 149.78) * mm, "radius": 0.5 * mm});
            skCircle(sketch, "E1.55.24.0", {"center": v(-66.1, 152.32) * mm, "radius": 0.5 * mm});
            skCircle(sketch, "E1.55.25.0", {"center": v(-66.1, 154.86) * mm, "radius": 0.5 * mm});
            skCircle(sketch, "E1.55.26.0", {"center": v(-66.1, 157.4) * mm, "radius": 0.5 * mm});
            skCircle(sketch, "E1.55.27.0", {"center": v(-66.1, 159.94) * mm, "radius": 0.5 * mm});
            skCircle(sketch, "E1.55.28.0", {"center": v(-66.1, 162.48) * mm, "radius": 0.5 * mm});
            skCircle(sketch, "E1.55.29.0", {"center": v(-66.1, 165.02) * mm, "radius": 0.5 * mm});
            skCircle(sketch, "E1.55.30.0", {"center": v(-66.1, 167.56) * mm, "radius": 0.5 * mm});
            skCircle(sketch, "E1.55.31.0", {"center": v(-66.1, 170.1) * mm, "radius": 0.5 * mm});
            skCircle(sketch, "E1.55.32.0", {"center": v(-66.1, 172.64) * mm, "radius": 0.5 * mm});
            skCircle(sketch, "E1.55.33.0", {"center": v(-66.1, 175.18) * mm, "radius": 0.5 * mm});
            skCircle(sketch, "E1.55.34.0", {"center": v(-66.1, 177.72) * mm, "radius": 0.5 * mm});
            skCircle(sketch, "E1.55.35.0", {"center": v(-66.1, 180.26) * mm, "radius": 0.5 * mm});
            skCircle(sketch, "E1.55.36.0", {"center": v(-66.1, 182.8) * mm, "radius": 0.5 * mm});
            skCircle(sketch, "E1.55.37.0", {"center": v(-66.1, 185.34) * mm, "radius": 0.5 * mm});
            skCircle(sketch, "E1.56.0.0", {"center": v(-63.57, 91.36) * mm, "radius": 0.5 * mm});
            skCircle(sketch, "E1.56.1.0", {"center": v(-63.57, 93.9) * mm, "radius": 0.5 * mm});
            skCircle(sketch, "E1.56.2.0", {"center": v(-63.57, 96.44) * mm, "radius": 0.5 * mm});
            skCircle(sketch, "E1.56.3.0", {"center": v(-63.57, 98.98) * mm, "radius": 0.5 * mm});
            skCircle(sketch, "E1.56.4.0", {"center": v(-63.57, 101.52) * mm, "radius": 0.5 * mm});
            skCircle(sketch, "E1.56.5.0", {"center": v(-63.57, 104.06) * mm, "radius": 0.5 * mm});
            skCircle(sketch, "E1.56.6.0", {"center": v(-63.57, 106.6) * mm, "radius": 0.5 * mm});
            skCircle(sketch, "E1.56.7.0", {"center": v(-63.57, 109.14) * mm, "radius": 0.5 * mm});
            skCircle(sketch, "E1.56.8.0", {"center": v(-63.57, 111.68) * mm, "radius": 0.5 * mm});
            skCircle(sketch, "E1.56.9.0", {"center": v(-63.57, 114.22) * mm, "radius": 0.5 * mm});
            skCircle(sketch, "E1.56.10.0", {"center": v(-63.57, 116.76) * mm, "radius": 0.5 * mm});
            skCircle(sketch, "E1.56.11.0", {"center": v(-63.57, 119.3) * mm, "radius": 0.5 * mm});
            skCircle(sketch, "E1.56.12.0", {"center": v(-63.57, 121.84) * mm, "radius": 0.5 * mm});
            skCircle(sketch, "E1.56.13.0", {"center": v(-63.57, 124.38) * mm, "radius": 0.5 * mm});
            skCircle(sketch, "E1.56.14.0", {"center": v(-63.57, 126.92) * mm, "radius": 0.5 * mm});
            skCircle(sketch, "E1.56.15.0", {"center": v(-63.57, 129.46) * mm, "radius": 0.5 * mm});
            skCircle(sketch, "E1.56.16.0", {"center": v(-63.57, 132) * mm, "radius": 0.5 * mm});
            skCircle(sketch, "E1.56.17.0", {"center": v(-63.57, 134.54) * mm, "radius": 0.5 * mm});
            skCircle(sketch, "E1.56.18.0", {"center": v(-63.57, 137.08) * mm, "radius": 0.5 * mm});
            skCircle(sketch, "E1.56.19.0", {"center": v(-63.57, 139.62) * mm, "radius": 0.5 * mm});
            skCircle(sketch, "E1.56.20.0", {"center": v(-63.57, 142.16) * mm, "radius": 0.5 * mm});
            skCircle(sketch, "E1.56.21.0", {"center": v(-63.57, 144.7) * mm, "radius": 0.5 * mm});
            skCircle(sketch, "E1.56.22.0", {"center": v(-63.57, 147.24) * mm, "radius": 0.5 * mm});
            skCircle(sketch, "E1.56.23.0", {"center": v(-63.57, 149.78) * mm, "radius": 0.5 * mm});
            skCircle(sketch, "E1.56.24.0", {"center": v(-63.57, 152.32) * mm, "radius": 0.5 * mm});
            skCircle(sketch, "E1.56.25.0", {"center": v(-63.57, 154.86) * mm, "radius": 0.5 * mm});
            skCircle(sketch, "E1.56.26.0", {"center": v(-63.57, 157.4) * mm, "radius": 0.5 * mm});
            skCircle(sketch, "E1.56.27.0", {"center": v(-63.57, 159.94) * mm, "radius": 0.5 * mm});
            skCircle(sketch, "E1.56.28.0", {"center": v(-63.57, 162.48) * mm, "radius": 0.5 * mm});
            skCircle(sketch, "E1.56.29.0", {"center": v(-63.57, 165.02) * mm, "radius": 0.5 * mm});
            skCircle(sketch, "E1.56.30.0", {"center": v(-63.57, 167.56) * mm, "radius": 0.5 * mm});
            skCircle(sketch, "E1.56.31.0", {"center": v(-63.57, 170.1) * mm, "radius": 0.5 * mm});
            skCircle(sketch, "E1.56.32.0", {"center": v(-63.57, 172.64) * mm, "radius": 0.5 * mm});
            skCircle(sketch, "E1.56.33.0", {"center": v(-63.57, 175.18) * mm, "radius": 0.5 * mm});
            skCircle(sketch, "E1.56.34.0", {"center": v(-63.57, 177.72) * mm, "radius": 0.5 * mm});
            skCircle(sketch, "E1.56.35.0", {"center": v(-63.57, 180.26) * mm, "radius": 0.5 * mm});
            skCircle(sketch, "E1.56.36.0", {"center": v(-63.57, 182.8) * mm, "radius": 0.5 * mm});
            skCircle(sketch, "E1.56.37.0", {"center": v(-63.57, 185.34) * mm, "radius": 0.5 * mm});
            skCircle(sketch, "E1.57.0.0", {"center": v(-61.03, 91.36) * mm, "radius": 0.5 * mm});
            skCircle(sketch, "E1.57.1.0", {"center": v(-61.03, 93.9) * mm, "radius": 0.5 * mm});
            skCircle(sketch, "E1.57.2.0", {"center": v(-61.03, 96.44) * mm, "radius": 0.5 * mm});
            skCircle(sketch, "E1.57.3.0", {"center": v(-61.03, 98.98) * mm, "radius": 0.5 * mm});
            skCircle(sketch, "E1.57.4.0", {"center": v(-61.03, 101.52) * mm, "radius": 0.5 * mm});
            skCircle(sketch, "E1.57.5.0", {"center": v(-61.03, 104.06) * mm, "radius": 0.5 * mm});
            skCircle(sketch, "E1.57.6.0", {"center": v(-61.03, 106.6) * mm, "radius": 0.5 * mm});
            skCircle(sketch, "E1.57.7.0", {"center": v(-61.03, 109.14) * mm, "radius": 0.5 * mm});
            skCircle(sketch, "E1.57.8.0", {"center": v(-61.03, 111.68) * mm, "radius": 0.5 * mm});
            skCircle(sketch, "E1.57.9.0", {"center": v(-61.03, 114.22) * mm, "radius": 0.5 * mm});
            skCircle(sketch, "E1.57.10.0", {"center": v(-61.03, 116.76) * mm, "radius": 0.5 * mm});
            skCircle(sketch, "E1.57.11.0", {"center": v(-61.03, 119.3) * mm, "radius": 0.5 * mm});
            skCircle(sketch, "E1.57.12.0", {"center": v(-61.03, 121.84) * mm, "radius": 0.5 * mm});
            skCircle(sketch, "E1.57.13.0", {"center": v(-61.03, 124.38) * mm, "radius": 0.5 * mm});
            skCircle(sketch, "E1.57.14.0", {"center": v(-61.03, 126.92) * mm, "radius": 0.5 * mm});
            skCircle(sketch, "E1.57.15.0", {"center": v(-61.03, 129.46) * mm, "radius": 0.5 * mm});
            skCircle(sketch, "E1.57.16.0", {"center": v(-61.03, 132) * mm, "radius": 0.5 * mm});
            skCircle(sketch, "E1.57.17.0", {"center": v(-61.03, 134.54) * mm, "radius": 0.5 * mm});
            skCircle(sketch, "E1.57.18.0", {"center": v(-61.03, 137.08) * mm, "radius": 0.5 * mm});
            skCircle(sketch, "E1.57.19.0", {"center": v(-61.03, 139.62) * mm, "radius": 0.5 * mm});
            skCircle(sketch, "E1.57.20.0", {"center": v(-61.03, 142.16) * mm, "radius": 0.5 * mm});
            skCircle(sketch, "E1.57.21.0", {"center": v(-61.03, 144.7) * mm, "radius": 0.5 * mm});
            skCircle(sketch, "E1.57.22.0", {"center": v(-61.03, 147.24) * mm, "radius": 0.5 * mm});
            skCircle(sketch, "E1.57.23.0", {"center": v(-61.03, 149.78) * mm, "radius": 0.5 * mm});
            skCircle(sketch, "E1.57.24.0", {"center": v(-61.03, 152.32) * mm, "radius": 0.5 * mm});
            skCircle(sketch, "E1.57.25.0", {"center": v(-61.03, 154.86) * mm, "radius": 0.5 * mm});
            skCircle(sketch, "E1.57.26.0", {"center": v(-61.03, 157.4) * mm, "radius": 0.5 * mm});
            skCircle(sketch, "E1.57.27.0", {"center": v(-61.03, 159.94) * mm, "radius": 0.5 * mm});
            skCircle(sketch, "E1.57.28.0", {"center": v(-61.03, 162.48) * mm, "radius": 0.5 * mm});
            skCircle(sketch, "E1.57.29.0", {"center": v(-61.03, 165.02) * mm, "radius": 0.5 * mm});
            skCircle(sketch, "E1.57.30.0", {"center": v(-61.03, 167.56) * mm, "radius": 0.5 * mm});
            skCircle(sketch, "E1.57.31.0", {"center": v(-61.03, 170.1) * mm, "radius": 0.5 * mm});
            skCircle(sketch, "E1.57.32.0", {"center": v(-61.03, 172.64) * mm, "radius": 0.5 * mm});
            skCircle(sketch, "E1.57.33.0", {"center": v(-61.03, 175.18) * mm, "radius": 0.5 * mm});
            skCircle(sketch, "E1.57.34.0", {"center": v(-61.03, 177.72) * mm, "radius": 0.5 * mm});
            skCircle(sketch, "E1.57.35.0", {"center": v(-61.03, 180.26) * mm, "radius": 0.5 * mm});
            skCircle(sketch, "E1.57.36.0", {"center": v(-61.03, 182.8) * mm, "radius": 0.5 * mm});
            skCircle(sketch, "E1.57.37.0", {"center": v(-61.03, 185.34) * mm, "radius": 0.5 * mm});
            skCircle(sketch, "E1.58.0.0", {"center": v(-58.49, 91.36) * mm, "radius": 0.5 * mm});
            skCircle(sketch, "E1.58.1.0", {"center": v(-58.49, 93.9) * mm, "radius": 0.5 * mm});
            skCircle(sketch, "E1.58.2.0", {"center": v(-58.49, 96.44) * mm, "radius": 0.5 * mm});
            skCircle(sketch, "E1.58.3.0", {"center": v(-58.49, 98.98) * mm, "radius": 0.5 * mm});
            skCircle(sketch, "E1.58.4.0", {"center": v(-58.49, 101.52) * mm, "radius": 0.5 * mm});
            skCircle(sketch, "E1.58.5.0", {"center": v(-58.49, 104.06) * mm, "radius": 0.5 * mm});
            skCircle(sketch, "E1.58.6.0", {"center": v(-58.49, 106.6) * mm, "radius": 0.5 * mm});
            skCircle(sketch, "E1.58.7.0", {"center": v(-58.49, 109.14) * mm, "radius": 0.5 * mm});
            skCircle(sketch, "E1.58.8.0", {"center": v(-58.49, 111.68) * mm, "radius": 0.5 * mm});
            skCircle(sketch, "E1.58.9.0", {"center": v(-58.49, 114.22) * mm, "radius": 0.5 * mm});
            skCircle(sketch, "E1.58.10.0", {"center": v(-58.49, 116.76) * mm, "radius": 0.5 * mm});
            skCircle(sketch, "E1.58.11.0", {"center": v(-58.49, 119.3) * mm, "radius": 0.5 * mm});
            skCircle(sketch, "E1.58.12.0", {"center": v(-58.49, 121.84) * mm, "radius": 0.5 * mm});
            skCircle(sketch, "E1.58.13.0", {"center": v(-58.49, 124.38) * mm, "radius": 0.5 * mm});
            skCircle(sketch, "E1.58.14.0", {"center": v(-58.49, 126.92) * mm, "radius": 0.5 * mm});
            skCircle(sketch, "E1.58.15.0", {"center": v(-58.49, 129.46) * mm, "radius": 0.5 * mm});
            skCircle(sketch, "E1.58.16.0", {"center": v(-58.49, 132) * mm, "radius": 0.5 * mm});
            skCircle(sketch, "E1.58.17.0", {"center": v(-58.49, 134.54) * mm, "radius": 0.5 * mm});
            skCircle(sketch, "E1.58.18.0", {"center": v(-58.49, 137.08) * mm, "radius": 0.5 * mm});
            skCircle(sketch, "E1.58.19.0", {"center": v(-58.49, 139.62) * mm, "radius": 0.5 * mm});
            skCircle(sketch, "E1.58.20.0", {"center": v(-58.49, 142.16) * mm, "radius": 0.5 * mm});
            skCircle(sketch, "E1.58.21.0", {"center": v(-58.49, 144.7) * mm, "radius": 0.5 * mm});
            skCircle(sketch, "E1.58.22.0", {"center": v(-58.49, 147.24) * mm, "radius": 0.5 * mm});
            skCircle(sketch, "E1.58.23.0", {"center": v(-58.49, 149.78) * mm, "radius": 0.5 * mm});
            skCircle(sketch, "E1.58.24.0", {"center": v(-58.49, 152.32) * mm, "radius": 0.5 * mm});
            skCircle(sketch, "E1.58.25.0", {"center": v(-58.49, 154.86) * mm, "radius": 0.5 * mm});
            skCircle(sketch, "E1.58.26.0", {"center": v(-58.49, 157.4) * mm, "radius": 0.5 * mm});
            skCircle(sketch, "E1.58.27.0", {"center": v(-58.49, 159.94) * mm, "radius": 0.5 * mm});
            skCircle(sketch, "E1.58.28.0", {"center": v(-58.49, 162.48) * mm, "radius": 0.5 * mm});
            skCircle(sketch, "E1.58.29.0", {"center": v(-58.49, 165.02) * mm, "radius": 0.5 * mm});
            skCircle(sketch, "E1.58.30.0", {"center": v(-58.49, 167.56) * mm, "radius": 0.5 * mm});
            skCircle(sketch, "E1.58.31.0", {"center": v(-58.49, 170.1) * mm, "radius": 0.5 * mm});
            skCircle(sketch, "E1.58.32.0", {"center": v(-58.49, 172.64) * mm, "radius": 0.5 * mm});
            skCircle(sketch, "E1.58.33.0", {"center": v(-58.49, 175.18) * mm, "radius": 0.5 * mm});
            skCircle(sketch, "E1.58.34.0", {"center": v(-58.49, 177.72) * mm, "radius": 0.5 * mm});
            skCircle(sketch, "E1.58.35.0", {"center": v(-58.49, 180.26) * mm, "radius": 0.5 * mm});
            skCircle(sketch, "E1.58.36.0", {"center": v(-58.49, 182.8) * mm, "radius": 0.5 * mm});
            skCircle(sketch, "E1.58.37.0", {"center": v(-58.49, 185.34) * mm, "radius": 0.5 * mm});
            skCircle(sketch, "E1.59.0.0", {"center": v(-55.95, 91.36) * mm, "radius": 0.5 * mm});
            skCircle(sketch, "E1.59.1.0", {"center": v(-55.95, 93.9) * mm, "radius": 0.5 * mm});
            skCircle(sketch, "E1.59.2.0", {"center": v(-55.95, 96.44) * mm, "radius": 0.5 * mm});
            skCircle(sketch, "E1.59.3.0", {"center": v(-55.95, 98.98) * mm, "radius": 0.5 * mm});
            skCircle(sketch, "E1.59.4.0", {"center": v(-55.95, 101.52) * mm, "radius": 0.5 * mm});
            skCircle(sketch, "E1.59.5.0", {"center": v(-55.95, 104.06) * mm, "radius": 0.5 * mm});
            skCircle(sketch, "E1.59.6.0", {"center": v(-55.95, 106.6) * mm, "radius": 0.5 * mm});
            skCircle(sketch, "E1.59.7.0", {"center": v(-55.95, 109.14) * mm, "radius": 0.5 * mm});
            skCircle(sketch, "E1.59.8.0", {"center": v(-55.95, 111.68) * mm, "radius": 0.5 * mm});
            skCircle(sketch, "E1.59.9.0", {"center": v(-55.95, 114.22) * mm, "radius": 0.5 * mm});
            skCircle(sketch, "E1.59.10.0", {"center": v(-55.95, 116.76) * mm, "radius": 0.5 * mm});
            skCircle(sketch, "E1.59.11.0", {"center": v(-55.95, 119.3) * mm, "radius": 0.5 * mm});
            skCircle(sketch, "E1.59.12.0", {"center": v(-55.95, 121.84) * mm, "radius": 0.5 * mm});
            skCircle(sketch, "E1.59.13.0", {"center": v(-55.95, 124.38) * mm, "radius": 0.5 * mm});
            skCircle(sketch, "E1.59.14.0", {"center": v(-55.95, 126.92) * mm, "radius": 0.5 * mm});
            skCircle(sketch, "E1.59.15.0", {"center": v(-55.95, 129.46) * mm, "radius": 0.5 * mm});
            skCircle(sketch, "E1.59.16.0", {"center": v(-55.95, 132) * mm, "radius": 0.5 * mm});
            skCircle(sketch, "E1.59.17.0", {"center": v(-55.95, 134.54) * mm, "radius": 0.5 * mm});
            skCircle(sketch, "E1.59.18.0", {"center": v(-55.95, 137.08) * mm, "radius": 0.5 * mm});
            skCircle(sketch, "E1.59.19.0", {"center": v(-55.95, 139.62) * mm, "radius": 0.5 * mm});
            skCircle(sketch, "E1.59.20.0", {"center": v(-55.95, 142.16) * mm, "radius": 0.5 * mm});
            skCircle(sketch, "E1.59.21.0", {"center": v(-55.95, 144.7) * mm, "radius": 0.5 * mm});
            skCircle(sketch, "E1.59.22.0", {"center": v(-55.95, 147.24) * mm, "radius": 0.5 * mm});
            skCircle(sketch, "E1.59.23.0", {"center": v(-55.95, 149.78) * mm, "radius": 0.5 * mm});
            skCircle(sketch, "E1.59.24.0", {"center": v(-55.95, 152.32) * mm, "radius": 0.5 * mm});
            skCircle(sketch, "E1.59.25.0", {"center": v(-55.95, 154.86) * mm, "radius": 0.5 * mm});
            skCircle(sketch, "E1.59.26.0", {"center": v(-55.95, 157.4) * mm, "radius": 0.5 * mm});
            skCircle(sketch, "E1.59.27.0", {"center": v(-55.95, 159.94) * mm, "radius": 0.5 * mm});
            skCircle(sketch, "E1.59.28.0", {"center": v(-55.95, 162.48) * mm, "radius": 0.5 * mm});
            skCircle(sketch, "E1.59.29.0", {"center": v(-55.95, 165.02) * mm, "radius": 0.5 * mm});
            skCircle(sketch, "E1.59.30.0", {"center": v(-55.95, 167.56) * mm, "radius": 0.5 * mm});
            skCircle(sketch, "E1.59.31.0", {"center": v(-55.95, 170.1) * mm, "radius": 0.5 * mm});
            skCircle(sketch, "E1.59.32.0", {"center": v(-55.95, 172.64) * mm, "radius": 0.5 * mm});
            skCircle(sketch, "E1.59.33.0", {"center": v(-55.95, 175.18) * mm, "radius": 0.5 * mm});
            skCircle(sketch, "E1.59.34.0", {"center": v(-55.95, 177.72) * mm, "radius": 0.5 * mm});
            skCircle(sketch, "E1.59.35.0", {"center": v(-55.95, 180.26) * mm, "radius": 0.5 * mm});
            skCircle(sketch, "E1.59.36.0", {"center": v(-55.95, 182.8) * mm, "radius": 0.5 * mm});
            skCircle(sketch, "E1.59.37.0", {"center": v(-55.95, 185.34) * mm, "radius": 0.5 * mm});
            skLineSegment(sketch, "E1.direction1", {"start": v(-205.8, 91.36) * mm, "end": v(-203.27, 91.36) * mm, "construction": true});
            skLineSegment(sketch, "E1.direction2", {"start": v(-205.8, 91.36) * mm, "end": v(-205.8, 93.9) * mm, "construction": true});
            skLineSegment(sketch, "E2.bottom", {"start": v(-206.97, 186.3) * mm, "end": v(-199.23, 186.3) * mm});
            skLineSegment(sketch, "E2.top", {"start": v(-206.97, 181.12) * mm, "end": v(-199.23, 181.12) * mm});
            skLineSegment(sketch, "E2.left", {"start": v(-206.97, 186.3) * mm, "end": v(-206.97, 181.12) * mm});
            skLineSegment(sketch, "E2.right", {"start": v(-199.23, 186.3) * mm, "end": v(-199.23, 181.12) * mm});
            skLineSegment(sketch, "E3.bottom", {"start": v(-50.5, 87.18) * mm, "end": v(-209.54, 87.18) * mm});
            skLineSegment(sketch, "E3.top", {"start": v(-50.5, 191.01) * mm, "end": v(-209.54, 191.01) * mm});
            skLineSegment(sketch, "E3.left", {"start": v(-50.5, 87.18) * mm, "end": v(-50.5, 191.01) * mm});
            skLineSegment(sketch, "E3.right", {"start": v(-209.54, 87.18) * mm, "end": v(-209.54, 191.01) * mm});
            skSolve(sketch);
        }
        {
            var Q0;
            Q0=makeQuery(id+"F0.imprint","IMPRINT",FACE,{"disambiguationData":[TD([[makeQuery(id+"F0.imprint","IMPRINT",EDGE,{"derivedFrom":sQuery(id+"F0.wireOp",EDGE,"E1.0.36.0")}),-1.0]])]});
            var Q1;
            Q1=makeQuery(id+"F0.imprint","IMPRINT",FACE,{"disambiguationData":[TD([[makeQuery(id+"F0.imprint","IMPRINT",EDGE,{"derivedFrom":sQuery(id+"F0.wireOp",EDGE,"E0")}),-1.0]])]});
            extrude(context, id + "F1", {"entities" : qUnion([Q0, Q1]), "depth" : 1.8 * mm, "offsetDistance" : 25 * mm});
        }
    });
